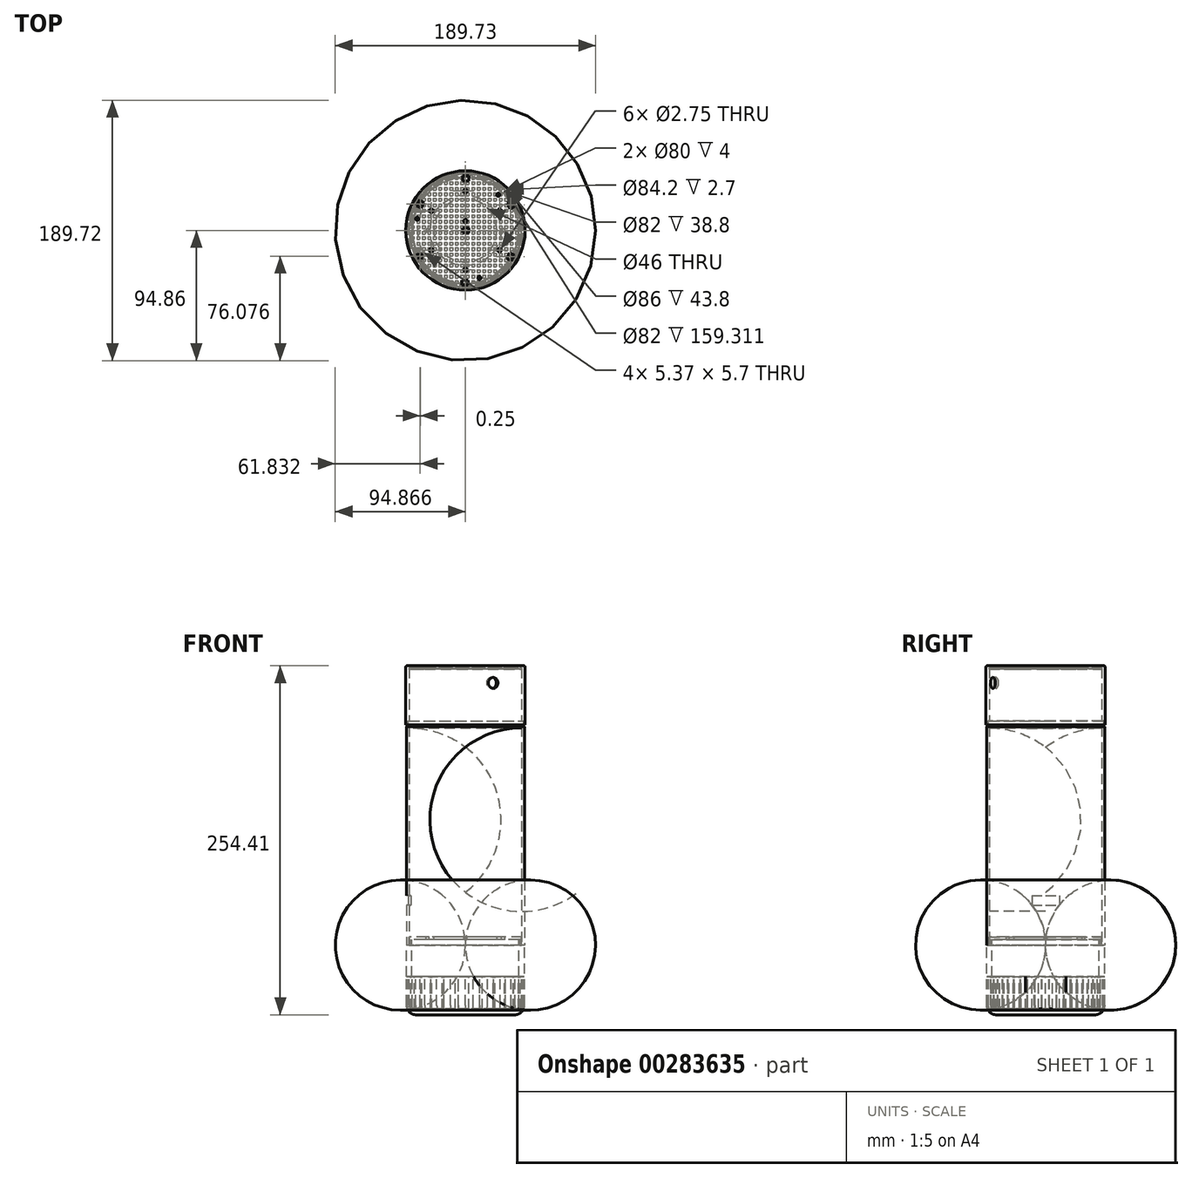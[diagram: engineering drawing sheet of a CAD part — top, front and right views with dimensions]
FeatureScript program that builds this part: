
annotation { "Feature Type Name" : "Feature", "Feature Type Description" : "" }
export const myFeature = defineFeature(function(context is Context, id is Id, definition is map)
    precondition{}
    {
        {
            var Q0;
            Q0=qCreatedBy(makeId("Front.planeOp"),FACE);
            var sketch = newSketch(context, id + "F0", { "sketchPlane" : qUnion([Q0])});
            skLineSegment(sketch, "E0", {"start": v(-50.53, -12.24) * mm, "end": v(-47.53, -12.24) * mm});
            skLineSegment(sketch, "E1", {"start": v(-7.53, -12.24) * mm, "end": v(-7.53, -63.04) * mm});
            skLineSegment(sketch, "E2", {"start": v(-50.53, -12.24) * mm, "end": v(-50.53, -56.04) * mm});
            skLineSegment(sketch, "E3", {"start": v(-7.53, -63.04) * mm, "end": v(-37.53, -63.04) * mm});
            skPoint(sketch, "E4.visualSharp", {"position": v(-50.53, -63.04) * mm});
            skArc(sketch, "E4.filletArc", {"start": v(-50.53, -56.04) * mm, "mid": v(-48.48, -61) * mm, "end": v(-43.53, -63.04) * mm});
            skLineSegment(sketch, "E5", {"start": v(-40.53, -63.04) * mm, "end": v(-37.53, -63.04) * mm});
            skLineSegment(sketch, "E6", {"start": v(-7.53, -63.04) * mm, "end": v(-7.53, -61.54) * mm});
            skLineSegment(sketch, "E7", {"start": v(-47.53, -12.24) * mm, "end": v(-47.53, -54.54) * mm});
            skLineSegment(sketch, "E8", {"start": v(-7.53, -61.54) * mm, "end": v(-40.53, -61.54) * mm});
            skPoint(sketch, "E9", {"position": v(-50.53, -34.14) * mm});
            skLineSegment(sketch, "E10", {"start": v(-50.53, -34.14) * mm, "end": v(-50.53, -47.14) * mm, "construction": true});
            skPoint(sketch, "E11", {"position": v(-50.53, -47.14) * mm});
            skLineSegment(sketch, "E12", {"start": v(-7.53, -63.04) * mm, "end": v(-7.53, 112.76) * mm, "construction": true});
            skLineSegment(sketch, "E13", {"start": v(-7.53, -8.24) * mm, "end": v(-7.53, -6.24) * mm});
            skLineSegment(sketch, "E14", {"start": v(-7.53, -59.5) * mm, "end": v(-7.53, -52.5) * mm});
            skLineSegment(sketch, "E15", {"start": v(-43.53, -63.04) * mm, "end": v(-40.53, -63.04) * mm});
            skLineSegment(sketch, "E16", {"start": v(-49.53, 148.07) * mm, "end": v(-48.53, 148.07) * mm});
            skLineSegment(sketch, "E17", {"start": v(-51.03, 191.37) * mm, "end": v(-7.53, 191.37) * mm});
            skLineSegment(sketch, "E18", {"start": v(-7.53, 191.37) * mm, "end": v(-7.53, 189.87) * mm});
            skPoint(sketch, "E19", {"position": v(-50.53, 181.87) * mm});
            skPoint(sketch, "E20", {"position": v(-47.73, 181.87) * mm});
            skLineSegment(sketch, "E21", {"start": v(-48.53, 151.07) * mm, "end": v(-48.53, 189.87) * mm});
            skLineSegment(sketch, "E22", {"start": v(-7.53, 191.37) * mm, "end": v(-7.53, 112.76) * mm, "construction": true});
            skPoint(sketch, "E23.end.orphan", {"position": v(-50.53, -2.93) * mm});
            skLineSegment(sketch, "E24", {"start": v(-50.53, -2.93) * mm, "end": v(-50.53, -12.24) * mm});
            skLineSegment(sketch, "E25", {"start": v(-48.53, -6.24) * mm, "end": v(-48.53, -12.24) * mm});
            skLineSegment(sketch, "E26", {"start": v(-47.53, -12.24) * mm, "end": v(-46.53, -12.24) * mm});
            skLineSegment(sketch, "E27", {"start": v(-48.53, -12.24) * mm, "end": v(-48.48, -12.24) * mm});
            skLineSegment(sketch, "E28", {"start": v(-48.48, -12.24) * mm, "end": v(-48.48, -6.24) * mm});
            skLineSegment(sketch, "E29", {"start": v(-48.48, -6.24) * mm, "end": v(-47.53, -6.24) * mm});
            skLineSegment(sketch, "E30", {"start": v(-47.53, -6.24) * mm, "end": v(-47.53, -12.24) * mm});
            skLineSegment(sketch, "E31", {"start": v(-7.53, -6.24) * mm, "end": v(-48.48, -6.24) * mm});
            skLineSegment(sketch, "E32", {"start": v(-7.53, -8.24) * mm, "end": v(-47.53, -8.24) * mm});
            skLineSegment(sketch, "E33", {"start": v(-47.53, -12.24) * mm, "end": v(-47.48, -12.24) * mm});
            skLineSegment(sketch, "E34", {"start": v(-47.48, -12.24) * mm, "end": v(-47.48, -8.24) * mm});
            skLineSegment(sketch, "E35", {"start": v(-47.48, -8.24) * mm, "end": v(-46.53, -8.24) * mm});
            skLineSegment(sketch, "E36", {"start": v(-46.53, -8.24) * mm, "end": v(-46.53, -12.24) * mm});
            skLineSegment(sketch, "E37", {"start": v(-46.53, -12.24) * mm, "end": v(-46.53, -58.92) * mm});
            skArc(sketch, "E38", {"start": v(-46.53, -58.92) * mm, "mid": v(-43.86, -60.98) * mm, "end": v(-40.53, -61.54) * mm});
            skArc(sketch, "E39", {"start": v(-46.53, -58.92) * mm, "mid": v(-18.57, -42.66) * mm, "end": v(-7.53, -12.24) * mm});
            skLineSegment(sketch, "E40", {"start": v(-49.58, 147.07) * mm, "end": v(-50.53, 147.07) * mm, "construction": true});
            skLineSegment(sketch, "E41", {"start": v(-49.53, 148.07) * mm, "end": v(-49.53, 147.07) * mm});
            skLineSegment(sketch, "E42", {"start": v(-49.53, 147.07) * mm, "end": v(-7.53, 147.07) * mm});
            skLineSegment(sketch, "E43", {"start": v(-48.53, 148.07) * mm, "end": v(-7.53, 148.07) * mm});
            skLineSegment(sketch, "E44", {"start": v(-7.53, 148.07) * mm, "end": v(-7.53, 147.07) * mm});
            skLineSegment(sketch, "E45", {"start": v(-49.58, 147.07) * mm, "end": v(-48.53, 147.07) * mm});
            skLineSegment(sketch, "E46", {"start": v(-48.53, 147.07) * mm, "end": v(-48.53, -6.24) * mm});
            skLineSegment(sketch, "E47", {"start": v(-48.53, -6.24) * mm, "end": v(-47.53, -6.24) * mm, "construction": true});
            skLineSegment(sketch, "E48", {"start": v(-48.53, 147.07) * mm, "end": v(-48.48, 147.07) * mm});
            skLineSegment(sketch, "E49", {"start": v(-48.48, 147.07) * mm, "end": v(-48.48, 146.07) * mm});
            skLineSegment(sketch, "E50", {"start": v(-7.53, 147.07) * mm, "end": v(-7.53, 132.07) * mm});
            skLineSegment(sketch, "E51", {"start": v(-48.48, 146.07) * mm, "end": v(-7.53, 146.07) * mm, "construction": true});
            skArc(sketch, "E52", {"start": v(-7.53, 132.07) * mm, "mid": v(-26.85, 142.47) * mm, "end": v(-48.48, 146.07) * mm});
            skLineSegment(sketch, "E53", {"start": v(-48.48, -6.24) * mm, "end": v(-48.53, 10.54) * mm, "construction": true});
            skLineSegment(sketch, "E54", {"start": v(-48.48, -6.24) * mm, "end": v(-48.53, 23.76) * mm, "construction": true});
            skPoint(sketch, "E55", {"position": v(-48.53, 23.76) * mm});
            skLineSegment(sketch, "E56", {"start": v(-51.03, 151.07) * mm, "end": v(-51.03, 191.37) * mm});
            skLineSegment(sketch, "E57", {"start": v(-48.53, 148.07) * mm, "end": v(-48.53, 147.07) * mm, "construction": true});
            skLineSegment(sketch, "E58", {"start": v(-48.53, 189.87) * mm, "end": v(-7.53, 189.87) * mm});
            skLineSegment(sketch, "E59", {"start": v(-50.53, -2.93) * mm, "end": v(-50.53, 147.07) * mm});
            skLineSegment(sketch, "E60", {"start": v(-50.53, 147.07) * mm, "end": v(-49.53, 147.07) * mm});
            skLineSegment(sketch, "E61", {"start": v(-51.03, 151.07) * mm, "end": v(-51.03, 148.37) * mm});
            skLineSegment(sketch, "E62", {"start": v(-51.03, 148.37) * mm, "end": v(-49.63, 148.37) * mm});
            skLineSegment(sketch, "E63", {"start": v(-49.63, 148.37) * mm, "end": v(-49.63, 151.07) * mm});
            skLineSegment(sketch, "E64", {"start": v(-49.63, 151.07) * mm, "end": v(-48.53, 151.07) * mm});
            skSolve(sketch);
        }
        {
            var Q0;
            {var subQ1=sQuery(id+"F0.wireOp",EDGE,"E0");Q0=makeQuery(id+"F0.imprint","IMPRINT",FACE,{"disambiguationData":[TD([[makeQuery(id+"F0.imprint","IMPRINT",EDGE,{"derivedFrom":subQ1}),-1.0]])]});}
            var Q1;
            Q1=makeQuery(id+"F0.imprint","IMPRINT",FACE,{"disambiguationData":[TD([[makeQuery(id+"F0.imprint","IMPRINT",EDGE,{"derivedFrom":sQuery(id+"F0.wireOp",EDGE,"E1")}),-1.0]])]});
            var Q2;
            Q2=makeQuery(id+"F0.imprint","IMPRINT",FACE,{"disambiguationData":[TD([[makeQuery(id+"F0.imprint","IMPRINT",EDGE,{"derivedFrom":sQuery(id+"F0.wireOp",EDGE,"E26")}),1.0]])]});
            var Q3;
            Q3=sQuery(id+"F0.wireOp",EDGE,"E1");
            revolve(context, id + "F1", {"entities" : qUnion([Q0, Q1, Q2]), "axis" : qUnion([Q3]), "revolveType" : RevolveType.FULL});
        }
        {
            var Q0;
            Q0=sQuery(id+"F0.wireOp",EDGE,"E2");
            var Q1;
            Q1=sQuery(id+"F0.wireOp",VERTEX,"E11");
            cPlane(context, id + "F2", {"entities" : qUnion([Q0, Q1]), "cplaneType" : CPlaneType.LINE_POINT, "offset" : 0 * mm, "width" : 150 * mm, "height" : 150 * mm});
        }
        {
            var Q0;
            Q0=qCreatedBy(id+"F2.planeOp",FACE);
            var sketch = newSketch(context, id + "F3", { "sketchPlane" : qUnion([Q0])});
            skLineSegment(sketch, "E65", {"start": v(-50.53, 0) * mm, "end": v(-46.03, 0) * mm, "construction": true});
            skLineSegment(sketch, "E66", {"start": v(-46.03, 0) * mm, "end": v(-46.03, 2.5) * mm, "construction": true});
            skLineSegment(sketch, "E67", {"start": v(-46.03, 2.5) * mm, "end": v(-50.53, 2.5) * mm});
            skLineSegment(sketch, "E68", {"start": v(-50.53, 2.5) * mm, "end": v(-50.53, -2.5) * mm});
            skLineSegment(sketch, "E69", {"start": v(-50.53, -2.5) * mm, "end": v(-46.03, -2.5) * mm});
            skLineSegment(sketch, "E70", {"start": v(-46.03, -2.5) * mm, "end": v(-46.03, 2.5) * mm});
            skLineSegment(sketch, "E71", {"start": v(-46.03, -6.5) * mm, "end": v(-46.03, -2.5) * mm});
            skLineSegment(sketch, "E72.MirrorCS", {"start": v(-46.03, 6.5) * mm, "end": v(-46.03, 2.5) * mm});
            skLineSegment(sketch, "E73", {"start": v(-46.03, -2.5) * mm, "end": v(-47.13, -2.5) * mm, "construction": true});
            skLineSegment(sketch, "E74", {"start": v(-47.13, -2.5) * mm, "end": v(-47.13, -5.3) * mm, "construction": true});
            skArc(sketch, "E75", {"start": v(-47.13, -5.3) * mm, "mid": v(-48.33, -3.3) * mm, "end": v(-50.53, -2.5) * mm});
            skArc(sketch, "E76", {"start": v(-47.13, -5.3) * mm, "mid": v(-46.82, -6.11) * mm, "end": v(-46.03, -6.5) * mm});
            skArc(sketch, "E77.MirrorCS", {"start": v(-47.13, 5.3) * mm, "mid": v(-48.33, 3.3) * mm, "end": v(-50.53, 2.5) * mm});
            skArc(sketch, "E78.MirrorCS", {"start": v(-47.13, 5.3) * mm, "mid": v(-46.82, 6.11) * mm, "end": v(-46.03, 6.5) * mm});
            skSolve(sketch);
        }
        {
            var Q0;
            Q0=qSketchRegion(id+"F3",true);
            extrude(context, id + "F4", {"entities" : qUnion([Q0]), "endBound" : BoundingType.SYMMETRIC, "depth" : 23.8 * mm});
        }
        {
            var Q0;
            Q0=makeQuery(id+"F4.opExtrude","SWEPT_BODY",BODY,{"disambiguationData":[OSD([sQuery(id+"F3.wireOp",EDGE,"E67"),sQuery(id+"F3.wireOp",EDGE,"E68"),sQuery(id+"F3.wireOp",EDGE,"E69"),sQuery(id+"F3.wireOp",EDGE,"E70")])]});
            var Q1;
            Q1=sQuery(id+"F0.wireOp",EDGE,"E1");
            circularPattern(context, id + "F5", {"operationType" : NewBodyOperationType.REMOVE, "entities" : qUnion([Q0]), "axis" : qUnion([Q1]), "angle" : 360 * degree, "instanceCount" : 25, "equalSpace" : true});
        }
        {
            var Q0;
            {var subQ4=sQuery(id+"F0.wireOp",EDGE,"E28");Q0=makeQuery(id+"F0.imprint","IMPRINT",FACE,{"disambiguationData":[TD([[makeQuery(id+"F0.imprint","IMPRINT",EDGE,{"derivedFrom":subQ4}),-1.0]])]});}
            var Q1;
            {var subQ1=sQuery(id+"F0.wireOp",EDGE,"E13");Q1=makeQuery(id+"F0.imprint","IMPRINT",FACE,{"disambiguationData":[TD([[makeQuery(id+"F0.imprint","IMPRINT",EDGE,{"derivedFrom":subQ1}),1.0]])]});}
            var Q2;
            Q2=sQuery(id+"F0.wireOp",EDGE,"E1");
            revolve(context, id + "F6", {"entities" : qUnion([Q0, Q1]), "axis" : qUnion([Q2]), "revolveType" : RevolveType.FULL});
        }
        {
            var Q0;
            {var subQ1=sQuery(id+"F0.wireOp",EDGE,"E24");Q0=makeQuery(id+"F0.imprint","IMPRINT",FACE,{"disambiguationData":[TD([[makeQuery(id+"F0.imprint","IMPRINT",EDGE,{"derivedFrom":subQ1}),1.0]])]});}
            var Q1;
            Q1=sQuery(id+"F0.wireOp",EDGE,"E12");
            revolve(context, id + "F7", {"entities" : qUnion([Q0]), "axis" : qUnion([Q1]), "revolveType" : RevolveType.FULL});
        }
        {
            var Q0;
            Q0=makeQuery(id+"F0.imprint","IMPRINT",FACE,{"disambiguationData":[TD([[makeQuery(id+"F0.imprint","IMPRINT",EDGE,{"derivedFrom":sQuery(id+"F0.wireOp",EDGE,"E16")}),-1.0]])]});
            var Q1;
            Q1=makeQuery(id+"F0.imprint","IMPRINT",FACE,{"disambiguationData":[TD([[makeQuery(id+"F0.imprint","IMPRINT",EDGE,{"derivedFrom":sQuery(id+"F0.wireOp",EDGE,"E42")}),-1.0]])]});
            var Q2;
            Q2=sQuery(id+"F0.wireOp",EDGE,"E50");
            revolve(context, id + "F8", {"entities" : qUnion([Q0, Q1]), "axis" : qUnion([Q2]), "revolveType" : RevolveType.FULL});
        }
        {
            var Q0;
            Q0=makeQuery(id+"F0.imprint","IMPRINT",FACE,{"disambiguationData":[TD([[makeQuery(id+"F0.imprint","IMPRINT",EDGE,{"derivedFrom":sQuery(id+"F0.wireOp",EDGE,"E17")}),-1.0]])]});
            var Q1;
            Q1=sQuery(id+"F0.wireOp",EDGE,"E12");
            revolve(context, id + "F9", {"entities" : qUnion([Q0]), "axis" : qUnion([Q1]), "revolveType" : RevolveType.FULL});
        }
        {
            var Q0;
            Q0=makeQuery(id+"F9.opRevolve","SWEPT_EDGE",EDGE,{"disambiguationData":[OSD([sQuery(id+"F0.wireOp",EDGE,"f6rtj6dZ-6JDe-umgd-hrW0-nHuk5Vi6zJmO"),sQuery(id+"F0.wireOp",EDGE,"E17")])]});
            fillet(context, id + "F10", {"entities" : qUnion([Q0]), "radius" : 1 * mm, "tangentPropagation" : true, "allowEdgeOverflow" : false});
        }
        {
            var Q0;
            Q0=makeQuery(id+"F9.opRevolve","SWEPT_FACE",FACE,{"disambiguationData":[OSD([sQuery(id+"F0.wireOp",EDGE,"E17")])]});
            var sketch = newSketch(context, id + "F11", { "sketchPlane" : qUnion([Q0])});
            skPoint(sketch, "E79", {"position": v(-7.53, 0) * mm});
            skCircle(sketch, "E80", {"center": v(-7.53, 0) * mm, "radius": 40 * mm, "construction": true});
            skLineSegment(sketch, "E81", {"start": v(-7.53, 0) * mm, "end": v(-7.53, -40) * mm, "construction": true});
            skLineSegment(sketch, "E82.1.0", {"start": v(-7.53, 0) * mm, "end": v(27.1, -20) * mm, "construction": true});
            skLineSegment(sketch, "E82.2.0", {"start": v(-7.53, 0) * mm, "end": v(27.1, 20) * mm, "construction": true});
            skLineSegment(sketch, "E82.3.0", {"start": v(-7.53, 0) * mm, "end": v(-7.53, 40) * mm, "construction": true});
            skLineSegment(sketch, "E82.4.0", {"start": v(-7.53, 0) * mm, "end": v(-42.18, 20) * mm, "construction": true});
            skLineSegment(sketch, "E82.5.0", {"start": v(-7.53, 0) * mm, "end": v(-42.18, -20) * mm, "construction": true});
            skLineSegment(sketch, "E83", {"start": v(-7.53, -40) * mm, "end": v(-7.53, -38) * mm, "construction": true});
            skPoint(sketch, "E84", {"position": v(-7.53, -38) * mm});
            skLineSegment(sketch, "E85", {"start": v(-7.53, -38) * mm, "end": v(-5.53, -38) * mm, "construction": true});
            skLineSegment(sketch, "E86", {"start": v(-7.53, -38) * mm, "end": v(-10.03, -38) * mm, "construction": true});
            skLineSegment(sketch, "E87", {"start": v(-7.53, -38) * mm, "end": v(-7.53, -39.8) * mm, "construction": true});
            skLineSegment(sketch, "E88", {"start": v(-7.53, -38) * mm, "end": v(-7.53, -36.2) * mm, "construction": true});
            skLineSegment(sketch, "E89", {"start": v(-7.53, -36.2) * mm, "end": v(-5.53, -36.2) * mm});
            skLineSegment(sketch, "E90", {"start": v(-5.53, -36.2) * mm, "end": v(-5.53, -39.8) * mm});
            skLineSegment(sketch, "E91", {"start": v(-5.53, -39.8) * mm, "end": v(-10.03, -39.8) * mm});
            skLineSegment(sketch, "E92", {"start": v(-10.03, -39.8) * mm, "end": v(-10.03, -36.2) * mm});
            skLineSegment(sketch, "E93", {"start": v(-10.03, -36.2) * mm, "end": v(-7.53, -36.2) * mm});
            skLineSegment(sketch, "E94", {"start": v(-7.53, -38) * mm, "end": v(-7.53, -28.7) * mm, "construction": true});
            skCircle(sketch, "E95", {"center": v(-7.53, -28.7) * mm, "radius": 1.37 * mm});
            skCircle(sketch, "E96.1.0", {"center": v(17.32, -14.35) * mm, "radius": 1.37 * mm});
            skLineSegment(sketch, "E96.1.1", {"start": v(23.82, -18.1) * mm, "end": v(24.82, -16.37) * mm});
            skLineSegment(sketch, "E96.1.2", {"start": v(22.57, -20.27) * mm, "end": v(23.82, -18.1) * mm});
            skLineSegment(sketch, "E96.1.3", {"start": v(25.68, -22.07) * mm, "end": v(22.57, -20.27) * mm});
            skLineSegment(sketch, "E96.1.4", {"start": v(24.82, -16.37) * mm, "end": v(27.93, -18.17) * mm});
            skLineSegment(sketch, "E96.1.5", {"start": v(27.93, -18.17) * mm, "end": v(25.68, -22.07) * mm});
            skCircle(sketch, "E96.2.0", {"center": v(17.32, 14.35) * mm, "radius": 1.37 * mm});
            skLineSegment(sketch, "E96.2.1", {"start": v(23.82, 18.1) * mm, "end": v(22.82, 19.83) * mm});
            skLineSegment(sketch, "E96.2.2", {"start": v(25.07, 15.93) * mm, "end": v(23.82, 18.1) * mm});
            skLineSegment(sketch, "E96.2.3", {"start": v(28.18, 17.73) * mm, "end": v(25.07, 15.93) * mm});
            skLineSegment(sketch, "E96.2.4", {"start": v(22.82, 19.83) * mm, "end": v(25.93, 21.63) * mm});
            skLineSegment(sketch, "E96.2.5", {"start": v(25.93, 21.63) * mm, "end": v(28.18, 17.73) * mm});
            skCircle(sketch, "E96.3.0", {"center": v(-7.53, 28.7) * mm, "radius": 1.37 * mm});
            skLineSegment(sketch, "E96.3.1", {"start": v(-7.53, 36.2) * mm, "end": v(-9.53, 36.2) * mm});
            skLineSegment(sketch, "E96.3.2", {"start": v(-5.03, 36.2) * mm, "end": v(-7.53, 36.2) * mm});
            skLineSegment(sketch, "E96.3.3", {"start": v(-5.03, 39.8) * mm, "end": v(-5.03, 36.2) * mm});
            skLineSegment(sketch, "E96.3.4", {"start": v(-9.53, 36.2) * mm, "end": v(-9.53, 39.8) * mm});
            skLineSegment(sketch, "E96.3.5", {"start": v(-9.53, 39.8) * mm, "end": v(-5.03, 39.8) * mm});
            skCircle(sketch, "E96.4.0", {"center": v(-32.39, 14.35) * mm, "radius": 1.37 * mm});
            skLineSegment(sketch, "E96.4.1", {"start": v(-38.88, 18.1) * mm, "end": v(-39.88, 16.37) * mm});
            skLineSegment(sketch, "E96.4.2", {"start": v(-37.63, 20.27) * mm, "end": v(-38.88, 18.1) * mm});
            skLineSegment(sketch, "E96.4.3", {"start": v(-40.75, 22.07) * mm, "end": v(-37.63, 20.27) * mm});
            skLineSegment(sketch, "E96.4.4", {"start": v(-39.88, 16.37) * mm, "end": v(-43, 18.17) * mm});
            skLineSegment(sketch, "E96.4.5", {"start": v(-43, 18.17) * mm, "end": v(-40.75, 22.07) * mm});
            skCircle(sketch, "E96.5.0", {"center": v(-32.39, -14.35) * mm, "radius": 1.37 * mm});
            skLineSegment(sketch, "E96.5.1", {"start": v(-38.88, -18.1) * mm, "end": v(-37.88, -19.83) * mm});
            skLineSegment(sketch, "E96.5.2", {"start": v(-40.13, -15.93) * mm, "end": v(-38.88, -18.1) * mm});
            skLineSegment(sketch, "E96.5.3", {"start": v(-43.25, -17.73) * mm, "end": v(-40.13, -15.93) * mm});
            skLineSegment(sketch, "E96.5.4", {"start": v(-37.88, -19.83) * mm, "end": v(-41, -21.63) * mm});
            skLineSegment(sketch, "E96.5.5", {"start": v(-41, -21.63) * mm, "end": v(-43.25, -17.73) * mm});
            skLineSegment(sketch, "E97", {"start": v(-7.53, 0) * mm, "end": v(-7.53, 1.8) * mm, "construction": true});
            skLineSegment(sketch, "E98", {"start": v(-7.53, 1.8) * mm, "end": v(-9.53, 1.8) * mm, "construction": true});
            skLineSegment(sketch, "E99.bottom", {"start": v(-9.53, 1.8) * mm, "end": v(-5.03, 1.8) * mm});
            skLineSegment(sketch, "E99.top", {"start": v(-9.53, -1.8) * mm, "end": v(-5.03, -1.8) * mm});
            skLineSegment(sketch, "E99.left", {"start": v(-9.53, 1.8) * mm, "end": v(-9.53, -1.8) * mm});
            skLineSegment(sketch, "E99.right", {"start": v(-5.03, 1.8) * mm, "end": v(-5.03, -1.8) * mm});
            skLineSegment(sketch, "E100", {"start": v(-7.53, 0) * mm, "end": v(-7.53, 6.8) * mm, "construction": true});
            skCircle(sketch, "E101", {"center": v(-7.53, 6.8) * mm, "radius": 1.25 * mm});
            skLineSegment(sketch, "E102", {"start": v(-7.53, -38) * mm, "end": v(2.64, -34.68) * mm, "construction": true});
            skLineSegment(sketch, "E103", {"start": v(2.64, -38.68) * mm, "end": v(2.64, -34.68) * mm, "construction": true});
            skCircle(sketch, "E104", {"center": v(2.64, -34.68) * mm, "radius": 1.15 * mm});
            skCircle(sketch, "E105.1.0", {"center": v(16.43, 25.99) * mm, "radius": 1.15 * mm});
            skCircle(sketch, "E105.2.0", {"center": v(-42.66, 8.53) * mm, "radius": 1.15 * mm});
            skLineSegment(sketch, "E106", {"start": v(2.64, -34.68) * mm, "end": v(25.68, -22.07) * mm, "construction": true});
            skLineSegment(sketch, "E107", {"start": v(2.64, -34.68) * mm, "end": v(9.66, -30.84) * mm, "construction": true});
            skLineSegment(sketch, "E108", {"start": v(9.66, -30.84) * mm, "end": v(13.35, -37.59) * mm, "construction": true});
            skPoint(sketch, "E109", {"position": v(13.35, -37.59) * mm});
            skCircle(sketch, "E110.0", {"center": v(-7.53, 0) * mm, "radius": 41 * mm, "construction": true});
            skSolve(sketch);
        }
        {
            var Q0;
            Q0=qSketchRegion(id+"F11",true);
            extrude(context, id + "F12", {"entities" : qUnion([Q0]), "operationType" : NewBodyOperationType.REMOVE, "endBound" : BoundingType.UP_TO_NEXT, "oppositeDirection" : true, "depth" : 25 * mm});
        }
        {
            var Q0;
            Q0=sQuery(id+"F11.wireOp",VERTEX,"E109");
            var Q1;
            Q1=sQuery(id+"F11.wireOp",EDGE,"E108");
            cPlane(context, id + "F13", {"entities" : qUnion([Q0, Q1]), "cplaneType" : CPlaneType.LINE_POINT, "offset" : 25 * mm, "width" : 150 * mm, "height" : 150 * mm});
        }
        {
            var Q0;
            Q0=qCreatedBy(id+"F13.planeOp",FACE);
            var sketch = newSketch(context, id + "F14", { "sketchPlane" : qUnion([Q0])});
            skLineSegment(sketch, "E111", {"start": v(-7.34, 191.37) * mm, "end": v(-7.34, 178.87) * mm, "construction": true});
            skCircle(sketch, "E112", {"center": v(-7.34, 178.87) * mm, "radius": 4 * mm});
            skLineSegment(sketch, "E113", {"start": v(-48.6, 191.37) * mm, "end": v(35.4, 191.37) * mm});
            skSolve(sketch);
        }
        {
            var Q0;
            Q0=qSketchRegion(id+"F14",true);
            extrude(context, id + "F15", {"entities" : qUnion([Q0]), "operationType" : NewBodyOperationType.REMOVE, "endBound" : BoundingType.SYMMETRIC, "oppositeDirection" : true, "depth" : 7 * mm});
        }
        {
            var Q0;
            Q0=makeQuery(id+"F8.opRevolve","SWEPT_FACE",FACE,{"disambiguationData":[OSD([sQuery(id+"F0.wireOp",EDGE,"E16"),sQuery(id+"F0.wireOp",EDGE,"E43")])]});
            var sketch = newSketch(context, id + "F16", { "sketchPlane" : qUnion([Q0])});
            skCircle(sketch, "E114.0", {"center": v(-7.53, 0) * mm, "radius": 42 * mm, "construction": true});
            skLineSegment(sketch, "E115", {"start": v(-49.53, 0) * mm, "end": v(-48.48, 0) * mm, "construction": true});
            skCircle(sketch, "E116.0", {"center": v(-7.53, 0) * mm, "radius": 40.95 * mm});
            skLineSegment(sketch, "E117", {"start": v(-48.48, 0) * mm, "end": v(-45.74, 14.75) * mm, "construction": true});
            skLineSegment(sketch, "E118.MirrorCS", {"start": v(-48.48, 0) * mm, "end": v(-45.74, -14.75) * mm, "construction": true});
            skCircle(sketch, "E119.0", {"center": v(-7.53, 0) * mm, "radius": 34.95 * mm});
            skLineSegment(sketch, "E120", {"start": v(-45.74, 14.75) * mm, "end": v(-39.72, 13.63) * mm});
            skLineSegment(sketch, "E121.MirrorCS", {"start": v(-45.74, -14.75) * mm, "end": v(-39.72, -13.63) * mm});
            skSolve(sketch);
        }
        {
            var Q0;
            {var subQ0=sQuery(id+"F16.wireOp",EDGE,"E120");Q0=makeQuery(id+"F16.imprint","IMPRINT",FACE,{"disambiguationData":[TD([[makeQuery(id+"F16.imprint","IMPRINT",EDGE,{"derivedFrom":subQ0}),-1.0]])]});}
            extrude(context, id + "F17", {"entities" : qUnion([Q0]), "operationType" : NewBodyOperationType.REMOVE, "endBound" : BoundingType.UP_TO_NEXT, "oppositeDirection" : true, "depth" : 25 * mm});
        }
        {
            var Q0;
            Q0=sQuery(id+"F0.wireOp",EDGE,"E46");
            cPlane(context, id + "F18", {"entities" : qUnion([Q0]), "cplaneType" : CPlaneType.LINE_ANGLE, "offset" : 25 * mm, "angle" : 0 * degree, "width" : 150 * mm, "height" : 150 * mm});
        }
        {
            var Q0;
            Q0=qCreatedBy(id+"F18.planeOp",FACE);
            var sketch = newSketch(context, id + "F19", { "sketchPlane" : qUnion([Q0])});
            skPoint(sketch, "E122.0", {"position": v(0, 23.76) * mm});
            skLineSegment(sketch, "E123", {"start": v(0, 23.76) * mm, "end": v(10, 23.76) * mm});
            skLineSegment(sketch, "E124", {"start": v(10, 23.76) * mm, "end": v(-10, 23.76) * mm});
            skPoint(sketch, "E124.endSnap0", {"position": v(5, 23.76) * mm});
            skLineSegment(sketch, "E125", {"start": v(-10, 23.76) * mm, "end": v(-10, 16.76) * mm});
            skLineSegment(sketch, "E126", {"start": v(-10, 16.76) * mm, "end": v(10, 16.76) * mm});
            skLineSegment(sketch, "E127", {"start": v(10, 16.76) * mm, "end": v(10, 23.76) * mm});
            skSolve(sketch);
        }
        {
            var Q0;
            Q0=qSketchRegion(id+"F19",true);
            extrude(context, id + "F20", {"entities" : qUnion([Q0]), "operationType" : NewBodyOperationType.REMOVE, "endBound" : BoundingType.SYMMETRIC, "oppositeDirection" : true, "depth" : 5 * mm});
        }
        {
            var Q0;
            Q0=makeQuery(id+"F9.opRevolve","SWEPT_FACE",FACE,{"disambiguationData":[OSD([sQuery(id+"F0.wireOp",EDGE,"E58")])]});
            var sketch = newSketch(context, id + "F21", { "sketchPlane" : qUnion([Q0])});
            skCircle(sketch, "E128.0", {"center": v(-7.53, 0) * mm, "radius": 41 * mm, "construction": true});
            skCircle(sketch, "E129.0", {"center": v(-7.53, 0) * mm, "radius": 40.98 * mm});
            skLineSegment(sketch, "E130.0", {"start": v(-5.53, 39.8) * mm, "end": v(-5.53, 36.2) * mm});
            skLineSegment(sketch, "E131.0", {"start": v(-10.03, 39.8) * mm, "end": v(-5.53, 39.8) * mm});
            skLineSegment(sketch, "E132.0", {"start": v(-10.03, 36.2) * mm, "end": v(-10.03, 39.8) * mm});
            skLineSegment(sketch, "E133.0", {"start": v(-5.53, 36.2) * mm, "end": v(-10.03, 36.2) * mm});
            skCircle(sketch, "E134.0", {"center": v(2.64, 34.68) * mm, "radius": 1.15 * mm});
            skCircle(sketch, "E135.0", {"center": v(17.32, 14.35) * mm, "radius": 1.37 * mm});
            skCircle(sketch, "E136.0", {"center": v(17.32, -14.35) * mm, "radius": 1.37 * mm});
            skCircle(sketch, "E137.0", {"center": v(-7.53, -28.7) * mm, "radius": 1.37 * mm});
            skCircle(sketch, "E138.0", {"center": v(-32.39, -14.35) * mm, "radius": 1.37 * mm});
            skCircle(sketch, "E139.0", {"center": v(-42.66, -8.53) * mm, "radius": 1.15 * mm});
            skCircle(sketch, "E140.0", {"center": v(-32.39, 14.35) * mm, "radius": 1.37 * mm});
            skCircle(sketch, "E141.0", {"center": v(-7.53, 28.7) * mm, "radius": 1.37 * mm});
            skCircle(sketch, "E142.0", {"center": v(-7.53, -6.8) * mm, "radius": 1.25 * mm});
            skCircle(sketch, "E143.0", {"center": v(16.43, -25.99) * mm, "radius": 1.15 * mm});
            skLineSegment(sketch, "E144.0", {"start": v(22.57, 20.27) * mm, "end": v(25.68, 22.07) * mm});
            skLineSegment(sketch, "E145.0", {"start": v(25.68, 22.07) * mm, "end": v(27.93, 18.17) * mm});
            skLineSegment(sketch, "E146.0", {"start": v(27.93, 18.17) * mm, "end": v(24.82, 16.37) * mm});
            skLineSegment(sketch, "E147.0", {"start": v(24.82, 16.37) * mm, "end": v(22.57, 20.27) * mm});
            skLineSegment(sketch, "E148.0", {"start": v(25.07, -15.93) * mm, "end": v(28.18, -17.73) * mm});
            skLineSegment(sketch, "E149.0", {"start": v(28.18, -17.73) * mm, "end": v(25.93, -21.63) * mm});
            skLineSegment(sketch, "E150.0", {"start": v(25.93, -21.63) * mm, "end": v(22.82, -19.83) * mm});
            skLineSegment(sketch, "E151.0", {"start": v(22.82, -19.83) * mm, "end": v(25.07, -15.93) * mm});
            skLineSegment(sketch, "E152.0", {"start": v(-5.03, -36.2) * mm, "end": v(-5.03, -39.8) * mm});
            skLineSegment(sketch, "E153.0", {"start": v(-9.53, -36.2) * mm, "end": v(-5.03, -36.2) * mm});
            skLineSegment(sketch, "E154.0", {"start": v(-9.53, -39.8) * mm, "end": v(-9.53, -36.2) * mm});
            skLineSegment(sketch, "E155.0", {"start": v(-5.03, -39.8) * mm, "end": v(-9.53, -39.8) * mm});
            skLineSegment(sketch, "E156.0", {"start": v(-39.88, -16.37) * mm, "end": v(-37.63, -20.27) * mm});
            skLineSegment(sketch, "E157.0", {"start": v(-37.63, -20.27) * mm, "end": v(-40.75, -22.07) * mm});
            skLineSegment(sketch, "E158.0", {"start": v(-40.75, -22.07) * mm, "end": v(-43, -18.17) * mm});
            skLineSegment(sketch, "E159.0", {"start": v(-43, -18.17) * mm, "end": v(-39.88, -16.37) * mm});
            skLineSegment(sketch, "E160.0", {"start": v(-41, 21.63) * mm, "end": v(-37.88, 19.83) * mm});
            skLineSegment(sketch, "E161.0", {"start": v(-37.88, 19.83) * mm, "end": v(-40.13, 15.93) * mm});
            skLineSegment(sketch, "E162.0", {"start": v(-40.13, 15.93) * mm, "end": v(-43.25, 17.73) * mm});
            skLineSegment(sketch, "E163.0", {"start": v(-43.25, 17.73) * mm, "end": v(-41, 21.63) * mm});
            skLineSegment(sketch, "E164.0", {"start": v(-5.03, 1.8) * mm, "end": v(-5.03, -1.8) * mm});
            skLineSegment(sketch, "E165.0", {"start": v(-5.03, -1.8) * mm, "end": v(-9.53, -1.8) * mm});
            skLineSegment(sketch, "E166.0", {"start": v(-5.03, 1.8) * mm, "end": v(-9.53, 1.8) * mm});
            skLineSegment(sketch, "E167.0", {"start": v(-9.53, 1.8) * mm, "end": v(-9.53, -1.8) * mm});
            skSolve(sketch);
        }
        {
            var Q0;
            Q0=qSketchRegion(id+"F21",true);
            var Q1;
            Q1=makeQuery(id+"F21.imprint","IMPRINT",FACE,{"disambiguationData":[TD([[makeQuery(id+"F21.imprint","IMPRINT",EDGE,{"derivedFrom":sQuery(id+"F21.wireOp",EDGE,"6cf842b4-8cee-4f3a-be1a-66a8b3b2ef9b.0")}),1.0]])]});
            extrude(context, id + "F22", {"entities" : qUnion([Q0, Q1]), "depth" : 1 * mm});
        }
        {
            var Q0;
            Q0=makeQuery(id+"F22.opExtrude","CAP_FACE",FACE,{"disambiguationData":[OSD([sQuery(id+"F21.wireOp",EDGE,"E129.0"),sQuery(id+"F21.wireOp",EDGE,"E130.0"),sQuery(id+"F21.wireOp",EDGE,"E131.0"),sQuery(id+"F21.wireOp",EDGE,"E132.0"),sQuery(id+"F21.wireOp",EDGE,"E133.0"),sQuery(id+"F21.wireOp",EDGE,"E134.0"),sQuery(id+"F21.wireOp",EDGE,"E135.0"),sQuery(id+"F21.wireOp",EDGE,"E136.0"),sQuery(id+"F21.wireOp",EDGE,"E137.0"),sQuery(id+"F21.wireOp",EDGE,"E138.0"),sQuery(id+"F21.wireOp",EDGE,"E139.0"),sQuery(id+"F21.wireOp",EDGE,"E140.0"),sQuery(id+"F21.wireOp",EDGE,"E141.0"),sQuery(id+"F21.wireOp",EDGE,"E142.0"),sQuery(id+"F21.wireOp",EDGE,"E143.0"),sQuery(id+"F21.wireOp",EDGE,"E144.0"),sQuery(id+"F21.wireOp",EDGE,"E145.0"),sQuery(id+"F21.wireOp",EDGE,"E146.0"),sQuery(id+"F21.wireOp",EDGE,"E147.0"),sQuery(id+"F21.wireOp",EDGE,"E148.0"),sQuery(id+"F21.wireOp",EDGE,"E149.0"),sQuery(id+"F21.wireOp",EDGE,"E150.0"),sQuery(id+"F21.wireOp",EDGE,"E151.0"),sQuery(id+"F21.wireOp",EDGE,"E152.0"),sQuery(id+"F21.wireOp",EDGE,"E153.0"),sQuery(id+"F21.wireOp",EDGE,"E154.0"),sQuery(id+"F21.wireOp",EDGE,"E155.0"),sQuery(id+"F21.wireOp",EDGE,"E156.0"),sQuery(id+"F21.wireOp",EDGE,"E157.0"),sQuery(id+"F21.wireOp",EDGE,"E158.0"),sQuery(id+"F21.wireOp",EDGE,"E159.0"),sQuery(id+"F21.wireOp",EDGE,"E160.0"),sQuery(id+"F21.wireOp",EDGE,"E161.0"),sQuery(id+"F21.wireOp",EDGE,"E162.0"),sQuery(id+"F21.wireOp",EDGE,"E163.0"),sQuery(id+"F21.wireOp",EDGE,"E164.0"),sQuery(id+"F21.wireOp",EDGE,"E165.0"),sQuery(id+"F21.wireOp",EDGE,"E166.0"),sQuery(id+"F21.wireOp",EDGE,"E167.0")])],"isStart":true});
            var sketch = newSketch(context, id + "F23", { "sketchPlane" : qUnion([Q0])});
            skLineSegment(sketch, "E168.0", {"start": v(22.57, -20.27) * mm, "end": v(25.68, -22.07) * mm});
            skLineSegment(sketch, "E169.0", {"start": v(25.68, -22.07) * mm, "end": v(27.93, -18.17) * mm});
            skLineSegment(sketch, "E170.0", {"start": v(27.93, -18.17) * mm, "end": v(24.82, -16.37) * mm});
            skLineSegment(sketch, "E171.0", {"start": v(24.82, -16.37) * mm, "end": v(22.57, -20.27) * mm});
            skCircle(sketch, "E172.0", {"center": v(-7.53, -28.7) * mm, "radius": 1.37 * mm});
            skLineSegment(sketch, "E173.0", {"start": v(-5.53, -36.2) * mm, "end": v(-10.03, -36.2) * mm});
            skLineSegment(sketch, "E174.0", {"start": v(-5.53, -39.8) * mm, "end": v(-5.53, -36.2) * mm});
            skLineSegment(sketch, "E175.0", {"start": v(-10.03, -39.8) * mm, "end": v(-5.53, -39.8) * mm});
            skPoint(sketch, "E176.0", {"position": v(-10.03, -38) * mm});
            skLineSegment(sketch, "E177.0", {"start": v(-10.03, -36.2) * mm, "end": v(-10.03, -39.8) * mm});
            skLineSegment(sketch, "E178.0", {"start": v(-41, -21.63) * mm, "end": v(-37.88, -19.83) * mm});
            skLineSegment(sketch, "E179.0", {"start": v(-43.25, -17.73) * mm, "end": v(-41, -21.63) * mm});
            skLineSegment(sketch, "E180.0", {"start": v(-40.13, -15.93) * mm, "end": v(-43.25, -17.73) * mm});
            skLineSegment(sketch, "E181.0", {"start": v(-37.88, -19.83) * mm, "end": v(-40.13, -15.93) * mm});
            skLineSegment(sketch, "E182.0", {"start": v(-43, 18.17) * mm, "end": v(-39.88, 16.37) * mm});
            skLineSegment(sketch, "E183.0", {"start": v(-39.88, 16.37) * mm, "end": v(-37.63, 20.27) * mm});
            skLineSegment(sketch, "E184.0", {"start": v(-37.63, 20.27) * mm, "end": v(-40.75, 22.07) * mm});
            skLineSegment(sketch, "E185.0", {"start": v(-40.75, 22.07) * mm, "end": v(-43, 18.17) * mm});
            skLineSegment(sketch, "E186.0", {"start": v(-9.53, 36.2) * mm, "end": v(-5.03, 36.2) * mm});
            skLineSegment(sketch, "E187.0", {"start": v(-9.53, 39.8) * mm, "end": v(-9.53, 36.2) * mm});
            skLineSegment(sketch, "E188.0", {"start": v(-5.03, 39.8) * mm, "end": v(-9.53, 39.8) * mm});
            skLineSegment(sketch, "E189.0", {"start": v(-5.03, 36.2) * mm, "end": v(-5.03, 39.8) * mm});
            skLineSegment(sketch, "E190.0", {"start": v(25.07, 15.93) * mm, "end": v(28.18, 17.73) * mm});
            skLineSegment(sketch, "E191.0", {"start": v(22.82, 19.83) * mm, "end": v(25.07, 15.93) * mm});
            skLineSegment(sketch, "E192.0", {"start": v(25.93, 21.63) * mm, "end": v(22.82, 19.83) * mm});
            skLineSegment(sketch, "E193.0", {"start": v(28.18, 17.73) * mm, "end": v(25.93, 21.63) * mm});
            skLineSegment(sketch, "E194.0", {"start": v(-5.03, -1.8) * mm, "end": v(-9.53, -1.8) * mm});
            skLineSegment(sketch, "E195.0", {"start": v(-5.03, -1.8) * mm, "end": v(-5.03, 1.8) * mm});
            skLineSegment(sketch, "E196.0", {"start": v(-5.03, 1.8) * mm, "end": v(-9.53, 1.8) * mm});
            skLineSegment(sketch, "E197.0", {"start": v(-9.53, -1.8) * mm, "end": v(-9.53, 1.8) * mm});
            skCircle(sketch, "E198.0", {"center": v(2.64, -34.68) * mm, "radius": 1.15 * mm});
            skCircle(sketch, "E199.0", {"center": v(-32.39, -14.35) * mm, "radius": 1.37 * mm});
            skCircle(sketch, "E200.0", {"center": v(-42.66, 8.53) * mm, "radius": 1.15 * mm});
            skCircle(sketch, "E201.0", {"center": v(-7.53, 6.8) * mm, "radius": 1.25 * mm});
            skCircle(sketch, "E202.0", {"center": v(-32.39, 14.35) * mm, "radius": 1.37 * mm});
            skCircle(sketch, "E203.0", {"center": v(-7.53, 28.7) * mm, "radius": 1.37 * mm});
            skCircle(sketch, "E204.0", {"center": v(16.43, 25.99) * mm, "radius": 1.15 * mm});
            skCircle(sketch, "E205.0", {"center": v(17.32, 14.35) * mm, "radius": 1.37 * mm});
            skCircle(sketch, "E206.0", {"center": v(17.32, -14.35) * mm, "radius": 1.37 * mm});
            skLineSegment(sketch, "E207.bottom", {"start": v(-50.95, 43.44) * mm, "end": v(-48.95, 43.44) * mm});
            skLineSegment(sketch, "E207.top", {"start": v(-50.95, 41.44) * mm, "end": v(-48.95, 41.44) * mm});
            skLineSegment(sketch, "E207.left", {"start": v(-50.95, 43.44) * mm, "end": v(-50.95, 41.44) * mm});
            skLineSegment(sketch, "E207.right", {"start": v(-48.95, 43.44) * mm, "end": v(-48.95, 41.44) * mm});
            skLineSegment(sketch, "E208.0.1.0", {"start": v(-50.95, 39.44) * mm, "end": v(-48.95, 39.44) * mm});
            skLineSegment(sketch, "E208.0.1.1", {"start": v(-50.95, 39.44) * mm, "end": v(-50.95, 37.44) * mm});
            skLineSegment(sketch, "E208.0.1.2", {"start": v(-50.95, 37.44) * mm, "end": v(-48.95, 37.44) * mm});
            skLineSegment(sketch, "E208.0.1.3", {"start": v(-48.95, 39.44) * mm, "end": v(-48.95, 37.44) * mm});
            skLineSegment(sketch, "E208.0.2.0", {"start": v(-50.95, 35.44) * mm, "end": v(-48.95, 35.44) * mm});
            skLineSegment(sketch, "E208.0.2.1", {"start": v(-50.95, 35.44) * mm, "end": v(-50.95, 33.44) * mm});
            skLineSegment(sketch, "E208.0.2.2", {"start": v(-50.95, 33.44) * mm, "end": v(-48.95, 33.44) * mm});
            skLineSegment(sketch, "E208.0.2.3", {"start": v(-48.95, 35.44) * mm, "end": v(-48.95, 33.44) * mm});
            skLineSegment(sketch, "E208.0.3.0", {"start": v(-50.95, 31.44) * mm, "end": v(-48.95, 31.44) * mm});
            skLineSegment(sketch, "E208.0.3.1", {"start": v(-50.95, 31.44) * mm, "end": v(-50.95, 29.44) * mm});
            skLineSegment(sketch, "E208.0.3.2", {"start": v(-50.95, 29.44) * mm, "end": v(-48.95, 29.44) * mm});
            skLineSegment(sketch, "E208.0.3.3", {"start": v(-48.95, 31.44) * mm, "end": v(-48.95, 29.44) * mm});
            skLineSegment(sketch, "E208.0.4.0", {"start": v(-50.95, 27.44) * mm, "end": v(-48.95, 27.44) * mm});
            skLineSegment(sketch, "E208.0.4.1", {"start": v(-50.95, 27.44) * mm, "end": v(-50.95, 25.44) * mm});
            skLineSegment(sketch, "E208.0.4.2", {"start": v(-50.95, 25.44) * mm, "end": v(-48.95, 25.44) * mm});
            skLineSegment(sketch, "E208.0.4.3", {"start": v(-48.95, 27.44) * mm, "end": v(-48.95, 25.44) * mm});
            skLineSegment(sketch, "E208.0.5.0", {"start": v(-50.95, 23.44) * mm, "end": v(-48.95, 23.44) * mm});
            skLineSegment(sketch, "E208.0.5.1", {"start": v(-50.95, 23.44) * mm, "end": v(-50.95, 21.44) * mm});
            skLineSegment(sketch, "E208.0.5.2", {"start": v(-50.95, 21.44) * mm, "end": v(-48.95, 21.44) * mm});
            skLineSegment(sketch, "E208.0.5.3", {"start": v(-48.95, 23.44) * mm, "end": v(-48.95, 21.44) * mm});
            skLineSegment(sketch, "E208.0.6.0", {"start": v(-50.95, 19.44) * mm, "end": v(-48.95, 19.44) * mm});
            skLineSegment(sketch, "E208.0.6.1", {"start": v(-50.95, 19.44) * mm, "end": v(-50.95, 17.44) * mm});
            skLineSegment(sketch, "E208.0.6.2", {"start": v(-50.95, 17.44) * mm, "end": v(-48.95, 17.44) * mm});
            skLineSegment(sketch, "E208.0.6.3", {"start": v(-48.95, 19.44) * mm, "end": v(-48.95, 17.44) * mm});
            skLineSegment(sketch, "E208.0.7.0", {"start": v(-50.95, 15.44) * mm, "end": v(-48.95, 15.44) * mm});
            skLineSegment(sketch, "E208.0.7.1", {"start": v(-50.95, 15.44) * mm, "end": v(-50.95, 13.44) * mm});
            skLineSegment(sketch, "E208.0.7.2", {"start": v(-50.95, 13.44) * mm, "end": v(-48.95, 13.44) * mm});
            skLineSegment(sketch, "E208.0.7.3", {"start": v(-48.95, 15.44) * mm, "end": v(-48.95, 13.44) * mm});
            skLineSegment(sketch, "E208.0.8.0", {"start": v(-50.95, 11.44) * mm, "end": v(-48.95, 11.44) * mm});
            skLineSegment(sketch, "E208.0.8.1", {"start": v(-50.95, 11.44) * mm, "end": v(-50.95, 9.44) * mm});
            skLineSegment(sketch, "E208.0.8.2", {"start": v(-50.95, 9.44) * mm, "end": v(-48.95, 9.44) * mm});
            skLineSegment(sketch, "E208.0.8.3", {"start": v(-48.95, 11.44) * mm, "end": v(-48.95, 9.44) * mm});
            skLineSegment(sketch, "E208.0.9.0", {"start": v(-50.95, 7.44) * mm, "end": v(-48.95, 7.44) * mm});
            skLineSegment(sketch, "E208.0.9.1", {"start": v(-50.95, 7.44) * mm, "end": v(-50.95, 5.44) * mm});
            skLineSegment(sketch, "E208.0.9.2", {"start": v(-50.95, 5.44) * mm, "end": v(-48.95, 5.44) * mm});
            skLineSegment(sketch, "E208.0.9.3", {"start": v(-48.95, 7.44) * mm, "end": v(-48.95, 5.44) * mm});
            skLineSegment(sketch, "E208.0.10.0", {"start": v(-50.95, 3.44) * mm, "end": v(-48.95, 3.44) * mm});
            skLineSegment(sketch, "E208.0.10.1", {"start": v(-50.95, 3.44) * mm, "end": v(-50.95, 1.44) * mm});
            skLineSegment(sketch, "E208.0.10.2", {"start": v(-50.95, 1.44) * mm, "end": v(-48.95, 1.44) * mm});
            skLineSegment(sketch, "E208.0.10.3", {"start": v(-48.95, 3.44) * mm, "end": v(-48.95, 1.44) * mm});
            skLineSegment(sketch, "E208.0.11.0", {"start": v(-50.95, -0.56) * mm, "end": v(-48.95, -0.56) * mm});
            skLineSegment(sketch, "E208.0.11.1", {"start": v(-50.95, -0.56) * mm, "end": v(-50.95, -2.56) * mm});
            skLineSegment(sketch, "E208.0.11.2", {"start": v(-50.95, -2.56) * mm, "end": v(-48.95, -2.56) * mm});
            skLineSegment(sketch, "E208.0.11.3", {"start": v(-48.95, -0.56) * mm, "end": v(-48.95, -2.56) * mm});
            skLineSegment(sketch, "E208.0.12.0", {"start": v(-50.95, -4.56) * mm, "end": v(-48.95, -4.56) * mm});
            skLineSegment(sketch, "E208.0.12.1", {"start": v(-50.95, -4.56) * mm, "end": v(-50.95, -6.56) * mm});
            skLineSegment(sketch, "E208.0.12.2", {"start": v(-50.95, -6.56) * mm, "end": v(-48.95, -6.56) * mm});
            skLineSegment(sketch, "E208.0.12.3", {"start": v(-48.95, -4.56) * mm, "end": v(-48.95, -6.56) * mm});
            skLineSegment(sketch, "E208.0.13.0", {"start": v(-50.95, -8.56) * mm, "end": v(-48.95, -8.56) * mm});
            skLineSegment(sketch, "E208.0.13.1", {"start": v(-50.95, -8.56) * mm, "end": v(-50.95, -10.56) * mm});
            skLineSegment(sketch, "E208.0.13.2", {"start": v(-50.95, -10.56) * mm, "end": v(-48.95, -10.56) * mm});
            skLineSegment(sketch, "E208.0.13.3", {"start": v(-48.95, -8.56) * mm, "end": v(-48.95, -10.56) * mm});
            skLineSegment(sketch, "E208.0.14.0", {"start": v(-50.95, -12.56) * mm, "end": v(-48.95, -12.56) * mm});
            skLineSegment(sketch, "E208.0.14.1", {"start": v(-50.95, -12.56) * mm, "end": v(-50.95, -14.56) * mm});
            skLineSegment(sketch, "E208.0.14.2", {"start": v(-50.95, -14.56) * mm, "end": v(-48.95, -14.56) * mm});
            skLineSegment(sketch, "E208.0.14.3", {"start": v(-48.95, -12.56) * mm, "end": v(-48.95, -14.56) * mm});
            skLineSegment(sketch, "E208.0.15.0", {"start": v(-50.95, -16.56) * mm, "end": v(-48.95, -16.56) * mm});
            skLineSegment(sketch, "E208.0.15.1", {"start": v(-50.95, -16.56) * mm, "end": v(-50.95, -18.56) * mm});
            skLineSegment(sketch, "E208.0.15.2", {"start": v(-50.95, -18.56) * mm, "end": v(-48.95, -18.56) * mm});
            skLineSegment(sketch, "E208.0.15.3", {"start": v(-48.95, -16.56) * mm, "end": v(-48.95, -18.56) * mm});
            skLineSegment(sketch, "E208.0.16.0", {"start": v(-50.95, -20.56) * mm, "end": v(-48.95, -20.56) * mm});
            skLineSegment(sketch, "E208.0.16.1", {"start": v(-50.95, -20.56) * mm, "end": v(-50.95, -22.56) * mm});
            skLineSegment(sketch, "E208.0.16.2", {"start": v(-50.95, -22.56) * mm, "end": v(-48.95, -22.56) * mm});
            skLineSegment(sketch, "E208.0.16.3", {"start": v(-48.95, -20.56) * mm, "end": v(-48.95, -22.56) * mm});
            skLineSegment(sketch, "E208.0.17.0", {"start": v(-50.95, -24.56) * mm, "end": v(-48.95, -24.56) * mm});
            skLineSegment(sketch, "E208.0.17.1", {"start": v(-50.95, -24.56) * mm, "end": v(-50.95, -26.56) * mm});
            skLineSegment(sketch, "E208.0.17.2", {"start": v(-50.95, -26.56) * mm, "end": v(-48.95, -26.56) * mm});
            skLineSegment(sketch, "E208.0.17.3", {"start": v(-48.95, -24.56) * mm, "end": v(-48.95, -26.56) * mm});
            skLineSegment(sketch, "E208.0.18.0", {"start": v(-50.95, -28.56) * mm, "end": v(-48.95, -28.56) * mm});
            skLineSegment(sketch, "E208.0.18.1", {"start": v(-50.95, -28.56) * mm, "end": v(-50.95, -30.56) * mm});
            skLineSegment(sketch, "E208.0.18.2", {"start": v(-50.95, -30.56) * mm, "end": v(-48.95, -30.56) * mm});
            skLineSegment(sketch, "E208.0.18.3", {"start": v(-48.95, -28.56) * mm, "end": v(-48.95, -30.56) * mm});
            skLineSegment(sketch, "E208.0.19.0", {"start": v(-50.95, -32.56) * mm, "end": v(-48.95, -32.56) * mm});
            skLineSegment(sketch, "E208.0.19.1", {"start": v(-50.95, -32.56) * mm, "end": v(-50.95, -34.56) * mm});
            skLineSegment(sketch, "E208.0.19.2", {"start": v(-50.95, -34.56) * mm, "end": v(-48.95, -34.56) * mm});
            skLineSegment(sketch, "E208.0.19.3", {"start": v(-48.95, -32.56) * mm, "end": v(-48.95, -34.56) * mm});
            skLineSegment(sketch, "E208.0.20.0", {"start": v(-50.95, -36.56) * mm, "end": v(-48.95, -36.56) * mm});
            skLineSegment(sketch, "E208.0.20.1", {"start": v(-50.95, -36.56) * mm, "end": v(-50.95, -38.56) * mm});
            skLineSegment(sketch, "E208.0.20.2", {"start": v(-50.95, -38.56) * mm, "end": v(-48.95, -38.56) * mm});
            skLineSegment(sketch, "E208.0.20.3", {"start": v(-48.95, -36.56) * mm, "end": v(-48.95, -38.56) * mm});
            skLineSegment(sketch, "E208.0.21.0", {"start": v(-50.95, -40.56) * mm, "end": v(-48.95, -40.56) * mm});
            skLineSegment(sketch, "E208.0.21.1", {"start": v(-50.95, -40.56) * mm, "end": v(-50.95, -42.56) * mm});
            skLineSegment(sketch, "E208.0.21.2", {"start": v(-50.95, -42.56) * mm, "end": v(-48.95, -42.56) * mm});
            skLineSegment(sketch, "E208.0.21.3", {"start": v(-48.95, -40.56) * mm, "end": v(-48.95, -42.56) * mm});
            skLineSegment(sketch, "E208.1.0.0", {"start": v(-46.95, 43.44) * mm, "end": v(-44.95, 43.44) * mm});
            skLineSegment(sketch, "E208.1.0.1", {"start": v(-46.95, 43.44) * mm, "end": v(-46.95, 41.44) * mm});
            skLineSegment(sketch, "E208.1.0.2", {"start": v(-46.95, 41.44) * mm, "end": v(-44.95, 41.44) * mm});
            skLineSegment(sketch, "E208.1.0.3", {"start": v(-44.95, 43.44) * mm, "end": v(-44.95, 41.44) * mm});
            skLineSegment(sketch, "E208.1.1.0", {"start": v(-46.95, 39.44) * mm, "end": v(-44.95, 39.44) * mm});
            skLineSegment(sketch, "E208.1.1.1", {"start": v(-46.95, 39.44) * mm, "end": v(-46.95, 37.44) * mm});
            skLineSegment(sketch, "E208.1.1.2", {"start": v(-46.95, 37.44) * mm, "end": v(-44.95, 37.44) * mm});
            skLineSegment(sketch, "E208.1.1.3", {"start": v(-44.95, 39.44) * mm, "end": v(-44.95, 37.44) * mm});
            skLineSegment(sketch, "E208.1.2.0", {"start": v(-46.95, 35.44) * mm, "end": v(-44.95, 35.44) * mm});
            skLineSegment(sketch, "E208.1.2.1", {"start": v(-46.95, 35.44) * mm, "end": v(-46.95, 33.44) * mm});
            skLineSegment(sketch, "E208.1.2.2", {"start": v(-46.95, 33.44) * mm, "end": v(-44.95, 33.44) * mm});
            skLineSegment(sketch, "E208.1.2.3", {"start": v(-44.95, 35.44) * mm, "end": v(-44.95, 33.44) * mm});
            skLineSegment(sketch, "E208.1.3.0", {"start": v(-46.95, 31.44) * mm, "end": v(-44.95, 31.44) * mm});
            skLineSegment(sketch, "E208.1.3.1", {"start": v(-46.95, 31.44) * mm, "end": v(-46.95, 29.44) * mm});
            skLineSegment(sketch, "E208.1.3.2", {"start": v(-46.95, 29.44) * mm, "end": v(-44.95, 29.44) * mm});
            skLineSegment(sketch, "E208.1.3.3", {"start": v(-44.95, 31.44) * mm, "end": v(-44.95, 29.44) * mm});
            skLineSegment(sketch, "E208.1.4.0", {"start": v(-46.95, 27.44) * mm, "end": v(-44.95, 27.44) * mm});
            skLineSegment(sketch, "E208.1.4.1", {"start": v(-46.95, 27.44) * mm, "end": v(-46.95, 25.44) * mm});
            skLineSegment(sketch, "E208.1.4.2", {"start": v(-46.95, 25.44) * mm, "end": v(-44.95, 25.44) * mm});
            skLineSegment(sketch, "E208.1.4.3", {"start": v(-44.95, 27.44) * mm, "end": v(-44.95, 25.44) * mm});
            skLineSegment(sketch, "E208.1.5.0", {"start": v(-46.95, 23.44) * mm, "end": v(-44.95, 23.44) * mm});
            skLineSegment(sketch, "E208.1.5.1", {"start": v(-46.95, 23.44) * mm, "end": v(-46.95, 21.44) * mm});
            skLineSegment(sketch, "E208.1.5.2", {"start": v(-46.95, 21.44) * mm, "end": v(-44.95, 21.44) * mm});
            skLineSegment(sketch, "E208.1.5.3", {"start": v(-44.95, 23.44) * mm, "end": v(-44.95, 21.44) * mm});
            skLineSegment(sketch, "E208.1.6.0", {"start": v(-46.95, 19.44) * mm, "end": v(-44.95, 19.44) * mm});
            skLineSegment(sketch, "E208.1.6.1", {"start": v(-46.95, 19.44) * mm, "end": v(-46.95, 17.44) * mm});
            skLineSegment(sketch, "E208.1.6.2", {"start": v(-46.95, 17.44) * mm, "end": v(-44.95, 17.44) * mm});
            skLineSegment(sketch, "E208.1.6.3", {"start": v(-44.95, 19.44) * mm, "end": v(-44.95, 17.44) * mm});
            skLineSegment(sketch, "E208.1.7.0", {"start": v(-46.95, 15.44) * mm, "end": v(-44.95, 15.44) * mm});
            skLineSegment(sketch, "E208.1.7.1", {"start": v(-46.95, 15.44) * mm, "end": v(-46.95, 13.44) * mm});
            skLineSegment(sketch, "E208.1.7.2", {"start": v(-46.95, 13.44) * mm, "end": v(-44.95, 13.44) * mm});
            skLineSegment(sketch, "E208.1.7.3", {"start": v(-44.95, 15.44) * mm, "end": v(-44.95, 13.44) * mm});
            skLineSegment(sketch, "E208.1.8.0", {"start": v(-46.95, 11.44) * mm, "end": v(-44.95, 11.44) * mm});
            skLineSegment(sketch, "E208.1.8.1", {"start": v(-46.95, 11.44) * mm, "end": v(-46.95, 9.44) * mm});
            skLineSegment(sketch, "E208.1.8.2", {"start": v(-46.95, 9.44) * mm, "end": v(-44.95, 9.44) * mm});
            skLineSegment(sketch, "E208.1.8.3", {"start": v(-44.95, 11.44) * mm, "end": v(-44.95, 9.44) * mm});
            skLineSegment(sketch, "E208.1.9.0", {"start": v(-46.95, 7.44) * mm, "end": v(-44.95, 7.44) * mm});
            skLineSegment(sketch, "E208.1.9.1", {"start": v(-46.95, 7.44) * mm, "end": v(-46.95, 5.44) * mm});
            skLineSegment(sketch, "E208.1.9.2", {"start": v(-46.95, 5.44) * mm, "end": v(-44.95, 5.44) * mm});
            skLineSegment(sketch, "E208.1.9.3", {"start": v(-44.95, 7.44) * mm, "end": v(-44.95, 5.44) * mm});
            skLineSegment(sketch, "E208.1.10.0", {"start": v(-46.95, 3.44) * mm, "end": v(-44.95, 3.44) * mm});
            skLineSegment(sketch, "E208.1.10.1", {"start": v(-46.95, 3.44) * mm, "end": v(-46.95, 1.44) * mm});
            skLineSegment(sketch, "E208.1.10.2", {"start": v(-46.95, 1.44) * mm, "end": v(-44.95, 1.44) * mm});
            skLineSegment(sketch, "E208.1.10.3", {"start": v(-44.95, 3.44) * mm, "end": v(-44.95, 1.44) * mm});
            skLineSegment(sketch, "E208.1.11.0", {"start": v(-46.95, -0.56) * mm, "end": v(-44.95, -0.56) * mm});
            skLineSegment(sketch, "E208.1.11.1", {"start": v(-46.95, -0.56) * mm, "end": v(-46.95, -2.56) * mm});
            skLineSegment(sketch, "E208.1.11.2", {"start": v(-46.95, -2.56) * mm, "end": v(-44.95, -2.56) * mm});
            skLineSegment(sketch, "E208.1.11.3", {"start": v(-44.95, -0.56) * mm, "end": v(-44.95, -2.56) * mm});
            skLineSegment(sketch, "E208.1.12.0", {"start": v(-46.95, -4.56) * mm, "end": v(-44.95, -4.56) * mm});
            skLineSegment(sketch, "E208.1.12.1", {"start": v(-46.95, -4.56) * mm, "end": v(-46.95, -6.56) * mm});
            skLineSegment(sketch, "E208.1.12.2", {"start": v(-46.95, -6.56) * mm, "end": v(-44.95, -6.56) * mm});
            skLineSegment(sketch, "E208.1.12.3", {"start": v(-44.95, -4.56) * mm, "end": v(-44.95, -6.56) * mm});
            skLineSegment(sketch, "E208.1.13.0", {"start": v(-46.95, -8.56) * mm, "end": v(-44.95, -8.56) * mm});
            skLineSegment(sketch, "E208.1.13.1", {"start": v(-46.95, -8.56) * mm, "end": v(-46.95, -10.56) * mm});
            skLineSegment(sketch, "E208.1.13.2", {"start": v(-46.95, -10.56) * mm, "end": v(-44.95, -10.56) * mm});
            skLineSegment(sketch, "E208.1.13.3", {"start": v(-44.95, -8.56) * mm, "end": v(-44.95, -10.56) * mm});
            skLineSegment(sketch, "E208.1.14.0", {"start": v(-46.95, -12.56) * mm, "end": v(-44.95, -12.56) * mm});
            skLineSegment(sketch, "E208.1.14.1", {"start": v(-46.95, -12.56) * mm, "end": v(-46.95, -14.56) * mm});
            skLineSegment(sketch, "E208.1.14.2", {"start": v(-46.95, -14.56) * mm, "end": v(-44.95, -14.56) * mm});
            skLineSegment(sketch, "E208.1.14.3", {"start": v(-44.95, -12.56) * mm, "end": v(-44.95, -14.56) * mm});
            skLineSegment(sketch, "E208.1.15.0", {"start": v(-46.95, -16.56) * mm, "end": v(-44.95, -16.56) * mm});
            skLineSegment(sketch, "E208.1.15.1", {"start": v(-46.95, -16.56) * mm, "end": v(-46.95, -18.56) * mm});
            skLineSegment(sketch, "E208.1.15.2", {"start": v(-46.95, -18.56) * mm, "end": v(-44.95, -18.56) * mm});
            skLineSegment(sketch, "E208.1.15.3", {"start": v(-44.95, -16.56) * mm, "end": v(-44.95, -18.56) * mm});
            skLineSegment(sketch, "E208.1.16.0", {"start": v(-46.95, -20.56) * mm, "end": v(-44.95, -20.56) * mm});
            skLineSegment(sketch, "E208.1.16.1", {"start": v(-46.95, -20.56) * mm, "end": v(-46.95, -22.56) * mm});
            skLineSegment(sketch, "E208.1.16.2", {"start": v(-46.95, -22.56) * mm, "end": v(-44.95, -22.56) * mm});
            skLineSegment(sketch, "E208.1.16.3", {"start": v(-44.95, -20.56) * mm, "end": v(-44.95, -22.56) * mm});
            skLineSegment(sketch, "E208.1.17.0", {"start": v(-46.95, -24.56) * mm, "end": v(-44.95, -24.56) * mm});
            skLineSegment(sketch, "E208.1.17.1", {"start": v(-46.95, -24.56) * mm, "end": v(-46.95, -26.56) * mm});
            skLineSegment(sketch, "E208.1.17.2", {"start": v(-46.95, -26.56) * mm, "end": v(-44.95, -26.56) * mm});
            skLineSegment(sketch, "E208.1.17.3", {"start": v(-44.95, -24.56) * mm, "end": v(-44.95, -26.56) * mm});
            skLineSegment(sketch, "E208.1.18.0", {"start": v(-46.95, -28.56) * mm, "end": v(-44.95, -28.56) * mm});
            skLineSegment(sketch, "E208.1.18.1", {"start": v(-46.95, -28.56) * mm, "end": v(-46.95, -30.56) * mm});
            skLineSegment(sketch, "E208.1.18.2", {"start": v(-46.95, -30.56) * mm, "end": v(-44.95, -30.56) * mm});
            skLineSegment(sketch, "E208.1.18.3", {"start": v(-44.95, -28.56) * mm, "end": v(-44.95, -30.56) * mm});
            skLineSegment(sketch, "E208.1.19.0", {"start": v(-46.95, -32.56) * mm, "end": v(-44.95, -32.56) * mm});
            skLineSegment(sketch, "E208.1.19.1", {"start": v(-46.95, -32.56) * mm, "end": v(-46.95, -34.56) * mm});
            skLineSegment(sketch, "E208.1.19.2", {"start": v(-46.95, -34.56) * mm, "end": v(-44.95, -34.56) * mm});
            skLineSegment(sketch, "E208.1.19.3", {"start": v(-44.95, -32.56) * mm, "end": v(-44.95, -34.56) * mm});
            skLineSegment(sketch, "E208.1.20.0", {"start": v(-46.95, -36.56) * mm, "end": v(-44.95, -36.56) * mm});
            skLineSegment(sketch, "E208.1.20.1", {"start": v(-46.95, -36.56) * mm, "end": v(-46.95, -38.56) * mm});
            skLineSegment(sketch, "E208.1.20.2", {"start": v(-46.95, -38.56) * mm, "end": v(-44.95, -38.56) * mm});
            skLineSegment(sketch, "E208.1.20.3", {"start": v(-44.95, -36.56) * mm, "end": v(-44.95, -38.56) * mm});
            skLineSegment(sketch, "E208.1.21.0", {"start": v(-46.95, -40.56) * mm, "end": v(-44.95, -40.56) * mm});
            skLineSegment(sketch, "E208.1.21.1", {"start": v(-46.95, -40.56) * mm, "end": v(-46.95, -42.56) * mm});
            skLineSegment(sketch, "E208.1.21.2", {"start": v(-46.95, -42.56) * mm, "end": v(-44.95, -42.56) * mm});
            skLineSegment(sketch, "E208.1.21.3", {"start": v(-44.95, -40.56) * mm, "end": v(-44.95, -42.56) * mm});
            skLineSegment(sketch, "E208.2.0.0", {"start": v(-42.95, 43.44) * mm, "end": v(-40.95, 43.44) * mm});
            skLineSegment(sketch, "E208.2.0.1", {"start": v(-42.95, 43.44) * mm, "end": v(-42.95, 41.44) * mm});
            skLineSegment(sketch, "E208.2.0.2", {"start": v(-42.95, 41.44) * mm, "end": v(-40.95, 41.44) * mm});
            skLineSegment(sketch, "E208.2.0.3", {"start": v(-40.95, 43.44) * mm, "end": v(-40.95, 41.44) * mm});
            skLineSegment(sketch, "E208.2.1.0", {"start": v(-42.95, 39.44) * mm, "end": v(-40.95, 39.44) * mm});
            skLineSegment(sketch, "E208.2.1.1", {"start": v(-42.95, 39.44) * mm, "end": v(-42.95, 37.44) * mm});
            skLineSegment(sketch, "E208.2.1.2", {"start": v(-42.95, 37.44) * mm, "end": v(-40.95, 37.44) * mm});
            skLineSegment(sketch, "E208.2.1.3", {"start": v(-40.95, 39.44) * mm, "end": v(-40.95, 37.44) * mm});
            skLineSegment(sketch, "E208.2.2.0", {"start": v(-42.95, 35.44) * mm, "end": v(-40.95, 35.44) * mm});
            skLineSegment(sketch, "E208.2.2.1", {"start": v(-42.95, 35.44) * mm, "end": v(-42.95, 33.44) * mm});
            skLineSegment(sketch, "E208.2.2.2", {"start": v(-42.95, 33.44) * mm, "end": v(-40.95, 33.44) * mm});
            skLineSegment(sketch, "E208.2.2.3", {"start": v(-40.95, 35.44) * mm, "end": v(-40.95, 33.44) * mm});
            skLineSegment(sketch, "E208.2.3.0", {"start": v(-42.95, 31.44) * mm, "end": v(-40.95, 31.44) * mm});
            skLineSegment(sketch, "E208.2.3.1", {"start": v(-42.95, 31.44) * mm, "end": v(-42.95, 29.44) * mm});
            skLineSegment(sketch, "E208.2.3.2", {"start": v(-42.95, 29.44) * mm, "end": v(-40.95, 29.44) * mm});
            skLineSegment(sketch, "E208.2.3.3", {"start": v(-40.95, 31.44) * mm, "end": v(-40.95, 29.44) * mm});
            skLineSegment(sketch, "E208.2.4.0", {"start": v(-42.95, 27.44) * mm, "end": v(-40.95, 27.44) * mm});
            skLineSegment(sketch, "E208.2.4.1", {"start": v(-42.95, 27.44) * mm, "end": v(-42.95, 25.44) * mm});
            skLineSegment(sketch, "E208.2.4.2", {"start": v(-42.95, 25.44) * mm, "end": v(-40.95, 25.44) * mm});
            skLineSegment(sketch, "E208.2.4.3", {"start": v(-40.95, 27.44) * mm, "end": v(-40.95, 25.44) * mm});
            skLineSegment(sketch, "E208.2.5.0", {"start": v(-42.95, 23.44) * mm, "end": v(-40.95, 23.44) * mm});
            skLineSegment(sketch, "E208.2.5.1", {"start": v(-42.95, 23.44) * mm, "end": v(-42.95, 21.44) * mm});
            skLineSegment(sketch, "E208.2.5.2", {"start": v(-42.95, 21.44) * mm, "end": v(-40.95, 21.44) * mm});
            skLineSegment(sketch, "E208.2.5.3", {"start": v(-40.95, 23.44) * mm, "end": v(-40.95, 21.44) * mm});
            skLineSegment(sketch, "E208.2.6.0", {"start": v(-42.95, 19.44) * mm, "end": v(-40.95, 19.44) * mm});
            skLineSegment(sketch, "E208.2.6.1", {"start": v(-42.95, 19.44) * mm, "end": v(-42.95, 17.44) * mm});
            skLineSegment(sketch, "E208.2.6.2", {"start": v(-42.95, 17.44) * mm, "end": v(-40.95, 17.44) * mm});
            skLineSegment(sketch, "E208.2.6.3", {"start": v(-40.95, 19.44) * mm, "end": v(-40.95, 17.44) * mm});
            skLineSegment(sketch, "E208.2.7.0", {"start": v(-42.95, 15.44) * mm, "end": v(-40.95, 15.44) * mm});
            skLineSegment(sketch, "E208.2.7.1", {"start": v(-42.95, 15.44) * mm, "end": v(-42.95, 13.44) * mm});
            skLineSegment(sketch, "E208.2.7.2", {"start": v(-42.95, 13.44) * mm, "end": v(-40.95, 13.44) * mm});
            skLineSegment(sketch, "E208.2.7.3", {"start": v(-40.95, 15.44) * mm, "end": v(-40.95, 13.44) * mm});
            skLineSegment(sketch, "E208.2.8.0", {"start": v(-42.95, 11.44) * mm, "end": v(-40.95, 11.44) * mm});
            skLineSegment(sketch, "E208.2.8.1", {"start": v(-42.95, 11.44) * mm, "end": v(-42.95, 9.44) * mm});
            skLineSegment(sketch, "E208.2.8.2", {"start": v(-42.95, 9.44) * mm, "end": v(-40.95, 9.44) * mm});
            skLineSegment(sketch, "E208.2.8.3", {"start": v(-40.95, 11.44) * mm, "end": v(-40.95, 9.44) * mm});
            skLineSegment(sketch, "E208.2.9.0", {"start": v(-42.95, 7.44) * mm, "end": v(-40.95, 7.44) * mm});
            skLineSegment(sketch, "E208.2.9.1", {"start": v(-42.95, 7.44) * mm, "end": v(-42.95, 5.44) * mm});
            skLineSegment(sketch, "E208.2.9.2", {"start": v(-42.95, 5.44) * mm, "end": v(-40.95, 5.44) * mm});
            skLineSegment(sketch, "E208.2.9.3", {"start": v(-40.95, 7.44) * mm, "end": v(-40.95, 5.44) * mm});
            skLineSegment(sketch, "E208.2.10.0", {"start": v(-42.95, 3.44) * mm, "end": v(-40.95, 3.44) * mm});
            skLineSegment(sketch, "E208.2.10.1", {"start": v(-42.95, 3.44) * mm, "end": v(-42.95, 1.44) * mm});
            skLineSegment(sketch, "E208.2.10.2", {"start": v(-42.95, 1.44) * mm, "end": v(-40.95, 1.44) * mm});
            skLineSegment(sketch, "E208.2.10.3", {"start": v(-40.95, 3.44) * mm, "end": v(-40.95, 1.44) * mm});
            skLineSegment(sketch, "E208.2.11.0", {"start": v(-42.95, -0.56) * mm, "end": v(-40.95, -0.56) * mm});
            skLineSegment(sketch, "E208.2.11.1", {"start": v(-42.95, -0.56) * mm, "end": v(-42.95, -2.56) * mm});
            skLineSegment(sketch, "E208.2.11.2", {"start": v(-42.95, -2.56) * mm, "end": v(-40.95, -2.56) * mm});
            skLineSegment(sketch, "E208.2.11.3", {"start": v(-40.95, -0.56) * mm, "end": v(-40.95, -2.56) * mm});
            skLineSegment(sketch, "E208.2.12.0", {"start": v(-42.95, -4.56) * mm, "end": v(-40.95, -4.56) * mm});
            skLineSegment(sketch, "E208.2.12.1", {"start": v(-42.95, -4.56) * mm, "end": v(-42.95, -6.56) * mm});
            skLineSegment(sketch, "E208.2.12.2", {"start": v(-42.95, -6.56) * mm, "end": v(-40.95, -6.56) * mm});
            skLineSegment(sketch, "E208.2.12.3", {"start": v(-40.95, -4.56) * mm, "end": v(-40.95, -6.56) * mm});
            skLineSegment(sketch, "E208.2.13.0", {"start": v(-42.95, -8.56) * mm, "end": v(-40.95, -8.56) * mm});
            skLineSegment(sketch, "E208.2.13.1", {"start": v(-42.95, -8.56) * mm, "end": v(-42.95, -10.56) * mm});
            skLineSegment(sketch, "E208.2.13.2", {"start": v(-42.95, -10.56) * mm, "end": v(-40.95, -10.56) * mm});
            skLineSegment(sketch, "E208.2.13.3", {"start": v(-40.95, -8.56) * mm, "end": v(-40.95, -10.56) * mm});
            skLineSegment(sketch, "E208.2.14.0", {"start": v(-42.95, -12.56) * mm, "end": v(-40.95, -12.56) * mm});
            skLineSegment(sketch, "E208.2.14.1", {"start": v(-42.95, -12.56) * mm, "end": v(-42.95, -14.56) * mm});
            skLineSegment(sketch, "E208.2.14.2", {"start": v(-42.95, -14.56) * mm, "end": v(-40.95, -14.56) * mm});
            skLineSegment(sketch, "E208.2.14.3", {"start": v(-40.95, -12.56) * mm, "end": v(-40.95, -14.56) * mm});
            skLineSegment(sketch, "E208.2.15.0", {"start": v(-42.95, -16.56) * mm, "end": v(-40.95, -16.56) * mm});
            skLineSegment(sketch, "E208.2.15.1", {"start": v(-42.95, -16.56) * mm, "end": v(-42.95, -18.56) * mm});
            skLineSegment(sketch, "E208.2.15.2", {"start": v(-42.95, -18.56) * mm, "end": v(-40.95, -18.56) * mm});
            skLineSegment(sketch, "E208.2.15.3", {"start": v(-40.95, -16.56) * mm, "end": v(-40.95, -18.56) * mm});
            skLineSegment(sketch, "E208.2.16.0", {"start": v(-42.95, -20.56) * mm, "end": v(-40.95, -20.56) * mm});
            skLineSegment(sketch, "E208.2.16.1", {"start": v(-42.95, -20.56) * mm, "end": v(-42.95, -22.56) * mm});
            skLineSegment(sketch, "E208.2.16.2", {"start": v(-42.95, -22.56) * mm, "end": v(-40.95, -22.56) * mm});
            skLineSegment(sketch, "E208.2.16.3", {"start": v(-40.95, -20.56) * mm, "end": v(-40.95, -22.56) * mm});
            skLineSegment(sketch, "E208.2.17.0", {"start": v(-42.95, -24.56) * mm, "end": v(-40.95, -24.56) * mm});
            skLineSegment(sketch, "E208.2.17.1", {"start": v(-42.95, -24.56) * mm, "end": v(-42.95, -26.56) * mm});
            skLineSegment(sketch, "E208.2.17.2", {"start": v(-42.95, -26.56) * mm, "end": v(-40.95, -26.56) * mm});
            skLineSegment(sketch, "E208.2.17.3", {"start": v(-40.95, -24.56) * mm, "end": v(-40.95, -26.56) * mm});
            skLineSegment(sketch, "E208.2.18.0", {"start": v(-42.95, -28.56) * mm, "end": v(-40.95, -28.56) * mm});
            skLineSegment(sketch, "E208.2.18.1", {"start": v(-42.95, -28.56) * mm, "end": v(-42.95, -30.56) * mm});
            skLineSegment(sketch, "E208.2.18.2", {"start": v(-42.95, -30.56) * mm, "end": v(-40.95, -30.56) * mm});
            skLineSegment(sketch, "E208.2.18.3", {"start": v(-40.95, -28.56) * mm, "end": v(-40.95, -30.56) * mm});
            skLineSegment(sketch, "E208.2.19.0", {"start": v(-42.95, -32.56) * mm, "end": v(-40.95, -32.56) * mm});
            skLineSegment(sketch, "E208.2.19.1", {"start": v(-42.95, -32.56) * mm, "end": v(-42.95, -34.56) * mm});
            skLineSegment(sketch, "E208.2.19.2", {"start": v(-42.95, -34.56) * mm, "end": v(-40.95, -34.56) * mm});
            skLineSegment(sketch, "E208.2.19.3", {"start": v(-40.95, -32.56) * mm, "end": v(-40.95, -34.56) * mm});
            skLineSegment(sketch, "E208.2.20.0", {"start": v(-42.95, -36.56) * mm, "end": v(-40.95, -36.56) * mm});
            skLineSegment(sketch, "E208.2.20.1", {"start": v(-42.95, -36.56) * mm, "end": v(-42.95, -38.56) * mm});
            skLineSegment(sketch, "E208.2.20.2", {"start": v(-42.95, -38.56) * mm, "end": v(-40.95, -38.56) * mm});
            skLineSegment(sketch, "E208.2.20.3", {"start": v(-40.95, -36.56) * mm, "end": v(-40.95, -38.56) * mm});
            skLineSegment(sketch, "E208.2.21.0", {"start": v(-42.95, -40.56) * mm, "end": v(-40.95, -40.56) * mm});
            skLineSegment(sketch, "E208.2.21.1", {"start": v(-42.95, -40.56) * mm, "end": v(-42.95, -42.56) * mm});
            skLineSegment(sketch, "E208.2.21.2", {"start": v(-42.95, -42.56) * mm, "end": v(-40.95, -42.56) * mm});
            skLineSegment(sketch, "E208.2.21.3", {"start": v(-40.95, -40.56) * mm, "end": v(-40.95, -42.56) * mm});
            skLineSegment(sketch, "E208.3.0.0", {"start": v(-38.95, 43.44) * mm, "end": v(-36.95, 43.44) * mm});
            skLineSegment(sketch, "E208.3.0.1", {"start": v(-38.95, 43.44) * mm, "end": v(-38.95, 41.44) * mm});
            skLineSegment(sketch, "E208.3.0.2", {"start": v(-38.95, 41.44) * mm, "end": v(-36.95, 41.44) * mm});
            skLineSegment(sketch, "E208.3.0.3", {"start": v(-36.95, 43.44) * mm, "end": v(-36.95, 41.44) * mm});
            skLineSegment(sketch, "E208.3.1.0", {"start": v(-38.95, 39.44) * mm, "end": v(-36.95, 39.44) * mm});
            skLineSegment(sketch, "E208.3.1.1", {"start": v(-38.95, 39.44) * mm, "end": v(-38.95, 37.44) * mm});
            skLineSegment(sketch, "E208.3.1.2", {"start": v(-38.95, 37.44) * mm, "end": v(-36.95, 37.44) * mm});
            skLineSegment(sketch, "E208.3.1.3", {"start": v(-36.95, 39.44) * mm, "end": v(-36.95, 37.44) * mm});
            skLineSegment(sketch, "E208.3.2.0", {"start": v(-38.95, 35.44) * mm, "end": v(-36.95, 35.44) * mm});
            skLineSegment(sketch, "E208.3.2.1", {"start": v(-38.95, 35.44) * mm, "end": v(-38.95, 33.44) * mm});
            skLineSegment(sketch, "E208.3.2.2", {"start": v(-38.95, 33.44) * mm, "end": v(-36.95, 33.44) * mm});
            skLineSegment(sketch, "E208.3.2.3", {"start": v(-36.95, 35.44) * mm, "end": v(-36.95, 33.44) * mm});
            skLineSegment(sketch, "E208.3.3.0", {"start": v(-38.95, 31.44) * mm, "end": v(-36.95, 31.44) * mm});
            skLineSegment(sketch, "E208.3.3.1", {"start": v(-38.95, 31.44) * mm, "end": v(-38.95, 29.44) * mm});
            skLineSegment(sketch, "E208.3.3.2", {"start": v(-38.95, 29.44) * mm, "end": v(-36.95, 29.44) * mm});
            skLineSegment(sketch, "E208.3.3.3", {"start": v(-36.95, 31.44) * mm, "end": v(-36.95, 29.44) * mm});
            skLineSegment(sketch, "E208.3.4.0", {"start": v(-38.95, 27.44) * mm, "end": v(-36.95, 27.44) * mm});
            skLineSegment(sketch, "E208.3.4.1", {"start": v(-38.95, 27.44) * mm, "end": v(-38.95, 25.44) * mm});
            skLineSegment(sketch, "E208.3.4.2", {"start": v(-38.95, 25.44) * mm, "end": v(-36.95, 25.44) * mm});
            skLineSegment(sketch, "E208.3.4.3", {"start": v(-36.95, 27.44) * mm, "end": v(-36.95, 25.44) * mm});
            skLineSegment(sketch, "E208.3.5.0", {"start": v(-38.95, 23.44) * mm, "end": v(-36.95, 23.44) * mm});
            skLineSegment(sketch, "E208.3.5.1", {"start": v(-38.95, 23.44) * mm, "end": v(-38.95, 21.44) * mm});
            skLineSegment(sketch, "E208.3.5.2", {"start": v(-38.95, 21.44) * mm, "end": v(-36.95, 21.44) * mm});
            skLineSegment(sketch, "E208.3.5.3", {"start": v(-36.95, 23.44) * mm, "end": v(-36.95, 21.44) * mm});
            skLineSegment(sketch, "E208.3.6.0", {"start": v(-38.95, 19.44) * mm, "end": v(-36.95, 19.44) * mm});
            skLineSegment(sketch, "E208.3.6.1", {"start": v(-38.95, 19.44) * mm, "end": v(-38.95, 17.44) * mm});
            skLineSegment(sketch, "E208.3.6.2", {"start": v(-38.95, 17.44) * mm, "end": v(-36.95, 17.44) * mm});
            skLineSegment(sketch, "E208.3.6.3", {"start": v(-36.95, 19.44) * mm, "end": v(-36.95, 17.44) * mm});
            skLineSegment(sketch, "E208.3.7.0", {"start": v(-38.95, 15.44) * mm, "end": v(-36.95, 15.44) * mm});
            skLineSegment(sketch, "E208.3.7.1", {"start": v(-38.95, 15.44) * mm, "end": v(-38.95, 13.44) * mm});
            skLineSegment(sketch, "E208.3.7.2", {"start": v(-38.95, 13.44) * mm, "end": v(-36.95, 13.44) * mm});
            skLineSegment(sketch, "E208.3.7.3", {"start": v(-36.95, 15.44) * mm, "end": v(-36.95, 13.44) * mm});
            skLineSegment(sketch, "E208.3.8.0", {"start": v(-38.95, 11.44) * mm, "end": v(-36.95, 11.44) * mm});
            skLineSegment(sketch, "E208.3.8.1", {"start": v(-38.95, 11.44) * mm, "end": v(-38.95, 9.44) * mm});
            skLineSegment(sketch, "E208.3.8.2", {"start": v(-38.95, 9.44) * mm, "end": v(-36.95, 9.44) * mm});
            skLineSegment(sketch, "E208.3.8.3", {"start": v(-36.95, 11.44) * mm, "end": v(-36.95, 9.44) * mm});
            skLineSegment(sketch, "E208.3.9.0", {"start": v(-38.95, 7.44) * mm, "end": v(-36.95, 7.44) * mm});
            skLineSegment(sketch, "E208.3.9.1", {"start": v(-38.95, 7.44) * mm, "end": v(-38.95, 5.44) * mm});
            skLineSegment(sketch, "E208.3.9.2", {"start": v(-38.95, 5.44) * mm, "end": v(-36.95, 5.44) * mm});
            skLineSegment(sketch, "E208.3.9.3", {"start": v(-36.95, 7.44) * mm, "end": v(-36.95, 5.44) * mm});
            skLineSegment(sketch, "E208.3.10.0", {"start": v(-38.95, 3.44) * mm, "end": v(-36.95, 3.44) * mm});
            skLineSegment(sketch, "E208.3.10.1", {"start": v(-38.95, 3.44) * mm, "end": v(-38.95, 1.44) * mm});
            skLineSegment(sketch, "E208.3.10.2", {"start": v(-38.95, 1.44) * mm, "end": v(-36.95, 1.44) * mm});
            skLineSegment(sketch, "E208.3.10.3", {"start": v(-36.95, 3.44) * mm, "end": v(-36.95, 1.44) * mm});
            skLineSegment(sketch, "E208.3.11.0", {"start": v(-38.95, -0.56) * mm, "end": v(-36.95, -0.56) * mm});
            skLineSegment(sketch, "E208.3.11.1", {"start": v(-38.95, -0.56) * mm, "end": v(-38.95, -2.56) * mm});
            skLineSegment(sketch, "E208.3.11.2", {"start": v(-38.95, -2.56) * mm, "end": v(-36.95, -2.56) * mm});
            skLineSegment(sketch, "E208.3.11.3", {"start": v(-36.95, -0.56) * mm, "end": v(-36.95, -2.56) * mm});
            skLineSegment(sketch, "E208.3.12.0", {"start": v(-38.95, -4.56) * mm, "end": v(-36.95, -4.56) * mm});
            skLineSegment(sketch, "E208.3.12.1", {"start": v(-38.95, -4.56) * mm, "end": v(-38.95, -6.56) * mm});
            skLineSegment(sketch, "E208.3.12.2", {"start": v(-38.95, -6.56) * mm, "end": v(-36.95, -6.56) * mm});
            skLineSegment(sketch, "E208.3.12.3", {"start": v(-36.95, -4.56) * mm, "end": v(-36.95, -6.56) * mm});
            skLineSegment(sketch, "E208.3.13.0", {"start": v(-38.95, -8.56) * mm, "end": v(-36.95, -8.56) * mm});
            skLineSegment(sketch, "E208.3.13.1", {"start": v(-38.95, -8.56) * mm, "end": v(-38.95, -10.56) * mm});
            skLineSegment(sketch, "E208.3.13.2", {"start": v(-38.95, -10.56) * mm, "end": v(-36.95, -10.56) * mm});
            skLineSegment(sketch, "E208.3.13.3", {"start": v(-36.95, -8.56) * mm, "end": v(-36.95, -10.56) * mm});
            skLineSegment(sketch, "E208.3.14.0", {"start": v(-38.95, -12.56) * mm, "end": v(-36.95, -12.56) * mm});
            skLineSegment(sketch, "E208.3.14.1", {"start": v(-38.95, -12.56) * mm, "end": v(-38.95, -14.56) * mm});
            skLineSegment(sketch, "E208.3.14.2", {"start": v(-38.95, -14.56) * mm, "end": v(-36.95, -14.56) * mm});
            skLineSegment(sketch, "E208.3.14.3", {"start": v(-36.95, -12.56) * mm, "end": v(-36.95, -14.56) * mm});
            skLineSegment(sketch, "E208.3.15.0", {"start": v(-38.95, -16.56) * mm, "end": v(-36.95, -16.56) * mm});
            skLineSegment(sketch, "E208.3.15.1", {"start": v(-38.95, -16.56) * mm, "end": v(-38.95, -18.56) * mm});
            skLineSegment(sketch, "E208.3.15.2", {"start": v(-38.95, -18.56) * mm, "end": v(-36.95, -18.56) * mm});
            skLineSegment(sketch, "E208.3.15.3", {"start": v(-36.95, -16.56) * mm, "end": v(-36.95, -18.56) * mm});
            skLineSegment(sketch, "E208.3.16.0", {"start": v(-38.95, -20.56) * mm, "end": v(-36.95, -20.56) * mm});
            skLineSegment(sketch, "E208.3.16.1", {"start": v(-38.95, -20.56) * mm, "end": v(-38.95, -22.56) * mm});
            skLineSegment(sketch, "E208.3.16.2", {"start": v(-38.95, -22.56) * mm, "end": v(-36.95, -22.56) * mm});
            skLineSegment(sketch, "E208.3.16.3", {"start": v(-36.95, -20.56) * mm, "end": v(-36.95, -22.56) * mm});
            skLineSegment(sketch, "E208.3.17.0", {"start": v(-38.95, -24.56) * mm, "end": v(-36.95, -24.56) * mm});
            skLineSegment(sketch, "E208.3.17.1", {"start": v(-38.95, -24.56) * mm, "end": v(-38.95, -26.56) * mm});
            skLineSegment(sketch, "E208.3.17.2", {"start": v(-38.95, -26.56) * mm, "end": v(-36.95, -26.56) * mm});
            skLineSegment(sketch, "E208.3.17.3", {"start": v(-36.95, -24.56) * mm, "end": v(-36.95, -26.56) * mm});
            skLineSegment(sketch, "E208.3.18.0", {"start": v(-38.95, -28.56) * mm, "end": v(-36.95, -28.56) * mm});
            skLineSegment(sketch, "E208.3.18.1", {"start": v(-38.95, -28.56) * mm, "end": v(-38.95, -30.56) * mm});
            skLineSegment(sketch, "E208.3.18.2", {"start": v(-38.95, -30.56) * mm, "end": v(-36.95, -30.56) * mm});
            skLineSegment(sketch, "E208.3.18.3", {"start": v(-36.95, -28.56) * mm, "end": v(-36.95, -30.56) * mm});
            skLineSegment(sketch, "E208.3.19.0", {"start": v(-38.95, -32.56) * mm, "end": v(-36.95, -32.56) * mm});
            skLineSegment(sketch, "E208.3.19.1", {"start": v(-38.95, -32.56) * mm, "end": v(-38.95, -34.56) * mm});
            skLineSegment(sketch, "E208.3.19.2", {"start": v(-38.95, -34.56) * mm, "end": v(-36.95, -34.56) * mm});
            skLineSegment(sketch, "E208.3.19.3", {"start": v(-36.95, -32.56) * mm, "end": v(-36.95, -34.56) * mm});
            skLineSegment(sketch, "E208.3.20.0", {"start": v(-38.95, -36.56) * mm, "end": v(-36.95, -36.56) * mm});
            skLineSegment(sketch, "E208.3.20.1", {"start": v(-38.95, -36.56) * mm, "end": v(-38.95, -38.56) * mm});
            skLineSegment(sketch, "E208.3.20.2", {"start": v(-38.95, -38.56) * mm, "end": v(-36.95, -38.56) * mm});
            skLineSegment(sketch, "E208.3.20.3", {"start": v(-36.95, -36.56) * mm, "end": v(-36.95, -38.56) * mm});
            skLineSegment(sketch, "E208.3.21.0", {"start": v(-38.95, -40.56) * mm, "end": v(-36.95, -40.56) * mm});
            skLineSegment(sketch, "E208.3.21.1", {"start": v(-38.95, -40.56) * mm, "end": v(-38.95, -42.56) * mm});
            skLineSegment(sketch, "E208.3.21.2", {"start": v(-38.95, -42.56) * mm, "end": v(-36.95, -42.56) * mm});
            skLineSegment(sketch, "E208.3.21.3", {"start": v(-36.95, -40.56) * mm, "end": v(-36.95, -42.56) * mm});
            skLineSegment(sketch, "E208.4.0.0", {"start": v(-34.95, 43.44) * mm, "end": v(-32.95, 43.44) * mm});
            skLineSegment(sketch, "E208.4.0.1", {"start": v(-34.95, 43.44) * mm, "end": v(-34.95, 41.44) * mm});
            skLineSegment(sketch, "E208.4.0.2", {"start": v(-34.95, 41.44) * mm, "end": v(-32.95, 41.44) * mm});
            skLineSegment(sketch, "E208.4.0.3", {"start": v(-32.95, 43.44) * mm, "end": v(-32.95, 41.44) * mm});
            skLineSegment(sketch, "E208.4.1.0", {"start": v(-34.95, 39.44) * mm, "end": v(-32.95, 39.44) * mm});
            skLineSegment(sketch, "E208.4.1.1", {"start": v(-34.95, 39.44) * mm, "end": v(-34.95, 37.44) * mm});
            skLineSegment(sketch, "E208.4.1.2", {"start": v(-34.95, 37.44) * mm, "end": v(-32.95, 37.44) * mm});
            skLineSegment(sketch, "E208.4.1.3", {"start": v(-32.95, 39.44) * mm, "end": v(-32.95, 37.44) * mm});
            skLineSegment(sketch, "E208.4.2.0", {"start": v(-34.95, 35.44) * mm, "end": v(-32.95, 35.44) * mm});
            skLineSegment(sketch, "E208.4.2.1", {"start": v(-34.95, 35.44) * mm, "end": v(-34.95, 33.44) * mm});
            skLineSegment(sketch, "E208.4.2.2", {"start": v(-34.95, 33.44) * mm, "end": v(-32.95, 33.44) * mm});
            skLineSegment(sketch, "E208.4.2.3", {"start": v(-32.95, 35.44) * mm, "end": v(-32.95, 33.44) * mm});
            skLineSegment(sketch, "E208.4.3.0", {"start": v(-34.95, 31.44) * mm, "end": v(-32.95, 31.44) * mm});
            skLineSegment(sketch, "E208.4.3.1", {"start": v(-34.95, 31.44) * mm, "end": v(-34.95, 29.44) * mm});
            skLineSegment(sketch, "E208.4.3.2", {"start": v(-34.95, 29.44) * mm, "end": v(-32.95, 29.44) * mm});
            skLineSegment(sketch, "E208.4.3.3", {"start": v(-32.95, 31.44) * mm, "end": v(-32.95, 29.44) * mm});
            skLineSegment(sketch, "E208.4.4.0", {"start": v(-34.95, 27.44) * mm, "end": v(-32.95, 27.44) * mm});
            skLineSegment(sketch, "E208.4.4.1", {"start": v(-34.95, 27.44) * mm, "end": v(-34.95, 25.44) * mm});
            skLineSegment(sketch, "E208.4.4.2", {"start": v(-34.95, 25.44) * mm, "end": v(-32.95, 25.44) * mm});
            skLineSegment(sketch, "E208.4.4.3", {"start": v(-32.95, 27.44) * mm, "end": v(-32.95, 25.44) * mm});
            skLineSegment(sketch, "E208.4.5.0", {"start": v(-34.95, 23.44) * mm, "end": v(-32.95, 23.44) * mm});
            skLineSegment(sketch, "E208.4.5.1", {"start": v(-34.95, 23.44) * mm, "end": v(-34.95, 21.44) * mm});
            skLineSegment(sketch, "E208.4.5.2", {"start": v(-34.95, 21.44) * mm, "end": v(-32.95, 21.44) * mm});
            skLineSegment(sketch, "E208.4.5.3", {"start": v(-32.95, 23.44) * mm, "end": v(-32.95, 21.44) * mm});
            skLineSegment(sketch, "E208.4.6.0", {"start": v(-34.95, 19.44) * mm, "end": v(-32.95, 19.44) * mm});
            skLineSegment(sketch, "E208.4.6.1", {"start": v(-34.95, 19.44) * mm, "end": v(-34.95, 17.44) * mm});
            skLineSegment(sketch, "E208.4.6.2", {"start": v(-34.95, 17.44) * mm, "end": v(-32.95, 17.44) * mm});
            skLineSegment(sketch, "E208.4.6.3", {"start": v(-32.95, 19.44) * mm, "end": v(-32.95, 17.44) * mm});
            skLineSegment(sketch, "E208.4.7.0", {"start": v(-34.95, 15.44) * mm, "end": v(-32.95, 15.44) * mm});
            skLineSegment(sketch, "E208.4.7.1", {"start": v(-34.95, 15.44) * mm, "end": v(-34.95, 13.44) * mm});
            skLineSegment(sketch, "E208.4.7.2", {"start": v(-34.95, 13.44) * mm, "end": v(-32.95, 13.44) * mm});
            skLineSegment(sketch, "E208.4.7.3", {"start": v(-32.95, 15.44) * mm, "end": v(-32.95, 13.44) * mm});
            skLineSegment(sketch, "E208.4.8.0", {"start": v(-34.95, 11.44) * mm, "end": v(-32.95, 11.44) * mm});
            skLineSegment(sketch, "E208.4.8.1", {"start": v(-34.95, 11.44) * mm, "end": v(-34.95, 9.44) * mm});
            skLineSegment(sketch, "E208.4.8.2", {"start": v(-34.95, 9.44) * mm, "end": v(-32.95, 9.44) * mm});
            skLineSegment(sketch, "E208.4.8.3", {"start": v(-32.95, 11.44) * mm, "end": v(-32.95, 9.44) * mm});
            skLineSegment(sketch, "E208.4.9.0", {"start": v(-34.95, 7.44) * mm, "end": v(-32.95, 7.44) * mm});
            skLineSegment(sketch, "E208.4.9.1", {"start": v(-34.95, 7.44) * mm, "end": v(-34.95, 5.44) * mm});
            skLineSegment(sketch, "E208.4.9.2", {"start": v(-34.95, 5.44) * mm, "end": v(-32.95, 5.44) * mm});
            skLineSegment(sketch, "E208.4.9.3", {"start": v(-32.95, 7.44) * mm, "end": v(-32.95, 5.44) * mm});
            skLineSegment(sketch, "E208.4.10.0", {"start": v(-34.95, 3.44) * mm, "end": v(-32.95, 3.44) * mm});
            skLineSegment(sketch, "E208.4.10.1", {"start": v(-34.95, 3.44) * mm, "end": v(-34.95, 1.44) * mm});
            skLineSegment(sketch, "E208.4.10.2", {"start": v(-34.95, 1.44) * mm, "end": v(-32.95, 1.44) * mm});
            skLineSegment(sketch, "E208.4.10.3", {"start": v(-32.95, 3.44) * mm, "end": v(-32.95, 1.44) * mm});
            skLineSegment(sketch, "E208.4.11.0", {"start": v(-34.95, -0.56) * mm, "end": v(-32.95, -0.56) * mm});
            skLineSegment(sketch, "E208.4.11.1", {"start": v(-34.95, -0.56) * mm, "end": v(-34.95, -2.56) * mm});
            skLineSegment(sketch, "E208.4.11.2", {"start": v(-34.95, -2.56) * mm, "end": v(-32.95, -2.56) * mm});
            skLineSegment(sketch, "E208.4.11.3", {"start": v(-32.95, -0.56) * mm, "end": v(-32.95, -2.56) * mm});
            skLineSegment(sketch, "E208.4.12.0", {"start": v(-34.95, -4.56) * mm, "end": v(-32.95, -4.56) * mm});
            skLineSegment(sketch, "E208.4.12.1", {"start": v(-34.95, -4.56) * mm, "end": v(-34.95, -6.56) * mm});
            skLineSegment(sketch, "E208.4.12.2", {"start": v(-34.95, -6.56) * mm, "end": v(-32.95, -6.56) * mm});
            skLineSegment(sketch, "E208.4.12.3", {"start": v(-32.95, -4.56) * mm, "end": v(-32.95, -6.56) * mm});
            skLineSegment(sketch, "E208.4.13.0", {"start": v(-34.95, -8.56) * mm, "end": v(-32.95, -8.56) * mm});
            skLineSegment(sketch, "E208.4.13.1", {"start": v(-34.95, -8.56) * mm, "end": v(-34.95, -10.56) * mm});
            skLineSegment(sketch, "E208.4.13.2", {"start": v(-34.95, -10.56) * mm, "end": v(-32.95, -10.56) * mm});
            skLineSegment(sketch, "E208.4.13.3", {"start": v(-32.95, -8.56) * mm, "end": v(-32.95, -10.56) * mm});
            skLineSegment(sketch, "E208.4.14.0", {"start": v(-34.95, -12.56) * mm, "end": v(-32.95, -12.56) * mm});
            skLineSegment(sketch, "E208.4.14.1", {"start": v(-34.95, -12.56) * mm, "end": v(-34.95, -14.56) * mm});
            skLineSegment(sketch, "E208.4.14.2", {"start": v(-34.95, -14.56) * mm, "end": v(-32.95, -14.56) * mm});
            skLineSegment(sketch, "E208.4.14.3", {"start": v(-32.95, -12.56) * mm, "end": v(-32.95, -14.56) * mm});
            skLineSegment(sketch, "E208.4.15.0", {"start": v(-34.95, -16.56) * mm, "end": v(-32.95, -16.56) * mm});
            skLineSegment(sketch, "E208.4.15.1", {"start": v(-34.95, -16.56) * mm, "end": v(-34.95, -18.56) * mm});
            skLineSegment(sketch, "E208.4.15.2", {"start": v(-34.95, -18.56) * mm, "end": v(-32.95, -18.56) * mm});
            skLineSegment(sketch, "E208.4.15.3", {"start": v(-32.95, -16.56) * mm, "end": v(-32.95, -18.56) * mm});
            skLineSegment(sketch, "E208.4.16.0", {"start": v(-34.95, -20.56) * mm, "end": v(-32.95, -20.56) * mm});
            skLineSegment(sketch, "E208.4.16.1", {"start": v(-34.95, -20.56) * mm, "end": v(-34.95, -22.56) * mm});
            skLineSegment(sketch, "E208.4.16.2", {"start": v(-34.95, -22.56) * mm, "end": v(-32.95, -22.56) * mm});
            skLineSegment(sketch, "E208.4.16.3", {"start": v(-32.95, -20.56) * mm, "end": v(-32.95, -22.56) * mm});
            skLineSegment(sketch, "E208.4.17.0", {"start": v(-34.95, -24.56) * mm, "end": v(-32.95, -24.56) * mm});
            skLineSegment(sketch, "E208.4.17.1", {"start": v(-34.95, -24.56) * mm, "end": v(-34.95, -26.56) * mm});
            skLineSegment(sketch, "E208.4.17.2", {"start": v(-34.95, -26.56) * mm, "end": v(-32.95, -26.56) * mm});
            skLineSegment(sketch, "E208.4.17.3", {"start": v(-32.95, -24.56) * mm, "end": v(-32.95, -26.56) * mm});
            skLineSegment(sketch, "E208.4.18.0", {"start": v(-34.95, -28.56) * mm, "end": v(-32.95, -28.56) * mm});
            skLineSegment(sketch, "E208.4.18.1", {"start": v(-34.95, -28.56) * mm, "end": v(-34.95, -30.56) * mm});
            skLineSegment(sketch, "E208.4.18.2", {"start": v(-34.95, -30.56) * mm, "end": v(-32.95, -30.56) * mm});
            skLineSegment(sketch, "E208.4.18.3", {"start": v(-32.95, -28.56) * mm, "end": v(-32.95, -30.56) * mm});
            skLineSegment(sketch, "E208.4.19.0", {"start": v(-34.95, -32.56) * mm, "end": v(-32.95, -32.56) * mm});
            skLineSegment(sketch, "E208.4.19.1", {"start": v(-34.95, -32.56) * mm, "end": v(-34.95, -34.56) * mm});
            skLineSegment(sketch, "E208.4.19.2", {"start": v(-34.95, -34.56) * mm, "end": v(-32.95, -34.56) * mm});
            skLineSegment(sketch, "E208.4.19.3", {"start": v(-32.95, -32.56) * mm, "end": v(-32.95, -34.56) * mm});
            skLineSegment(sketch, "E208.4.20.0", {"start": v(-34.95, -36.56) * mm, "end": v(-32.95, -36.56) * mm});
            skLineSegment(sketch, "E208.4.20.1", {"start": v(-34.95, -36.56) * mm, "end": v(-34.95, -38.56) * mm});
            skLineSegment(sketch, "E208.4.20.2", {"start": v(-34.95, -38.56) * mm, "end": v(-32.95, -38.56) * mm});
            skLineSegment(sketch, "E208.4.20.3", {"start": v(-32.95, -36.56) * mm, "end": v(-32.95, -38.56) * mm});
            skLineSegment(sketch, "E208.4.21.0", {"start": v(-34.95, -40.56) * mm, "end": v(-32.95, -40.56) * mm});
            skLineSegment(sketch, "E208.4.21.1", {"start": v(-34.95, -40.56) * mm, "end": v(-34.95, -42.56) * mm});
            skLineSegment(sketch, "E208.4.21.2", {"start": v(-34.95, -42.56) * mm, "end": v(-32.95, -42.56) * mm});
            skLineSegment(sketch, "E208.4.21.3", {"start": v(-32.95, -40.56) * mm, "end": v(-32.95, -42.56) * mm});
            skLineSegment(sketch, "E208.5.0.0", {"start": v(-30.95, 43.44) * mm, "end": v(-28.95, 43.44) * mm});
            skLineSegment(sketch, "E208.5.0.1", {"start": v(-30.95, 43.44) * mm, "end": v(-30.95, 41.44) * mm});
            skLineSegment(sketch, "E208.5.0.2", {"start": v(-30.95, 41.44) * mm, "end": v(-28.95, 41.44) * mm});
            skLineSegment(sketch, "E208.5.0.3", {"start": v(-28.95, 43.44) * mm, "end": v(-28.95, 41.44) * mm});
            skLineSegment(sketch, "E208.5.1.0", {"start": v(-30.95, 39.44) * mm, "end": v(-28.95, 39.44) * mm});
            skLineSegment(sketch, "E208.5.1.1", {"start": v(-30.95, 39.44) * mm, "end": v(-30.95, 37.44) * mm});
            skLineSegment(sketch, "E208.5.1.2", {"start": v(-30.95, 37.44) * mm, "end": v(-28.95, 37.44) * mm});
            skLineSegment(sketch, "E208.5.1.3", {"start": v(-28.95, 39.44) * mm, "end": v(-28.95, 37.44) * mm});
            skLineSegment(sketch, "E208.5.2.0", {"start": v(-30.95, 35.44) * mm, "end": v(-28.95, 35.44) * mm});
            skLineSegment(sketch, "E208.5.2.1", {"start": v(-30.95, 35.44) * mm, "end": v(-30.95, 33.44) * mm});
            skLineSegment(sketch, "E208.5.2.2", {"start": v(-30.95, 33.44) * mm, "end": v(-28.95, 33.44) * mm});
            skLineSegment(sketch, "E208.5.2.3", {"start": v(-28.95, 35.44) * mm, "end": v(-28.95, 33.44) * mm});
            skLineSegment(sketch, "E208.5.3.0", {"start": v(-30.95, 31.44) * mm, "end": v(-28.95, 31.44) * mm});
            skLineSegment(sketch, "E208.5.3.1", {"start": v(-30.95, 31.44) * mm, "end": v(-30.95, 29.44) * mm});
            skLineSegment(sketch, "E208.5.3.2", {"start": v(-30.95, 29.44) * mm, "end": v(-28.95, 29.44) * mm});
            skLineSegment(sketch, "E208.5.3.3", {"start": v(-28.95, 31.44) * mm, "end": v(-28.95, 29.44) * mm});
            skLineSegment(sketch, "E208.5.4.0", {"start": v(-30.95, 27.44) * mm, "end": v(-28.95, 27.44) * mm});
            skLineSegment(sketch, "E208.5.4.1", {"start": v(-30.95, 27.44) * mm, "end": v(-30.95, 25.44) * mm});
            skLineSegment(sketch, "E208.5.4.2", {"start": v(-30.95, 25.44) * mm, "end": v(-28.95, 25.44) * mm});
            skLineSegment(sketch, "E208.5.4.3", {"start": v(-28.95, 27.44) * mm, "end": v(-28.95, 25.44) * mm});
            skLineSegment(sketch, "E208.5.5.0", {"start": v(-30.95, 23.44) * mm, "end": v(-28.95, 23.44) * mm});
            skLineSegment(sketch, "E208.5.5.1", {"start": v(-30.95, 23.44) * mm, "end": v(-30.95, 21.44) * mm});
            skLineSegment(sketch, "E208.5.5.2", {"start": v(-30.95, 21.44) * mm, "end": v(-28.95, 21.44) * mm});
            skLineSegment(sketch, "E208.5.5.3", {"start": v(-28.95, 23.44) * mm, "end": v(-28.95, 21.44) * mm});
            skLineSegment(sketch, "E208.5.6.0", {"start": v(-30.95, 19.44) * mm, "end": v(-28.95, 19.44) * mm});
            skLineSegment(sketch, "E208.5.6.1", {"start": v(-30.95, 19.44) * mm, "end": v(-30.95, 17.44) * mm});
            skLineSegment(sketch, "E208.5.6.2", {"start": v(-30.95, 17.44) * mm, "end": v(-28.95, 17.44) * mm});
            skLineSegment(sketch, "E208.5.6.3", {"start": v(-28.95, 19.44) * mm, "end": v(-28.95, 17.44) * mm});
            skLineSegment(sketch, "E208.5.7.0", {"start": v(-30.95, 15.44) * mm, "end": v(-28.95, 15.44) * mm});
            skLineSegment(sketch, "E208.5.7.1", {"start": v(-30.95, 15.44) * mm, "end": v(-30.95, 13.44) * mm});
            skLineSegment(sketch, "E208.5.7.2", {"start": v(-30.95, 13.44) * mm, "end": v(-28.95, 13.44) * mm});
            skLineSegment(sketch, "E208.5.7.3", {"start": v(-28.95, 15.44) * mm, "end": v(-28.95, 13.44) * mm});
            skLineSegment(sketch, "E208.5.8.0", {"start": v(-30.95, 11.44) * mm, "end": v(-28.95, 11.44) * mm});
            skLineSegment(sketch, "E208.5.8.1", {"start": v(-30.95, 11.44) * mm, "end": v(-30.95, 9.44) * mm});
            skLineSegment(sketch, "E208.5.8.2", {"start": v(-30.95, 9.44) * mm, "end": v(-28.95, 9.44) * mm});
            skLineSegment(sketch, "E208.5.8.3", {"start": v(-28.95, 11.44) * mm, "end": v(-28.95, 9.44) * mm});
            skLineSegment(sketch, "E208.5.9.0", {"start": v(-30.95, 7.44) * mm, "end": v(-28.95, 7.44) * mm});
            skLineSegment(sketch, "E208.5.9.1", {"start": v(-30.95, 7.44) * mm, "end": v(-30.95, 5.44) * mm});
            skLineSegment(sketch, "E208.5.9.2", {"start": v(-30.95, 5.44) * mm, "end": v(-28.95, 5.44) * mm});
            skLineSegment(sketch, "E208.5.9.3", {"start": v(-28.95, 7.44) * mm, "end": v(-28.95, 5.44) * mm});
            skLineSegment(sketch, "E208.5.10.0", {"start": v(-30.95, 3.44) * mm, "end": v(-28.95, 3.44) * mm});
            skLineSegment(sketch, "E208.5.10.1", {"start": v(-30.95, 3.44) * mm, "end": v(-30.95, 1.44) * mm});
            skLineSegment(sketch, "E208.5.10.2", {"start": v(-30.95, 1.44) * mm, "end": v(-28.95, 1.44) * mm});
            skLineSegment(sketch, "E208.5.10.3", {"start": v(-28.95, 3.44) * mm, "end": v(-28.95, 1.44) * mm});
            skLineSegment(sketch, "E208.5.11.0", {"start": v(-30.95, -0.56) * mm, "end": v(-28.95, -0.56) * mm});
            skLineSegment(sketch, "E208.5.11.1", {"start": v(-30.95, -0.56) * mm, "end": v(-30.95, -2.56) * mm});
            skLineSegment(sketch, "E208.5.11.2", {"start": v(-30.95, -2.56) * mm, "end": v(-28.95, -2.56) * mm});
            skLineSegment(sketch, "E208.5.11.3", {"start": v(-28.95, -0.56) * mm, "end": v(-28.95, -2.56) * mm});
            skLineSegment(sketch, "E208.5.12.0", {"start": v(-30.95, -4.56) * mm, "end": v(-28.95, -4.56) * mm});
            skLineSegment(sketch, "E208.5.12.1", {"start": v(-30.95, -4.56) * mm, "end": v(-30.95, -6.56) * mm});
            skLineSegment(sketch, "E208.5.12.2", {"start": v(-30.95, -6.56) * mm, "end": v(-28.95, -6.56) * mm});
            skLineSegment(sketch, "E208.5.12.3", {"start": v(-28.95, -4.56) * mm, "end": v(-28.95, -6.56) * mm});
            skLineSegment(sketch, "E208.5.13.0", {"start": v(-30.95, -8.56) * mm, "end": v(-28.95, -8.56) * mm});
            skLineSegment(sketch, "E208.5.13.1", {"start": v(-30.95, -8.56) * mm, "end": v(-30.95, -10.56) * mm});
            skLineSegment(sketch, "E208.5.13.2", {"start": v(-30.95, -10.56) * mm, "end": v(-28.95, -10.56) * mm});
            skLineSegment(sketch, "E208.5.13.3", {"start": v(-28.95, -8.56) * mm, "end": v(-28.95, -10.56) * mm});
            skLineSegment(sketch, "E208.5.14.0", {"start": v(-30.95, -12.56) * mm, "end": v(-28.95, -12.56) * mm});
            skLineSegment(sketch, "E208.5.14.1", {"start": v(-30.95, -12.56) * mm, "end": v(-30.95, -14.56) * mm});
            skLineSegment(sketch, "E208.5.14.2", {"start": v(-30.95, -14.56) * mm, "end": v(-28.95, -14.56) * mm});
            skLineSegment(sketch, "E208.5.14.3", {"start": v(-28.95, -12.56) * mm, "end": v(-28.95, -14.56) * mm});
            skLineSegment(sketch, "E208.5.15.0", {"start": v(-30.95, -16.56) * mm, "end": v(-28.95, -16.56) * mm});
            skLineSegment(sketch, "E208.5.15.1", {"start": v(-30.95, -16.56) * mm, "end": v(-30.95, -18.56) * mm});
            skLineSegment(sketch, "E208.5.15.2", {"start": v(-30.95, -18.56) * mm, "end": v(-28.95, -18.56) * mm});
            skLineSegment(sketch, "E208.5.15.3", {"start": v(-28.95, -16.56) * mm, "end": v(-28.95, -18.56) * mm});
            skLineSegment(sketch, "E208.5.16.0", {"start": v(-30.95, -20.56) * mm, "end": v(-28.95, -20.56) * mm});
            skLineSegment(sketch, "E208.5.16.1", {"start": v(-30.95, -20.56) * mm, "end": v(-30.95, -22.56) * mm});
            skLineSegment(sketch, "E208.5.16.2", {"start": v(-30.95, -22.56) * mm, "end": v(-28.95, -22.56) * mm});
            skLineSegment(sketch, "E208.5.16.3", {"start": v(-28.95, -20.56) * mm, "end": v(-28.95, -22.56) * mm});
            skLineSegment(sketch, "E208.5.17.0", {"start": v(-30.95, -24.56) * mm, "end": v(-28.95, -24.56) * mm});
            skLineSegment(sketch, "E208.5.17.1", {"start": v(-30.95, -24.56) * mm, "end": v(-30.95, -26.56) * mm});
            skLineSegment(sketch, "E208.5.17.2", {"start": v(-30.95, -26.56) * mm, "end": v(-28.95, -26.56) * mm});
            skLineSegment(sketch, "E208.5.17.3", {"start": v(-28.95, -24.56) * mm, "end": v(-28.95, -26.56) * mm});
            skLineSegment(sketch, "E208.5.18.0", {"start": v(-30.95, -28.56) * mm, "end": v(-28.95, -28.56) * mm});
            skLineSegment(sketch, "E208.5.18.1", {"start": v(-30.95, -28.56) * mm, "end": v(-30.95, -30.56) * mm});
            skLineSegment(sketch, "E208.5.18.2", {"start": v(-30.95, -30.56) * mm, "end": v(-28.95, -30.56) * mm});
            skLineSegment(sketch, "E208.5.18.3", {"start": v(-28.95, -28.56) * mm, "end": v(-28.95, -30.56) * mm});
            skLineSegment(sketch, "E208.5.19.0", {"start": v(-30.95, -32.56) * mm, "end": v(-28.95, -32.56) * mm});
            skLineSegment(sketch, "E208.5.19.1", {"start": v(-30.95, -32.56) * mm, "end": v(-30.95, -34.56) * mm});
            skLineSegment(sketch, "E208.5.19.2", {"start": v(-30.95, -34.56) * mm, "end": v(-28.95, -34.56) * mm});
            skLineSegment(sketch, "E208.5.19.3", {"start": v(-28.95, -32.56) * mm, "end": v(-28.95, -34.56) * mm});
            skLineSegment(sketch, "E208.5.20.0", {"start": v(-30.95, -36.56) * mm, "end": v(-28.95, -36.56) * mm});
            skLineSegment(sketch, "E208.5.20.1", {"start": v(-30.95, -36.56) * mm, "end": v(-30.95, -38.56) * mm});
            skLineSegment(sketch, "E208.5.20.2", {"start": v(-30.95, -38.56) * mm, "end": v(-28.95, -38.56) * mm});
            skLineSegment(sketch, "E208.5.20.3", {"start": v(-28.95, -36.56) * mm, "end": v(-28.95, -38.56) * mm});
            skLineSegment(sketch, "E208.5.21.0", {"start": v(-30.95, -40.56) * mm, "end": v(-28.95, -40.56) * mm});
            skLineSegment(sketch, "E208.5.21.1", {"start": v(-30.95, -40.56) * mm, "end": v(-30.95, -42.56) * mm});
            skLineSegment(sketch, "E208.5.21.2", {"start": v(-30.95, -42.56) * mm, "end": v(-28.95, -42.56) * mm});
            skLineSegment(sketch, "E208.5.21.3", {"start": v(-28.95, -40.56) * mm, "end": v(-28.95, -42.56) * mm});
            skLineSegment(sketch, "E208.6.0.0", {"start": v(-26.95, 43.44) * mm, "end": v(-24.95, 43.44) * mm});
            skLineSegment(sketch, "E208.6.0.1", {"start": v(-26.95, 43.44) * mm, "end": v(-26.95, 41.44) * mm});
            skLineSegment(sketch, "E208.6.0.2", {"start": v(-26.95, 41.44) * mm, "end": v(-24.95, 41.44) * mm});
            skLineSegment(sketch, "E208.6.0.3", {"start": v(-24.95, 43.44) * mm, "end": v(-24.95, 41.44) * mm});
            skLineSegment(sketch, "E208.6.1.0", {"start": v(-26.95, 39.44) * mm, "end": v(-24.95, 39.44) * mm});
            skLineSegment(sketch, "E208.6.1.1", {"start": v(-26.95, 39.44) * mm, "end": v(-26.95, 37.44) * mm});
            skLineSegment(sketch, "E208.6.1.2", {"start": v(-26.95, 37.44) * mm, "end": v(-24.95, 37.44) * mm});
            skLineSegment(sketch, "E208.6.1.3", {"start": v(-24.95, 39.44) * mm, "end": v(-24.95, 37.44) * mm});
            skLineSegment(sketch, "E208.6.2.0", {"start": v(-26.95, 35.44) * mm, "end": v(-24.95, 35.44) * mm});
            skLineSegment(sketch, "E208.6.2.1", {"start": v(-26.95, 35.44) * mm, "end": v(-26.95, 33.44) * mm});
            skLineSegment(sketch, "E208.6.2.2", {"start": v(-26.95, 33.44) * mm, "end": v(-24.95, 33.44) * mm});
            skLineSegment(sketch, "E208.6.2.3", {"start": v(-24.95, 35.44) * mm, "end": v(-24.95, 33.44) * mm});
            skLineSegment(sketch, "E208.6.3.0", {"start": v(-26.95, 31.44) * mm, "end": v(-24.95, 31.44) * mm});
            skLineSegment(sketch, "E208.6.3.1", {"start": v(-26.95, 31.44) * mm, "end": v(-26.95, 29.44) * mm});
            skLineSegment(sketch, "E208.6.3.2", {"start": v(-26.95, 29.44) * mm, "end": v(-24.95, 29.44) * mm});
            skLineSegment(sketch, "E208.6.3.3", {"start": v(-24.95, 31.44) * mm, "end": v(-24.95, 29.44) * mm});
            skLineSegment(sketch, "E208.6.4.0", {"start": v(-26.95, 27.44) * mm, "end": v(-24.95, 27.44) * mm});
            skLineSegment(sketch, "E208.6.4.1", {"start": v(-26.95, 27.44) * mm, "end": v(-26.95, 25.44) * mm});
            skLineSegment(sketch, "E208.6.4.2", {"start": v(-26.95, 25.44) * mm, "end": v(-24.95, 25.44) * mm});
            skLineSegment(sketch, "E208.6.4.3", {"start": v(-24.95, 27.44) * mm, "end": v(-24.95, 25.44) * mm});
            skLineSegment(sketch, "E208.6.5.0", {"start": v(-26.95, 23.44) * mm, "end": v(-24.95, 23.44) * mm});
            skLineSegment(sketch, "E208.6.5.1", {"start": v(-26.95, 23.44) * mm, "end": v(-26.95, 21.44) * mm});
            skLineSegment(sketch, "E208.6.5.2", {"start": v(-26.95, 21.44) * mm, "end": v(-24.95, 21.44) * mm});
            skLineSegment(sketch, "E208.6.5.3", {"start": v(-24.95, 23.44) * mm, "end": v(-24.95, 21.44) * mm});
            skLineSegment(sketch, "E208.6.6.0", {"start": v(-26.95, 19.44) * mm, "end": v(-24.95, 19.44) * mm});
            skLineSegment(sketch, "E208.6.6.1", {"start": v(-26.95, 19.44) * mm, "end": v(-26.95, 17.44) * mm});
            skLineSegment(sketch, "E208.6.6.2", {"start": v(-26.95, 17.44) * mm, "end": v(-24.95, 17.44) * mm});
            skLineSegment(sketch, "E208.6.6.3", {"start": v(-24.95, 19.44) * mm, "end": v(-24.95, 17.44) * mm});
            skLineSegment(sketch, "E208.6.7.0", {"start": v(-26.95, 15.44) * mm, "end": v(-24.95, 15.44) * mm});
            skLineSegment(sketch, "E208.6.7.1", {"start": v(-26.95, 15.44) * mm, "end": v(-26.95, 13.44) * mm});
            skLineSegment(sketch, "E208.6.7.2", {"start": v(-26.95, 13.44) * mm, "end": v(-24.95, 13.44) * mm});
            skLineSegment(sketch, "E208.6.7.3", {"start": v(-24.95, 15.44) * mm, "end": v(-24.95, 13.44) * mm});
            skLineSegment(sketch, "E208.6.8.0", {"start": v(-26.95, 11.44) * mm, "end": v(-24.95, 11.44) * mm});
            skLineSegment(sketch, "E208.6.8.1", {"start": v(-26.95, 11.44) * mm, "end": v(-26.95, 9.44) * mm});
            skLineSegment(sketch, "E208.6.8.2", {"start": v(-26.95, 9.44) * mm, "end": v(-24.95, 9.44) * mm});
            skLineSegment(sketch, "E208.6.8.3", {"start": v(-24.95, 11.44) * mm, "end": v(-24.95, 9.44) * mm});
            skLineSegment(sketch, "E208.6.9.0", {"start": v(-26.95, 7.44) * mm, "end": v(-24.95, 7.44) * mm});
            skLineSegment(sketch, "E208.6.9.1", {"start": v(-26.95, 7.44) * mm, "end": v(-26.95, 5.44) * mm});
            skLineSegment(sketch, "E208.6.9.2", {"start": v(-26.95, 5.44) * mm, "end": v(-24.95, 5.44) * mm});
            skLineSegment(sketch, "E208.6.9.3", {"start": v(-24.95, 7.44) * mm, "end": v(-24.95, 5.44) * mm});
            skLineSegment(sketch, "E208.6.10.0", {"start": v(-26.95, 3.44) * mm, "end": v(-24.95, 3.44) * mm});
            skLineSegment(sketch, "E208.6.10.1", {"start": v(-26.95, 3.44) * mm, "end": v(-26.95, 1.44) * mm});
            skLineSegment(sketch, "E208.6.10.2", {"start": v(-26.95, 1.44) * mm, "end": v(-24.95, 1.44) * mm});
            skLineSegment(sketch, "E208.6.10.3", {"start": v(-24.95, 3.44) * mm, "end": v(-24.95, 1.44) * mm});
            skLineSegment(sketch, "E208.6.11.0", {"start": v(-26.95, -0.56) * mm, "end": v(-24.95, -0.56) * mm});
            skLineSegment(sketch, "E208.6.11.1", {"start": v(-26.95, -0.56) * mm, "end": v(-26.95, -2.56) * mm});
            skLineSegment(sketch, "E208.6.11.2", {"start": v(-26.95, -2.56) * mm, "end": v(-24.95, -2.56) * mm});
            skLineSegment(sketch, "E208.6.11.3", {"start": v(-24.95, -0.56) * mm, "end": v(-24.95, -2.56) * mm});
            skLineSegment(sketch, "E208.6.12.0", {"start": v(-26.95, -4.56) * mm, "end": v(-24.95, -4.56) * mm});
            skLineSegment(sketch, "E208.6.12.1", {"start": v(-26.95, -4.56) * mm, "end": v(-26.95, -6.56) * mm});
            skLineSegment(sketch, "E208.6.12.2", {"start": v(-26.95, -6.56) * mm, "end": v(-24.95, -6.56) * mm});
            skLineSegment(sketch, "E208.6.12.3", {"start": v(-24.95, -4.56) * mm, "end": v(-24.95, -6.56) * mm});
            skLineSegment(sketch, "E208.6.13.0", {"start": v(-26.95, -8.56) * mm, "end": v(-24.95, -8.56) * mm});
            skLineSegment(sketch, "E208.6.13.1", {"start": v(-26.95, -8.56) * mm, "end": v(-26.95, -10.56) * mm});
            skLineSegment(sketch, "E208.6.13.2", {"start": v(-26.95, -10.56) * mm, "end": v(-24.95, -10.56) * mm});
            skLineSegment(sketch, "E208.6.13.3", {"start": v(-24.95, -8.56) * mm, "end": v(-24.95, -10.56) * mm});
            skLineSegment(sketch, "E208.6.14.0", {"start": v(-26.95, -12.56) * mm, "end": v(-24.95, -12.56) * mm});
            skLineSegment(sketch, "E208.6.14.1", {"start": v(-26.95, -12.56) * mm, "end": v(-26.95, -14.56) * mm});
            skLineSegment(sketch, "E208.6.14.2", {"start": v(-26.95, -14.56) * mm, "end": v(-24.95, -14.56) * mm});
            skLineSegment(sketch, "E208.6.14.3", {"start": v(-24.95, -12.56) * mm, "end": v(-24.95, -14.56) * mm});
            skLineSegment(sketch, "E208.6.15.0", {"start": v(-26.95, -16.56) * mm, "end": v(-24.95, -16.56) * mm});
            skLineSegment(sketch, "E208.6.15.1", {"start": v(-26.95, -16.56) * mm, "end": v(-26.95, -18.56) * mm});
            skLineSegment(sketch, "E208.6.15.2", {"start": v(-26.95, -18.56) * mm, "end": v(-24.95, -18.56) * mm});
            skLineSegment(sketch, "E208.6.15.3", {"start": v(-24.95, -16.56) * mm, "end": v(-24.95, -18.56) * mm});
            skLineSegment(sketch, "E208.6.16.0", {"start": v(-26.95, -20.56) * mm, "end": v(-24.95, -20.56) * mm});
            skLineSegment(sketch, "E208.6.16.1", {"start": v(-26.95, -20.56) * mm, "end": v(-26.95, -22.56) * mm});
            skLineSegment(sketch, "E208.6.16.2", {"start": v(-26.95, -22.56) * mm, "end": v(-24.95, -22.56) * mm});
            skLineSegment(sketch, "E208.6.16.3", {"start": v(-24.95, -20.56) * mm, "end": v(-24.95, -22.56) * mm});
            skLineSegment(sketch, "E208.6.17.0", {"start": v(-26.95, -24.56) * mm, "end": v(-24.95, -24.56) * mm});
            skLineSegment(sketch, "E208.6.17.1", {"start": v(-26.95, -24.56) * mm, "end": v(-26.95, -26.56) * mm});
            skLineSegment(sketch, "E208.6.17.2", {"start": v(-26.95, -26.56) * mm, "end": v(-24.95, -26.56) * mm});
            skLineSegment(sketch, "E208.6.17.3", {"start": v(-24.95, -24.56) * mm, "end": v(-24.95, -26.56) * mm});
            skLineSegment(sketch, "E208.6.18.0", {"start": v(-26.95, -28.56) * mm, "end": v(-24.95, -28.56) * mm});
            skLineSegment(sketch, "E208.6.18.1", {"start": v(-26.95, -28.56) * mm, "end": v(-26.95, -30.56) * mm});
            skLineSegment(sketch, "E208.6.18.2", {"start": v(-26.95, -30.56) * mm, "end": v(-24.95, -30.56) * mm});
            skLineSegment(sketch, "E208.6.18.3", {"start": v(-24.95, -28.56) * mm, "end": v(-24.95, -30.56) * mm});
            skLineSegment(sketch, "E208.6.19.0", {"start": v(-26.95, -32.56) * mm, "end": v(-24.95, -32.56) * mm});
            skLineSegment(sketch, "E208.6.19.1", {"start": v(-26.95, -32.56) * mm, "end": v(-26.95, -34.56) * mm});
            skLineSegment(sketch, "E208.6.19.2", {"start": v(-26.95, -34.56) * mm, "end": v(-24.95, -34.56) * mm});
            skLineSegment(sketch, "E208.6.19.3", {"start": v(-24.95, -32.56) * mm, "end": v(-24.95, -34.56) * mm});
            skLineSegment(sketch, "E208.6.20.0", {"start": v(-26.95, -36.56) * mm, "end": v(-24.95, -36.56) * mm});
            skLineSegment(sketch, "E208.6.20.1", {"start": v(-26.95, -36.56) * mm, "end": v(-26.95, -38.56) * mm});
            skLineSegment(sketch, "E208.6.20.2", {"start": v(-26.95, -38.56) * mm, "end": v(-24.95, -38.56) * mm});
            skLineSegment(sketch, "E208.6.20.3", {"start": v(-24.95, -36.56) * mm, "end": v(-24.95, -38.56) * mm});
            skLineSegment(sketch, "E208.6.21.0", {"start": v(-26.95, -40.56) * mm, "end": v(-24.95, -40.56) * mm});
            skLineSegment(sketch, "E208.6.21.1", {"start": v(-26.95, -40.56) * mm, "end": v(-26.95, -42.56) * mm});
            skLineSegment(sketch, "E208.6.21.2", {"start": v(-26.95, -42.56) * mm, "end": v(-24.95, -42.56) * mm});
            skLineSegment(sketch, "E208.6.21.3", {"start": v(-24.95, -40.56) * mm, "end": v(-24.95, -42.56) * mm});
            skLineSegment(sketch, "E208.7.0.0", {"start": v(-22.95, 43.44) * mm, "end": v(-20.95, 43.44) * mm});
            skLineSegment(sketch, "E208.7.0.1", {"start": v(-22.95, 43.44) * mm, "end": v(-22.95, 41.44) * mm});
            skLineSegment(sketch, "E208.7.0.2", {"start": v(-22.95, 41.44) * mm, "end": v(-20.95, 41.44) * mm});
            skLineSegment(sketch, "E208.7.0.3", {"start": v(-20.95, 43.44) * mm, "end": v(-20.95, 41.44) * mm});
            skLineSegment(sketch, "E208.7.1.0", {"start": v(-22.95, 39.44) * mm, "end": v(-20.95, 39.44) * mm});
            skLineSegment(sketch, "E208.7.1.1", {"start": v(-22.95, 39.44) * mm, "end": v(-22.95, 37.44) * mm});
            skLineSegment(sketch, "E208.7.1.2", {"start": v(-22.95, 37.44) * mm, "end": v(-20.95, 37.44) * mm});
            skLineSegment(sketch, "E208.7.1.3", {"start": v(-20.95, 39.44) * mm, "end": v(-20.95, 37.44) * mm});
            skLineSegment(sketch, "E208.7.2.0", {"start": v(-22.95, 35.44) * mm, "end": v(-20.95, 35.44) * mm});
            skLineSegment(sketch, "E208.7.2.1", {"start": v(-22.95, 35.44) * mm, "end": v(-22.95, 33.44) * mm});
            skLineSegment(sketch, "E208.7.2.2", {"start": v(-22.95, 33.44) * mm, "end": v(-20.95, 33.44) * mm});
            skLineSegment(sketch, "E208.7.2.3", {"start": v(-20.95, 35.44) * mm, "end": v(-20.95, 33.44) * mm});
            skLineSegment(sketch, "E208.7.3.0", {"start": v(-22.95, 31.44) * mm, "end": v(-20.95, 31.44) * mm});
            skLineSegment(sketch, "E208.7.3.1", {"start": v(-22.95, 31.44) * mm, "end": v(-22.95, 29.44) * mm});
            skLineSegment(sketch, "E208.7.3.2", {"start": v(-22.95, 29.44) * mm, "end": v(-20.95, 29.44) * mm});
            skLineSegment(sketch, "E208.7.3.3", {"start": v(-20.95, 31.44) * mm, "end": v(-20.95, 29.44) * mm});
            skLineSegment(sketch, "E208.7.4.0", {"start": v(-22.95, 27.44) * mm, "end": v(-20.95, 27.44) * mm});
            skLineSegment(sketch, "E208.7.4.1", {"start": v(-22.95, 27.44) * mm, "end": v(-22.95, 25.44) * mm});
            skLineSegment(sketch, "E208.7.4.2", {"start": v(-22.95, 25.44) * mm, "end": v(-20.95, 25.44) * mm});
            skLineSegment(sketch, "E208.7.4.3", {"start": v(-20.95, 27.44) * mm, "end": v(-20.95, 25.44) * mm});
            skLineSegment(sketch, "E208.7.5.0", {"start": v(-22.95, 23.44) * mm, "end": v(-20.95, 23.44) * mm});
            skLineSegment(sketch, "E208.7.5.1", {"start": v(-22.95, 23.44) * mm, "end": v(-22.95, 21.44) * mm});
            skLineSegment(sketch, "E208.7.5.2", {"start": v(-22.95, 21.44) * mm, "end": v(-20.95, 21.44) * mm});
            skLineSegment(sketch, "E208.7.5.3", {"start": v(-20.95, 23.44) * mm, "end": v(-20.95, 21.44) * mm});
            skLineSegment(sketch, "E208.7.6.0", {"start": v(-22.95, 19.44) * mm, "end": v(-20.95, 19.44) * mm});
            skLineSegment(sketch, "E208.7.6.1", {"start": v(-22.95, 19.44) * mm, "end": v(-22.95, 17.44) * mm});
            skLineSegment(sketch, "E208.7.6.2", {"start": v(-22.95, 17.44) * mm, "end": v(-20.95, 17.44) * mm});
            skLineSegment(sketch, "E208.7.6.3", {"start": v(-20.95, 19.44) * mm, "end": v(-20.95, 17.44) * mm});
            skLineSegment(sketch, "E208.7.7.0", {"start": v(-22.95, 15.44) * mm, "end": v(-20.95, 15.44) * mm});
            skLineSegment(sketch, "E208.7.7.1", {"start": v(-22.95, 15.44) * mm, "end": v(-22.95, 13.44) * mm});
            skLineSegment(sketch, "E208.7.7.2", {"start": v(-22.95, 13.44) * mm, "end": v(-20.95, 13.44) * mm});
            skLineSegment(sketch, "E208.7.7.3", {"start": v(-20.95, 15.44) * mm, "end": v(-20.95, 13.44) * mm});
            skLineSegment(sketch, "E208.7.8.0", {"start": v(-22.95, 11.44) * mm, "end": v(-20.95, 11.44) * mm});
            skLineSegment(sketch, "E208.7.8.1", {"start": v(-22.95, 11.44) * mm, "end": v(-22.95, 9.44) * mm});
            skLineSegment(sketch, "E208.7.8.2", {"start": v(-22.95, 9.44) * mm, "end": v(-20.95, 9.44) * mm});
            skLineSegment(sketch, "E208.7.8.3", {"start": v(-20.95, 11.44) * mm, "end": v(-20.95, 9.44) * mm});
            skLineSegment(sketch, "E208.7.9.0", {"start": v(-22.95, 7.44) * mm, "end": v(-20.95, 7.44) * mm});
            skLineSegment(sketch, "E208.7.9.1", {"start": v(-22.95, 7.44) * mm, "end": v(-22.95, 5.44) * mm});
            skLineSegment(sketch, "E208.7.9.2", {"start": v(-22.95, 5.44) * mm, "end": v(-20.95, 5.44) * mm});
            skLineSegment(sketch, "E208.7.9.3", {"start": v(-20.95, 7.44) * mm, "end": v(-20.95, 5.44) * mm});
            skLineSegment(sketch, "E208.7.10.0", {"start": v(-22.95, 3.44) * mm, "end": v(-20.95, 3.44) * mm});
            skLineSegment(sketch, "E208.7.10.1", {"start": v(-22.95, 3.44) * mm, "end": v(-22.95, 1.44) * mm});
            skLineSegment(sketch, "E208.7.10.2", {"start": v(-22.95, 1.44) * mm, "end": v(-20.95, 1.44) * mm});
            skLineSegment(sketch, "E208.7.10.3", {"start": v(-20.95, 3.44) * mm, "end": v(-20.95, 1.44) * mm});
            skLineSegment(sketch, "E208.7.11.0", {"start": v(-22.95, -0.56) * mm, "end": v(-20.95, -0.56) * mm});
            skLineSegment(sketch, "E208.7.11.1", {"start": v(-22.95, -0.56) * mm, "end": v(-22.95, -2.56) * mm});
            skLineSegment(sketch, "E208.7.11.2", {"start": v(-22.95, -2.56) * mm, "end": v(-20.95, -2.56) * mm});
            skLineSegment(sketch, "E208.7.11.3", {"start": v(-20.95, -0.56) * mm, "end": v(-20.95, -2.56) * mm});
            skLineSegment(sketch, "E208.7.12.0", {"start": v(-22.95, -4.56) * mm, "end": v(-20.95, -4.56) * mm});
            skLineSegment(sketch, "E208.7.12.1", {"start": v(-22.95, -4.56) * mm, "end": v(-22.95, -6.56) * mm});
            skLineSegment(sketch, "E208.7.12.2", {"start": v(-22.95, -6.56) * mm, "end": v(-20.95, -6.56) * mm});
            skLineSegment(sketch, "E208.7.12.3", {"start": v(-20.95, -4.56) * mm, "end": v(-20.95, -6.56) * mm});
            skLineSegment(sketch, "E208.7.13.0", {"start": v(-22.95, -8.56) * mm, "end": v(-20.95, -8.56) * mm});
            skLineSegment(sketch, "E208.7.13.1", {"start": v(-22.95, -8.56) * mm, "end": v(-22.95, -10.56) * mm});
            skLineSegment(sketch, "E208.7.13.2", {"start": v(-22.95, -10.56) * mm, "end": v(-20.95, -10.56) * mm});
            skLineSegment(sketch, "E208.7.13.3", {"start": v(-20.95, -8.56) * mm, "end": v(-20.95, -10.56) * mm});
            skLineSegment(sketch, "E208.7.14.0", {"start": v(-22.95, -12.56) * mm, "end": v(-20.95, -12.56) * mm});
            skLineSegment(sketch, "E208.7.14.1", {"start": v(-22.95, -12.56) * mm, "end": v(-22.95, -14.56) * mm});
            skLineSegment(sketch, "E208.7.14.2", {"start": v(-22.95, -14.56) * mm, "end": v(-20.95, -14.56) * mm});
            skLineSegment(sketch, "E208.7.14.3", {"start": v(-20.95, -12.56) * mm, "end": v(-20.95, -14.56) * mm});
            skLineSegment(sketch, "E208.7.15.0", {"start": v(-22.95, -16.56) * mm, "end": v(-20.95, -16.56) * mm});
            skLineSegment(sketch, "E208.7.15.1", {"start": v(-22.95, -16.56) * mm, "end": v(-22.95, -18.56) * mm});
            skLineSegment(sketch, "E208.7.15.2", {"start": v(-22.95, -18.56) * mm, "end": v(-20.95, -18.56) * mm});
            skLineSegment(sketch, "E208.7.15.3", {"start": v(-20.95, -16.56) * mm, "end": v(-20.95, -18.56) * mm});
            skLineSegment(sketch, "E208.7.16.0", {"start": v(-22.95, -20.56) * mm, "end": v(-20.95, -20.56) * mm});
            skLineSegment(sketch, "E208.7.16.1", {"start": v(-22.95, -20.56) * mm, "end": v(-22.95, -22.56) * mm});
            skLineSegment(sketch, "E208.7.16.2", {"start": v(-22.95, -22.56) * mm, "end": v(-20.95, -22.56) * mm});
            skLineSegment(sketch, "E208.7.16.3", {"start": v(-20.95, -20.56) * mm, "end": v(-20.95, -22.56) * mm});
            skLineSegment(sketch, "E208.7.17.0", {"start": v(-22.95, -24.56) * mm, "end": v(-20.95, -24.56) * mm});
            skLineSegment(sketch, "E208.7.17.1", {"start": v(-22.95, -24.56) * mm, "end": v(-22.95, -26.56) * mm});
            skLineSegment(sketch, "E208.7.17.2", {"start": v(-22.95, -26.56) * mm, "end": v(-20.95, -26.56) * mm});
            skLineSegment(sketch, "E208.7.17.3", {"start": v(-20.95, -24.56) * mm, "end": v(-20.95, -26.56) * mm});
            skLineSegment(sketch, "E208.7.18.0", {"start": v(-22.95, -28.56) * mm, "end": v(-20.95, -28.56) * mm});
            skLineSegment(sketch, "E208.7.18.1", {"start": v(-22.95, -28.56) * mm, "end": v(-22.95, -30.56) * mm});
            skLineSegment(sketch, "E208.7.18.2", {"start": v(-22.95, -30.56) * mm, "end": v(-20.95, -30.56) * mm});
            skLineSegment(sketch, "E208.7.18.3", {"start": v(-20.95, -28.56) * mm, "end": v(-20.95, -30.56) * mm});
            skLineSegment(sketch, "E208.7.19.0", {"start": v(-22.95, -32.56) * mm, "end": v(-20.95, -32.56) * mm});
            skLineSegment(sketch, "E208.7.19.1", {"start": v(-22.95, -32.56) * mm, "end": v(-22.95, -34.56) * mm});
            skLineSegment(sketch, "E208.7.19.2", {"start": v(-22.95, -34.56) * mm, "end": v(-20.95, -34.56) * mm});
            skLineSegment(sketch, "E208.7.19.3", {"start": v(-20.95, -32.56) * mm, "end": v(-20.95, -34.56) * mm});
            skLineSegment(sketch, "E208.7.20.0", {"start": v(-22.95, -36.56) * mm, "end": v(-20.95, -36.56) * mm});
            skLineSegment(sketch, "E208.7.20.1", {"start": v(-22.95, -36.56) * mm, "end": v(-22.95, -38.56) * mm});
            skLineSegment(sketch, "E208.7.20.2", {"start": v(-22.95, -38.56) * mm, "end": v(-20.95, -38.56) * mm});
            skLineSegment(sketch, "E208.7.20.3", {"start": v(-20.95, -36.56) * mm, "end": v(-20.95, -38.56) * mm});
            skLineSegment(sketch, "E208.7.21.0", {"start": v(-22.95, -40.56) * mm, "end": v(-20.95, -40.56) * mm});
            skLineSegment(sketch, "E208.7.21.1", {"start": v(-22.95, -40.56) * mm, "end": v(-22.95, -42.56) * mm});
            skLineSegment(sketch, "E208.7.21.2", {"start": v(-22.95, -42.56) * mm, "end": v(-20.95, -42.56) * mm});
            skLineSegment(sketch, "E208.7.21.3", {"start": v(-20.95, -40.56) * mm, "end": v(-20.95, -42.56) * mm});
            skLineSegment(sketch, "E208.8.0.0", {"start": v(-18.95, 43.44) * mm, "end": v(-16.95, 43.44) * mm});
            skLineSegment(sketch, "E208.8.0.1", {"start": v(-18.95, 43.44) * mm, "end": v(-18.95, 41.44) * mm});
            skLineSegment(sketch, "E208.8.0.2", {"start": v(-18.95, 41.44) * mm, "end": v(-16.95, 41.44) * mm});
            skLineSegment(sketch, "E208.8.0.3", {"start": v(-16.95, 43.44) * mm, "end": v(-16.95, 41.44) * mm});
            skLineSegment(sketch, "E208.8.1.0", {"start": v(-18.95, 39.44) * mm, "end": v(-16.95, 39.44) * mm});
            skLineSegment(sketch, "E208.8.1.1", {"start": v(-18.95, 39.44) * mm, "end": v(-18.95, 37.44) * mm});
            skLineSegment(sketch, "E208.8.1.2", {"start": v(-18.95, 37.44) * mm, "end": v(-16.95, 37.44) * mm});
            skLineSegment(sketch, "E208.8.1.3", {"start": v(-16.95, 39.44) * mm, "end": v(-16.95, 37.44) * mm});
            skLineSegment(sketch, "E208.8.2.0", {"start": v(-18.95, 35.44) * mm, "end": v(-16.95, 35.44) * mm});
            skLineSegment(sketch, "E208.8.2.1", {"start": v(-18.95, 35.44) * mm, "end": v(-18.95, 33.44) * mm});
            skLineSegment(sketch, "E208.8.2.2", {"start": v(-18.95, 33.44) * mm, "end": v(-16.95, 33.44) * mm});
            skLineSegment(sketch, "E208.8.2.3", {"start": v(-16.95, 35.44) * mm, "end": v(-16.95, 33.44) * mm});
            skLineSegment(sketch, "E208.8.3.0", {"start": v(-18.95, 31.44) * mm, "end": v(-16.95, 31.44) * mm});
            skLineSegment(sketch, "E208.8.3.1", {"start": v(-18.95, 31.44) * mm, "end": v(-18.95, 29.44) * mm});
            skLineSegment(sketch, "E208.8.3.2", {"start": v(-18.95, 29.44) * mm, "end": v(-16.95, 29.44) * mm});
            skLineSegment(sketch, "E208.8.3.3", {"start": v(-16.95, 31.44) * mm, "end": v(-16.95, 29.44) * mm});
            skLineSegment(sketch, "E208.8.4.0", {"start": v(-18.95, 27.44) * mm, "end": v(-16.95, 27.44) * mm});
            skLineSegment(sketch, "E208.8.4.1", {"start": v(-18.95, 27.44) * mm, "end": v(-18.95, 25.44) * mm});
            skLineSegment(sketch, "E208.8.4.2", {"start": v(-18.95, 25.44) * mm, "end": v(-16.95, 25.44) * mm});
            skLineSegment(sketch, "E208.8.4.3", {"start": v(-16.95, 27.44) * mm, "end": v(-16.95, 25.44) * mm});
            skLineSegment(sketch, "E208.8.5.0", {"start": v(-18.95, 23.44) * mm, "end": v(-16.95, 23.44) * mm});
            skLineSegment(sketch, "E208.8.5.1", {"start": v(-18.95, 23.44) * mm, "end": v(-18.95, 21.44) * mm});
            skLineSegment(sketch, "E208.8.5.2", {"start": v(-18.95, 21.44) * mm, "end": v(-16.95, 21.44) * mm});
            skLineSegment(sketch, "E208.8.5.3", {"start": v(-16.95, 23.44) * mm, "end": v(-16.95, 21.44) * mm});
            skLineSegment(sketch, "E208.8.6.0", {"start": v(-18.95, 19.44) * mm, "end": v(-16.95, 19.44) * mm});
            skLineSegment(sketch, "E208.8.6.1", {"start": v(-18.95, 19.44) * mm, "end": v(-18.95, 17.44) * mm});
            skLineSegment(sketch, "E208.8.6.2", {"start": v(-18.95, 17.44) * mm, "end": v(-16.95, 17.44) * mm});
            skLineSegment(sketch, "E208.8.6.3", {"start": v(-16.95, 19.44) * mm, "end": v(-16.95, 17.44) * mm});
            skLineSegment(sketch, "E208.8.7.0", {"start": v(-18.95, 15.44) * mm, "end": v(-16.95, 15.44) * mm});
            skLineSegment(sketch, "E208.8.7.1", {"start": v(-18.95, 15.44) * mm, "end": v(-18.95, 13.44) * mm});
            skLineSegment(sketch, "E208.8.7.2", {"start": v(-18.95, 13.44) * mm, "end": v(-16.95, 13.44) * mm});
            skLineSegment(sketch, "E208.8.7.3", {"start": v(-16.95, 15.44) * mm, "end": v(-16.95, 13.44) * mm});
            skLineSegment(sketch, "E208.8.8.0", {"start": v(-18.95, 11.44) * mm, "end": v(-16.95, 11.44) * mm});
            skLineSegment(sketch, "E208.8.8.1", {"start": v(-18.95, 11.44) * mm, "end": v(-18.95, 9.44) * mm});
            skLineSegment(sketch, "E208.8.8.2", {"start": v(-18.95, 9.44) * mm, "end": v(-16.95, 9.44) * mm});
            skLineSegment(sketch, "E208.8.8.3", {"start": v(-16.95, 11.44) * mm, "end": v(-16.95, 9.44) * mm});
            skLineSegment(sketch, "E208.8.9.0", {"start": v(-18.95, 7.44) * mm, "end": v(-16.95, 7.44) * mm});
            skLineSegment(sketch, "E208.8.9.1", {"start": v(-18.95, 7.44) * mm, "end": v(-18.95, 5.44) * mm});
            skLineSegment(sketch, "E208.8.9.2", {"start": v(-18.95, 5.44) * mm, "end": v(-16.95, 5.44) * mm});
            skLineSegment(sketch, "E208.8.9.3", {"start": v(-16.95, 7.44) * mm, "end": v(-16.95, 5.44) * mm});
            skLineSegment(sketch, "E208.8.10.0", {"start": v(-18.95, 3.44) * mm, "end": v(-16.95, 3.44) * mm});
            skLineSegment(sketch, "E208.8.10.1", {"start": v(-18.95, 3.44) * mm, "end": v(-18.95, 1.44) * mm});
            skLineSegment(sketch, "E208.8.10.2", {"start": v(-18.95, 1.44) * mm, "end": v(-16.95, 1.44) * mm});
            skLineSegment(sketch, "E208.8.10.3", {"start": v(-16.95, 3.44) * mm, "end": v(-16.95, 1.44) * mm});
            skLineSegment(sketch, "E208.8.11.0", {"start": v(-18.95, -0.56) * mm, "end": v(-16.95, -0.56) * mm});
            skLineSegment(sketch, "E208.8.11.1", {"start": v(-18.95, -0.56) * mm, "end": v(-18.95, -2.56) * mm});
            skLineSegment(sketch, "E208.8.11.2", {"start": v(-18.95, -2.56) * mm, "end": v(-16.95, -2.56) * mm});
            skLineSegment(sketch, "E208.8.11.3", {"start": v(-16.95, -0.56) * mm, "end": v(-16.95, -2.56) * mm});
            skLineSegment(sketch, "E208.8.12.0", {"start": v(-18.95, -4.56) * mm, "end": v(-16.95, -4.56) * mm});
            skLineSegment(sketch, "E208.8.12.1", {"start": v(-18.95, -4.56) * mm, "end": v(-18.95, -6.56) * mm});
            skLineSegment(sketch, "E208.8.12.2", {"start": v(-18.95, -6.56) * mm, "end": v(-16.95, -6.56) * mm});
            skLineSegment(sketch, "E208.8.12.3", {"start": v(-16.95, -4.56) * mm, "end": v(-16.95, -6.56) * mm});
            skLineSegment(sketch, "E208.8.13.0", {"start": v(-18.95, -8.56) * mm, "end": v(-16.95, -8.56) * mm});
            skLineSegment(sketch, "E208.8.13.1", {"start": v(-18.95, -8.56) * mm, "end": v(-18.95, -10.56) * mm});
            skLineSegment(sketch, "E208.8.13.2", {"start": v(-18.95, -10.56) * mm, "end": v(-16.95, -10.56) * mm});
            skLineSegment(sketch, "E208.8.13.3", {"start": v(-16.95, -8.56) * mm, "end": v(-16.95, -10.56) * mm});
            skLineSegment(sketch, "E208.8.14.0", {"start": v(-18.95, -12.56) * mm, "end": v(-16.95, -12.56) * mm});
            skLineSegment(sketch, "E208.8.14.1", {"start": v(-18.95, -12.56) * mm, "end": v(-18.95, -14.56) * mm});
            skLineSegment(sketch, "E208.8.14.2", {"start": v(-18.95, -14.56) * mm, "end": v(-16.95, -14.56) * mm});
            skLineSegment(sketch, "E208.8.14.3", {"start": v(-16.95, -12.56) * mm, "end": v(-16.95, -14.56) * mm});
            skLineSegment(sketch, "E208.8.15.0", {"start": v(-18.95, -16.56) * mm, "end": v(-16.95, -16.56) * mm});
            skLineSegment(sketch, "E208.8.15.1", {"start": v(-18.95, -16.56) * mm, "end": v(-18.95, -18.56) * mm});
            skLineSegment(sketch, "E208.8.15.2", {"start": v(-18.95, -18.56) * mm, "end": v(-16.95, -18.56) * mm});
            skLineSegment(sketch, "E208.8.15.3", {"start": v(-16.95, -16.56) * mm, "end": v(-16.95, -18.56) * mm});
            skLineSegment(sketch, "E208.8.16.0", {"start": v(-18.95, -20.56) * mm, "end": v(-16.95, -20.56) * mm});
            skLineSegment(sketch, "E208.8.16.1", {"start": v(-18.95, -20.56) * mm, "end": v(-18.95, -22.56) * mm});
            skLineSegment(sketch, "E208.8.16.2", {"start": v(-18.95, -22.56) * mm, "end": v(-16.95, -22.56) * mm});
            skLineSegment(sketch, "E208.8.16.3", {"start": v(-16.95, -20.56) * mm, "end": v(-16.95, -22.56) * mm});
            skLineSegment(sketch, "E208.8.17.0", {"start": v(-18.95, -24.56) * mm, "end": v(-16.95, -24.56) * mm});
            skLineSegment(sketch, "E208.8.17.1", {"start": v(-18.95, -24.56) * mm, "end": v(-18.95, -26.56) * mm});
            skLineSegment(sketch, "E208.8.17.2", {"start": v(-18.95, -26.56) * mm, "end": v(-16.95, -26.56) * mm});
            skLineSegment(sketch, "E208.8.17.3", {"start": v(-16.95, -24.56) * mm, "end": v(-16.95, -26.56) * mm});
            skLineSegment(sketch, "E208.8.18.0", {"start": v(-18.95, -28.56) * mm, "end": v(-16.95, -28.56) * mm});
            skLineSegment(sketch, "E208.8.18.1", {"start": v(-18.95, -28.56) * mm, "end": v(-18.95, -30.56) * mm});
            skLineSegment(sketch, "E208.8.18.2", {"start": v(-18.95, -30.56) * mm, "end": v(-16.95, -30.56) * mm});
            skLineSegment(sketch, "E208.8.18.3", {"start": v(-16.95, -28.56) * mm, "end": v(-16.95, -30.56) * mm});
            skLineSegment(sketch, "E208.8.19.0", {"start": v(-18.95, -32.56) * mm, "end": v(-16.95, -32.56) * mm});
            skLineSegment(sketch, "E208.8.19.1", {"start": v(-18.95, -32.56) * mm, "end": v(-18.95, -34.56) * mm});
            skLineSegment(sketch, "E208.8.19.2", {"start": v(-18.95, -34.56) * mm, "end": v(-16.95, -34.56) * mm});
            skLineSegment(sketch, "E208.8.19.3", {"start": v(-16.95, -32.56) * mm, "end": v(-16.95, -34.56) * mm});
            skLineSegment(sketch, "E208.8.20.0", {"start": v(-18.95, -36.56) * mm, "end": v(-16.95, -36.56) * mm});
            skLineSegment(sketch, "E208.8.20.1", {"start": v(-18.95, -36.56) * mm, "end": v(-18.95, -38.56) * mm});
            skLineSegment(sketch, "E208.8.20.2", {"start": v(-18.95, -38.56) * mm, "end": v(-16.95, -38.56) * mm});
            skLineSegment(sketch, "E208.8.20.3", {"start": v(-16.95, -36.56) * mm, "end": v(-16.95, -38.56) * mm});
            skLineSegment(sketch, "E208.8.21.0", {"start": v(-18.95, -40.56) * mm, "end": v(-16.95, -40.56) * mm});
            skLineSegment(sketch, "E208.8.21.1", {"start": v(-18.95, -40.56) * mm, "end": v(-18.95, -42.56) * mm});
            skLineSegment(sketch, "E208.8.21.2", {"start": v(-18.95, -42.56) * mm, "end": v(-16.95, -42.56) * mm});
            skLineSegment(sketch, "E208.8.21.3", {"start": v(-16.95, -40.56) * mm, "end": v(-16.95, -42.56) * mm});
            skLineSegment(sketch, "E208.9.0.0", {"start": v(-14.95, 43.44) * mm, "end": v(-12.95, 43.44) * mm});
            skLineSegment(sketch, "E208.9.0.1", {"start": v(-14.95, 43.44) * mm, "end": v(-14.95, 41.44) * mm});
            skLineSegment(sketch, "E208.9.0.2", {"start": v(-14.95, 41.44) * mm, "end": v(-12.95, 41.44) * mm});
            skLineSegment(sketch, "E208.9.0.3", {"start": v(-12.95, 43.44) * mm, "end": v(-12.95, 41.44) * mm});
            skLineSegment(sketch, "E208.9.1.0", {"start": v(-14.95, 39.44) * mm, "end": v(-12.95, 39.44) * mm});
            skLineSegment(sketch, "E208.9.1.1", {"start": v(-14.95, 39.44) * mm, "end": v(-14.95, 37.44) * mm});
            skLineSegment(sketch, "E208.9.1.2", {"start": v(-14.95, 37.44) * mm, "end": v(-12.95, 37.44) * mm});
            skLineSegment(sketch, "E208.9.1.3", {"start": v(-12.95, 39.44) * mm, "end": v(-12.95, 37.44) * mm});
            skLineSegment(sketch, "E208.9.2.0", {"start": v(-14.95, 35.44) * mm, "end": v(-12.95, 35.44) * mm});
            skLineSegment(sketch, "E208.9.2.1", {"start": v(-14.95, 35.44) * mm, "end": v(-14.95, 33.44) * mm});
            skLineSegment(sketch, "E208.9.2.2", {"start": v(-14.95, 33.44) * mm, "end": v(-12.95, 33.44) * mm});
            skLineSegment(sketch, "E208.9.2.3", {"start": v(-12.95, 35.44) * mm, "end": v(-12.95, 33.44) * mm});
            skLineSegment(sketch, "E208.9.3.0", {"start": v(-14.95, 31.44) * mm, "end": v(-12.95, 31.44) * mm});
            skLineSegment(sketch, "E208.9.3.1", {"start": v(-14.95, 31.44) * mm, "end": v(-14.95, 29.44) * mm});
            skLineSegment(sketch, "E208.9.3.2", {"start": v(-14.95, 29.44) * mm, "end": v(-12.95, 29.44) * mm});
            skLineSegment(sketch, "E208.9.3.3", {"start": v(-12.95, 31.44) * mm, "end": v(-12.95, 29.44) * mm});
            skLineSegment(sketch, "E208.9.4.0", {"start": v(-14.95, 27.44) * mm, "end": v(-12.95, 27.44) * mm});
            skLineSegment(sketch, "E208.9.4.1", {"start": v(-14.95, 27.44) * mm, "end": v(-14.95, 25.44) * mm});
            skLineSegment(sketch, "E208.9.4.2", {"start": v(-14.95, 25.44) * mm, "end": v(-12.95, 25.44) * mm});
            skLineSegment(sketch, "E208.9.4.3", {"start": v(-12.95, 27.44) * mm, "end": v(-12.95, 25.44) * mm});
            skLineSegment(sketch, "E208.9.5.0", {"start": v(-14.95, 23.44) * mm, "end": v(-12.95, 23.44) * mm});
            skLineSegment(sketch, "E208.9.5.1", {"start": v(-14.95, 23.44) * mm, "end": v(-14.95, 21.44) * mm});
            skLineSegment(sketch, "E208.9.5.2", {"start": v(-14.95, 21.44) * mm, "end": v(-12.95, 21.44) * mm});
            skLineSegment(sketch, "E208.9.5.3", {"start": v(-12.95, 23.44) * mm, "end": v(-12.95, 21.44) * mm});
            skLineSegment(sketch, "E208.9.6.0", {"start": v(-14.95, 19.44) * mm, "end": v(-12.95, 19.44) * mm});
            skLineSegment(sketch, "E208.9.6.1", {"start": v(-14.95, 19.44) * mm, "end": v(-14.95, 17.44) * mm});
            skLineSegment(sketch, "E208.9.6.2", {"start": v(-14.95, 17.44) * mm, "end": v(-12.95, 17.44) * mm});
            skLineSegment(sketch, "E208.9.6.3", {"start": v(-12.95, 19.44) * mm, "end": v(-12.95, 17.44) * mm});
            skLineSegment(sketch, "E208.9.7.0", {"start": v(-14.95, 15.44) * mm, "end": v(-12.95, 15.44) * mm});
            skLineSegment(sketch, "E208.9.7.1", {"start": v(-14.95, 15.44) * mm, "end": v(-14.95, 13.44) * mm});
            skLineSegment(sketch, "E208.9.7.2", {"start": v(-14.95, 13.44) * mm, "end": v(-12.95, 13.44) * mm});
            skLineSegment(sketch, "E208.9.7.3", {"start": v(-12.95, 15.44) * mm, "end": v(-12.95, 13.44) * mm});
            skLineSegment(sketch, "E208.9.8.0", {"start": v(-14.95, 11.44) * mm, "end": v(-12.95, 11.44) * mm});
            skLineSegment(sketch, "E208.9.8.1", {"start": v(-14.95, 11.44) * mm, "end": v(-14.95, 9.44) * mm});
            skLineSegment(sketch, "E208.9.8.2", {"start": v(-14.95, 9.44) * mm, "end": v(-12.95, 9.44) * mm});
            skLineSegment(sketch, "E208.9.8.3", {"start": v(-12.95, 11.44) * mm, "end": v(-12.95, 9.44) * mm});
            skLineSegment(sketch, "E208.9.9.0", {"start": v(-14.95, 7.44) * mm, "end": v(-12.95, 7.44) * mm});
            skLineSegment(sketch, "E208.9.9.1", {"start": v(-14.95, 7.44) * mm, "end": v(-14.95, 5.44) * mm});
            skLineSegment(sketch, "E208.9.9.2", {"start": v(-14.95, 5.44) * mm, "end": v(-12.95, 5.44) * mm});
            skLineSegment(sketch, "E208.9.9.3", {"start": v(-12.95, 7.44) * mm, "end": v(-12.95, 5.44) * mm});
            skLineSegment(sketch, "E208.9.10.0", {"start": v(-14.95, 3.44) * mm, "end": v(-12.95, 3.44) * mm});
            skLineSegment(sketch, "E208.9.10.1", {"start": v(-14.95, 3.44) * mm, "end": v(-14.95, 1.44) * mm});
            skLineSegment(sketch, "E208.9.10.2", {"start": v(-14.95, 1.44) * mm, "end": v(-12.95, 1.44) * mm});
            skLineSegment(sketch, "E208.9.10.3", {"start": v(-12.95, 3.44) * mm, "end": v(-12.95, 1.44) * mm});
            skLineSegment(sketch, "E208.9.11.0", {"start": v(-14.95, -0.56) * mm, "end": v(-12.95, -0.56) * mm});
            skLineSegment(sketch, "E208.9.11.1", {"start": v(-14.95, -0.56) * mm, "end": v(-14.95, -2.56) * mm});
            skLineSegment(sketch, "E208.9.11.2", {"start": v(-14.95, -2.56) * mm, "end": v(-12.95, -2.56) * mm});
            skLineSegment(sketch, "E208.9.11.3", {"start": v(-12.95, -0.56) * mm, "end": v(-12.95, -2.56) * mm});
            skLineSegment(sketch, "E208.9.12.0", {"start": v(-14.95, -4.56) * mm, "end": v(-12.95, -4.56) * mm});
            skLineSegment(sketch, "E208.9.12.1", {"start": v(-14.95, -4.56) * mm, "end": v(-14.95, -6.56) * mm});
            skLineSegment(sketch, "E208.9.12.2", {"start": v(-14.95, -6.56) * mm, "end": v(-12.95, -6.56) * mm});
            skLineSegment(sketch, "E208.9.12.3", {"start": v(-12.95, -4.56) * mm, "end": v(-12.95, -6.56) * mm});
            skLineSegment(sketch, "E208.9.13.0", {"start": v(-14.95, -8.56) * mm, "end": v(-12.95, -8.56) * mm});
            skLineSegment(sketch, "E208.9.13.1", {"start": v(-14.95, -8.56) * mm, "end": v(-14.95, -10.56) * mm});
            skLineSegment(sketch, "E208.9.13.2", {"start": v(-14.95, -10.56) * mm, "end": v(-12.95, -10.56) * mm});
            skLineSegment(sketch, "E208.9.13.3", {"start": v(-12.95, -8.56) * mm, "end": v(-12.95, -10.56) * mm});
            skLineSegment(sketch, "E208.9.14.0", {"start": v(-14.95, -12.56) * mm, "end": v(-12.95, -12.56) * mm});
            skLineSegment(sketch, "E208.9.14.1", {"start": v(-14.95, -12.56) * mm, "end": v(-14.95, -14.56) * mm});
            skLineSegment(sketch, "E208.9.14.2", {"start": v(-14.95, -14.56) * mm, "end": v(-12.95, -14.56) * mm});
            skLineSegment(sketch, "E208.9.14.3", {"start": v(-12.95, -12.56) * mm, "end": v(-12.95, -14.56) * mm});
            skLineSegment(sketch, "E208.9.15.0", {"start": v(-14.95, -16.56) * mm, "end": v(-12.95, -16.56) * mm});
            skLineSegment(sketch, "E208.9.15.1", {"start": v(-14.95, -16.56) * mm, "end": v(-14.95, -18.56) * mm});
            skLineSegment(sketch, "E208.9.15.2", {"start": v(-14.95, -18.56) * mm, "end": v(-12.95, -18.56) * mm});
            skLineSegment(sketch, "E208.9.15.3", {"start": v(-12.95, -16.56) * mm, "end": v(-12.95, -18.56) * mm});
            skLineSegment(sketch, "E208.9.16.0", {"start": v(-14.95, -20.56) * mm, "end": v(-12.95, -20.56) * mm});
            skLineSegment(sketch, "E208.9.16.1", {"start": v(-14.95, -20.56) * mm, "end": v(-14.95, -22.56) * mm});
            skLineSegment(sketch, "E208.9.16.2", {"start": v(-14.95, -22.56) * mm, "end": v(-12.95, -22.56) * mm});
            skLineSegment(sketch, "E208.9.16.3", {"start": v(-12.95, -20.56) * mm, "end": v(-12.95, -22.56) * mm});
            skLineSegment(sketch, "E208.9.17.0", {"start": v(-14.95, -24.56) * mm, "end": v(-12.95, -24.56) * mm});
            skLineSegment(sketch, "E208.9.17.1", {"start": v(-14.95, -24.56) * mm, "end": v(-14.95, -26.56) * mm});
            skLineSegment(sketch, "E208.9.17.2", {"start": v(-14.95, -26.56) * mm, "end": v(-12.95, -26.56) * mm});
            skLineSegment(sketch, "E208.9.17.3", {"start": v(-12.95, -24.56) * mm, "end": v(-12.95, -26.56) * mm});
            skLineSegment(sketch, "E208.9.18.0", {"start": v(-14.95, -28.56) * mm, "end": v(-12.95, -28.56) * mm});
            skLineSegment(sketch, "E208.9.18.1", {"start": v(-14.95, -28.56) * mm, "end": v(-14.95, -30.56) * mm});
            skLineSegment(sketch, "E208.9.18.2", {"start": v(-14.95, -30.56) * mm, "end": v(-12.95, -30.56) * mm});
            skLineSegment(sketch, "E208.9.18.3", {"start": v(-12.95, -28.56) * mm, "end": v(-12.95, -30.56) * mm});
            skLineSegment(sketch, "E208.9.19.0", {"start": v(-14.95, -32.56) * mm, "end": v(-12.95, -32.56) * mm});
            skLineSegment(sketch, "E208.9.19.1", {"start": v(-14.95, -32.56) * mm, "end": v(-14.95, -34.56) * mm});
            skLineSegment(sketch, "E208.9.19.2", {"start": v(-14.95, -34.56) * mm, "end": v(-12.95, -34.56) * mm});
            skLineSegment(sketch, "E208.9.19.3", {"start": v(-12.95, -32.56) * mm, "end": v(-12.95, -34.56) * mm});
            skLineSegment(sketch, "E208.9.20.0", {"start": v(-14.95, -36.56) * mm, "end": v(-12.95, -36.56) * mm});
            skLineSegment(sketch, "E208.9.20.1", {"start": v(-14.95, -36.56) * mm, "end": v(-14.95, -38.56) * mm});
            skLineSegment(sketch, "E208.9.20.2", {"start": v(-14.95, -38.56) * mm, "end": v(-12.95, -38.56) * mm});
            skLineSegment(sketch, "E208.9.20.3", {"start": v(-12.95, -36.56) * mm, "end": v(-12.95, -38.56) * mm});
            skLineSegment(sketch, "E208.9.21.0", {"start": v(-14.95, -40.56) * mm, "end": v(-12.95, -40.56) * mm});
            skLineSegment(sketch, "E208.9.21.1", {"start": v(-14.95, -40.56) * mm, "end": v(-14.95, -42.56) * mm});
            skLineSegment(sketch, "E208.9.21.2", {"start": v(-14.95, -42.56) * mm, "end": v(-12.95, -42.56) * mm});
            skLineSegment(sketch, "E208.9.21.3", {"start": v(-12.95, -40.56) * mm, "end": v(-12.95, -42.56) * mm});
            skLineSegment(sketch, "E208.10.0.0", {"start": v(-10.95, 43.44) * mm, "end": v(-8.95, 43.44) * mm});
            skLineSegment(sketch, "E208.10.0.1", {"start": v(-10.95, 43.44) * mm, "end": v(-10.95, 41.44) * mm});
            skLineSegment(sketch, "E208.10.0.2", {"start": v(-10.95, 41.44) * mm, "end": v(-8.95, 41.44) * mm});
            skLineSegment(sketch, "E208.10.0.3", {"start": v(-8.95, 43.44) * mm, "end": v(-8.95, 41.44) * mm});
            skLineSegment(sketch, "E208.10.1.0", {"start": v(-10.95, 39.44) * mm, "end": v(-8.95, 39.44) * mm});
            skLineSegment(sketch, "E208.10.1.1", {"start": v(-10.95, 39.44) * mm, "end": v(-10.95, 37.44) * mm});
            skLineSegment(sketch, "E208.10.1.2", {"start": v(-10.95, 37.44) * mm, "end": v(-8.95, 37.44) * mm});
            skLineSegment(sketch, "E208.10.1.3", {"start": v(-8.95, 39.44) * mm, "end": v(-8.95, 37.44) * mm});
            skLineSegment(sketch, "E208.10.2.0", {"start": v(-10.95, 35.44) * mm, "end": v(-8.95, 35.44) * mm});
            skLineSegment(sketch, "E208.10.2.1", {"start": v(-10.95, 35.44) * mm, "end": v(-10.95, 33.44) * mm});
            skLineSegment(sketch, "E208.10.2.2", {"start": v(-10.95, 33.44) * mm, "end": v(-8.95, 33.44) * mm});
            skLineSegment(sketch, "E208.10.2.3", {"start": v(-8.95, 35.44) * mm, "end": v(-8.95, 33.44) * mm});
            skLineSegment(sketch, "E208.10.3.0", {"start": v(-10.95, 31.44) * mm, "end": v(-8.95, 31.44) * mm});
            skLineSegment(sketch, "E208.10.3.1", {"start": v(-10.95, 31.44) * mm, "end": v(-10.95, 29.44) * mm});
            skLineSegment(sketch, "E208.10.3.2", {"start": v(-10.95, 29.44) * mm, "end": v(-8.95, 29.44) * mm});
            skLineSegment(sketch, "E208.10.3.3", {"start": v(-8.95, 31.44) * mm, "end": v(-8.95, 29.44) * mm});
            skLineSegment(sketch, "E208.10.4.0", {"start": v(-10.95, 27.44) * mm, "end": v(-8.95, 27.44) * mm});
            skLineSegment(sketch, "E208.10.4.1", {"start": v(-10.95, 27.44) * mm, "end": v(-10.95, 25.44) * mm});
            skLineSegment(sketch, "E208.10.4.2", {"start": v(-10.95, 25.44) * mm, "end": v(-8.95, 25.44) * mm});
            skLineSegment(sketch, "E208.10.4.3", {"start": v(-8.95, 27.44) * mm, "end": v(-8.95, 25.44) * mm});
            skLineSegment(sketch, "E208.10.5.0", {"start": v(-10.95, 23.44) * mm, "end": v(-8.95, 23.44) * mm});
            skLineSegment(sketch, "E208.10.5.1", {"start": v(-10.95, 23.44) * mm, "end": v(-10.95, 21.44) * mm});
            skLineSegment(sketch, "E208.10.5.2", {"start": v(-10.95, 21.44) * mm, "end": v(-8.95, 21.44) * mm});
            skLineSegment(sketch, "E208.10.5.3", {"start": v(-8.95, 23.44) * mm, "end": v(-8.95, 21.44) * mm});
            skLineSegment(sketch, "E208.10.6.0", {"start": v(-10.95, 19.44) * mm, "end": v(-8.95, 19.44) * mm});
            skLineSegment(sketch, "E208.10.6.1", {"start": v(-10.95, 19.44) * mm, "end": v(-10.95, 17.44) * mm});
            skLineSegment(sketch, "E208.10.6.2", {"start": v(-10.95, 17.44) * mm, "end": v(-8.95, 17.44) * mm});
            skLineSegment(sketch, "E208.10.6.3", {"start": v(-8.95, 19.44) * mm, "end": v(-8.95, 17.44) * mm});
            skLineSegment(sketch, "E208.10.7.0", {"start": v(-10.95, 15.44) * mm, "end": v(-8.95, 15.44) * mm});
            skLineSegment(sketch, "E208.10.7.1", {"start": v(-10.95, 15.44) * mm, "end": v(-10.95, 13.44) * mm});
            skLineSegment(sketch, "E208.10.7.2", {"start": v(-10.95, 13.44) * mm, "end": v(-8.95, 13.44) * mm});
            skLineSegment(sketch, "E208.10.7.3", {"start": v(-8.95, 15.44) * mm, "end": v(-8.95, 13.44) * mm});
            skLineSegment(sketch, "E208.10.8.0", {"start": v(-10.95, 11.44) * mm, "end": v(-8.95, 11.44) * mm});
            skLineSegment(sketch, "E208.10.8.1", {"start": v(-10.95, 11.44) * mm, "end": v(-10.95, 9.44) * mm});
            skLineSegment(sketch, "E208.10.8.2", {"start": v(-10.95, 9.44) * mm, "end": v(-8.95, 9.44) * mm});
            skLineSegment(sketch, "E208.10.8.3", {"start": v(-8.95, 11.44) * mm, "end": v(-8.95, 9.44) * mm});
            skLineSegment(sketch, "E208.10.9.0", {"start": v(-10.95, 7.44) * mm, "end": v(-8.95, 7.44) * mm});
            skLineSegment(sketch, "E208.10.9.1", {"start": v(-10.95, 7.44) * mm, "end": v(-10.95, 5.44) * mm});
            skLineSegment(sketch, "E208.10.9.2", {"start": v(-10.95, 5.44) * mm, "end": v(-8.95, 5.44) * mm});
            skLineSegment(sketch, "E208.10.9.3", {"start": v(-8.95, 7.44) * mm, "end": v(-8.95, 5.44) * mm});
            skLineSegment(sketch, "E208.10.10.0", {"start": v(-10.95, 3.44) * mm, "end": v(-8.95, 3.44) * mm});
            skLineSegment(sketch, "E208.10.10.1", {"start": v(-10.95, 3.44) * mm, "end": v(-10.95, 1.44) * mm});
            skLineSegment(sketch, "E208.10.10.2", {"start": v(-10.95, 1.44) * mm, "end": v(-8.95, 1.44) * mm});
            skLineSegment(sketch, "E208.10.10.3", {"start": v(-8.95, 3.44) * mm, "end": v(-8.95, 1.44) * mm});
            skLineSegment(sketch, "E208.10.11.0", {"start": v(-10.95, -0.56) * mm, "end": v(-8.95, -0.56) * mm});
            skLineSegment(sketch, "E208.10.11.1", {"start": v(-10.95, -0.56) * mm, "end": v(-10.95, -2.56) * mm});
            skLineSegment(sketch, "E208.10.11.2", {"start": v(-10.95, -2.56) * mm, "end": v(-8.95, -2.56) * mm});
            skLineSegment(sketch, "E208.10.11.3", {"start": v(-8.95, -0.56) * mm, "end": v(-8.95, -2.56) * mm});
            skLineSegment(sketch, "E208.10.12.0", {"start": v(-10.95, -4.56) * mm, "end": v(-8.95, -4.56) * mm});
            skLineSegment(sketch, "E208.10.12.1", {"start": v(-10.95, -4.56) * mm, "end": v(-10.95, -6.56) * mm});
            skLineSegment(sketch, "E208.10.12.2", {"start": v(-10.95, -6.56) * mm, "end": v(-8.95, -6.56) * mm});
            skLineSegment(sketch, "E208.10.12.3", {"start": v(-8.95, -4.56) * mm, "end": v(-8.95, -6.56) * mm});
            skLineSegment(sketch, "E208.10.13.0", {"start": v(-10.95, -8.56) * mm, "end": v(-8.95, -8.56) * mm});
            skLineSegment(sketch, "E208.10.13.1", {"start": v(-10.95, -8.56) * mm, "end": v(-10.95, -10.56) * mm});
            skLineSegment(sketch, "E208.10.13.2", {"start": v(-10.95, -10.56) * mm, "end": v(-8.95, -10.56) * mm});
            skLineSegment(sketch, "E208.10.13.3", {"start": v(-8.95, -8.56) * mm, "end": v(-8.95, -10.56) * mm});
            skLineSegment(sketch, "E208.10.14.0", {"start": v(-10.95, -12.56) * mm, "end": v(-8.95, -12.56) * mm});
            skLineSegment(sketch, "E208.10.14.1", {"start": v(-10.95, -12.56) * mm, "end": v(-10.95, -14.56) * mm});
            skLineSegment(sketch, "E208.10.14.2", {"start": v(-10.95, -14.56) * mm, "end": v(-8.95, -14.56) * mm});
            skLineSegment(sketch, "E208.10.14.3", {"start": v(-8.95, -12.56) * mm, "end": v(-8.95, -14.56) * mm});
            skLineSegment(sketch, "E208.10.15.0", {"start": v(-10.95, -16.56) * mm, "end": v(-8.95, -16.56) * mm});
            skLineSegment(sketch, "E208.10.15.1", {"start": v(-10.95, -16.56) * mm, "end": v(-10.95, -18.56) * mm});
            skLineSegment(sketch, "E208.10.15.2", {"start": v(-10.95, -18.56) * mm, "end": v(-8.95, -18.56) * mm});
            skLineSegment(sketch, "E208.10.15.3", {"start": v(-8.95, -16.56) * mm, "end": v(-8.95, -18.56) * mm});
            skLineSegment(sketch, "E208.10.16.0", {"start": v(-10.95, -20.56) * mm, "end": v(-8.95, -20.56) * mm});
            skLineSegment(sketch, "E208.10.16.1", {"start": v(-10.95, -20.56) * mm, "end": v(-10.95, -22.56) * mm});
            skLineSegment(sketch, "E208.10.16.2", {"start": v(-10.95, -22.56) * mm, "end": v(-8.95, -22.56) * mm});
            skLineSegment(sketch, "E208.10.16.3", {"start": v(-8.95, -20.56) * mm, "end": v(-8.95, -22.56) * mm});
            skLineSegment(sketch, "E208.10.17.0", {"start": v(-10.95, -24.56) * mm, "end": v(-8.95, -24.56) * mm});
            skLineSegment(sketch, "E208.10.17.1", {"start": v(-10.95, -24.56) * mm, "end": v(-10.95, -26.56) * mm});
            skLineSegment(sketch, "E208.10.17.2", {"start": v(-10.95, -26.56) * mm, "end": v(-8.95, -26.56) * mm});
            skLineSegment(sketch, "E208.10.17.3", {"start": v(-8.95, -24.56) * mm, "end": v(-8.95, -26.56) * mm});
            skLineSegment(sketch, "E208.10.18.0", {"start": v(-10.95, -28.56) * mm, "end": v(-8.95, -28.56) * mm});
            skLineSegment(sketch, "E208.10.18.1", {"start": v(-10.95, -28.56) * mm, "end": v(-10.95, -30.56) * mm});
            skLineSegment(sketch, "E208.10.18.2", {"start": v(-10.95, -30.56) * mm, "end": v(-8.95, -30.56) * mm});
            skLineSegment(sketch, "E208.10.18.3", {"start": v(-8.95, -28.56) * mm, "end": v(-8.95, -30.56) * mm});
            skLineSegment(sketch, "E208.10.19.0", {"start": v(-10.95, -32.56) * mm, "end": v(-8.95, -32.56) * mm});
            skLineSegment(sketch, "E208.10.19.1", {"start": v(-10.95, -32.56) * mm, "end": v(-10.95, -34.56) * mm});
            skLineSegment(sketch, "E208.10.19.2", {"start": v(-10.95, -34.56) * mm, "end": v(-8.95, -34.56) * mm});
            skLineSegment(sketch, "E208.10.19.3", {"start": v(-8.95, -32.56) * mm, "end": v(-8.95, -34.56) * mm});
            skLineSegment(sketch, "E208.10.20.0", {"start": v(-10.95, -36.56) * mm, "end": v(-8.95, -36.56) * mm});
            skLineSegment(sketch, "E208.10.20.1", {"start": v(-10.95, -36.56) * mm, "end": v(-10.95, -38.56) * mm});
            skLineSegment(sketch, "E208.10.20.2", {"start": v(-10.95, -38.56) * mm, "end": v(-8.95, -38.56) * mm});
            skLineSegment(sketch, "E208.10.20.3", {"start": v(-8.95, -36.56) * mm, "end": v(-8.95, -38.56) * mm});
            skLineSegment(sketch, "E208.10.21.0", {"start": v(-10.95, -40.56) * mm, "end": v(-8.95, -40.56) * mm});
            skLineSegment(sketch, "E208.10.21.1", {"start": v(-10.95, -40.56) * mm, "end": v(-10.95, -42.56) * mm});
            skLineSegment(sketch, "E208.10.21.2", {"start": v(-10.95, -42.56) * mm, "end": v(-8.95, -42.56) * mm});
            skLineSegment(sketch, "E208.10.21.3", {"start": v(-8.95, -40.56) * mm, "end": v(-8.95, -42.56) * mm});
            skLineSegment(sketch, "E208.11.0.0", {"start": v(-6.95, 43.44) * mm, "end": v(-4.95, 43.44) * mm});
            skLineSegment(sketch, "E208.11.0.1", {"start": v(-6.95, 43.44) * mm, "end": v(-6.95, 41.44) * mm});
            skLineSegment(sketch, "E208.11.0.2", {"start": v(-6.95, 41.44) * mm, "end": v(-4.95, 41.44) * mm});
            skLineSegment(sketch, "E208.11.0.3", {"start": v(-4.95, 43.44) * mm, "end": v(-4.95, 41.44) * mm});
            skLineSegment(sketch, "E208.11.1.0", {"start": v(-6.95, 39.44) * mm, "end": v(-4.95, 39.44) * mm});
            skLineSegment(sketch, "E208.11.1.1", {"start": v(-6.95, 39.44) * mm, "end": v(-6.95, 37.44) * mm});
            skLineSegment(sketch, "E208.11.1.2", {"start": v(-6.95, 37.44) * mm, "end": v(-4.95, 37.44) * mm});
            skLineSegment(sketch, "E208.11.1.3", {"start": v(-4.95, 39.44) * mm, "end": v(-4.95, 37.44) * mm});
            skLineSegment(sketch, "E208.11.2.0", {"start": v(-6.95, 35.44) * mm, "end": v(-4.95, 35.44) * mm});
            skLineSegment(sketch, "E208.11.2.1", {"start": v(-6.95, 35.44) * mm, "end": v(-6.95, 33.44) * mm});
            skLineSegment(sketch, "E208.11.2.2", {"start": v(-6.95, 33.44) * mm, "end": v(-4.95, 33.44) * mm});
            skLineSegment(sketch, "E208.11.2.3", {"start": v(-4.95, 35.44) * mm, "end": v(-4.95, 33.44) * mm});
            skLineSegment(sketch, "E208.11.3.0", {"start": v(-6.95, 31.44) * mm, "end": v(-4.95, 31.44) * mm});
            skLineSegment(sketch, "E208.11.3.1", {"start": v(-6.95, 31.44) * mm, "end": v(-6.95, 29.44) * mm});
            skLineSegment(sketch, "E208.11.3.2", {"start": v(-6.95, 29.44) * mm, "end": v(-4.95, 29.44) * mm});
            skLineSegment(sketch, "E208.11.3.3", {"start": v(-4.95, 31.44) * mm, "end": v(-4.95, 29.44) * mm});
            skLineSegment(sketch, "E208.11.4.0", {"start": v(-6.95, 27.44) * mm, "end": v(-4.95, 27.44) * mm});
            skLineSegment(sketch, "E208.11.4.1", {"start": v(-6.95, 27.44) * mm, "end": v(-6.95, 25.44) * mm});
            skLineSegment(sketch, "E208.11.4.2", {"start": v(-6.95, 25.44) * mm, "end": v(-4.95, 25.44) * mm});
            skLineSegment(sketch, "E208.11.4.3", {"start": v(-4.95, 27.44) * mm, "end": v(-4.95, 25.44) * mm});
            skLineSegment(sketch, "E208.11.5.0", {"start": v(-6.95, 23.44) * mm, "end": v(-4.95, 23.44) * mm});
            skLineSegment(sketch, "E208.11.5.1", {"start": v(-6.95, 23.44) * mm, "end": v(-6.95, 21.44) * mm});
            skLineSegment(sketch, "E208.11.5.2", {"start": v(-6.95, 21.44) * mm, "end": v(-4.95, 21.44) * mm});
            skLineSegment(sketch, "E208.11.5.3", {"start": v(-4.95, 23.44) * mm, "end": v(-4.95, 21.44) * mm});
            skLineSegment(sketch, "E208.11.6.0", {"start": v(-6.95, 19.44) * mm, "end": v(-4.95, 19.44) * mm});
            skLineSegment(sketch, "E208.11.6.1", {"start": v(-6.95, 19.44) * mm, "end": v(-6.95, 17.44) * mm});
            skLineSegment(sketch, "E208.11.6.2", {"start": v(-6.95, 17.44) * mm, "end": v(-4.95, 17.44) * mm});
            skLineSegment(sketch, "E208.11.6.3", {"start": v(-4.95, 19.44) * mm, "end": v(-4.95, 17.44) * mm});
            skLineSegment(sketch, "E208.11.7.0", {"start": v(-6.95, 15.44) * mm, "end": v(-4.95, 15.44) * mm});
            skLineSegment(sketch, "E208.11.7.1", {"start": v(-6.95, 15.44) * mm, "end": v(-6.95, 13.44) * mm});
            skLineSegment(sketch, "E208.11.7.2", {"start": v(-6.95, 13.44) * mm, "end": v(-4.95, 13.44) * mm});
            skLineSegment(sketch, "E208.11.7.3", {"start": v(-4.95, 15.44) * mm, "end": v(-4.95, 13.44) * mm});
            skLineSegment(sketch, "E208.11.8.0", {"start": v(-6.95, 11.44) * mm, "end": v(-4.95, 11.44) * mm});
            skLineSegment(sketch, "E208.11.8.1", {"start": v(-6.95, 11.44) * mm, "end": v(-6.95, 9.44) * mm});
            skLineSegment(sketch, "E208.11.8.2", {"start": v(-6.95, 9.44) * mm, "end": v(-4.95, 9.44) * mm});
            skLineSegment(sketch, "E208.11.8.3", {"start": v(-4.95, 11.44) * mm, "end": v(-4.95, 9.44) * mm});
            skLineSegment(sketch, "E208.11.9.0", {"start": v(-6.95, 7.44) * mm, "end": v(-4.95, 7.44) * mm});
            skLineSegment(sketch, "E208.11.9.1", {"start": v(-6.95, 7.44) * mm, "end": v(-6.95, 5.44) * mm});
            skLineSegment(sketch, "E208.11.9.2", {"start": v(-6.95, 5.44) * mm, "end": v(-4.95, 5.44) * mm});
            skLineSegment(sketch, "E208.11.9.3", {"start": v(-4.95, 7.44) * mm, "end": v(-4.95, 5.44) * mm});
            skLineSegment(sketch, "E208.11.10.0", {"start": v(-6.95, 3.44) * mm, "end": v(-4.95, 3.44) * mm});
            skLineSegment(sketch, "E208.11.10.1", {"start": v(-6.95, 3.44) * mm, "end": v(-6.95, 1.44) * mm});
            skLineSegment(sketch, "E208.11.10.2", {"start": v(-6.95, 1.44) * mm, "end": v(-4.95, 1.44) * mm});
            skLineSegment(sketch, "E208.11.10.3", {"start": v(-4.95, 3.44) * mm, "end": v(-4.95, 1.44) * mm});
            skLineSegment(sketch, "E208.11.11.0", {"start": v(-6.95, -0.56) * mm, "end": v(-4.95, -0.56) * mm});
            skLineSegment(sketch, "E208.11.11.1", {"start": v(-6.95, -0.56) * mm, "end": v(-6.95, -2.56) * mm});
            skLineSegment(sketch, "E208.11.11.2", {"start": v(-6.95, -2.56) * mm, "end": v(-4.95, -2.56) * mm});
            skLineSegment(sketch, "E208.11.11.3", {"start": v(-4.95, -0.56) * mm, "end": v(-4.95, -2.56) * mm});
            skLineSegment(sketch, "E208.11.12.0", {"start": v(-6.95, -4.56) * mm, "end": v(-4.95, -4.56) * mm});
            skLineSegment(sketch, "E208.11.12.1", {"start": v(-6.95, -4.56) * mm, "end": v(-6.95, -6.56) * mm});
            skLineSegment(sketch, "E208.11.12.2", {"start": v(-6.95, -6.56) * mm, "end": v(-4.95, -6.56) * mm});
            skLineSegment(sketch, "E208.11.12.3", {"start": v(-4.95, -4.56) * mm, "end": v(-4.95, -6.56) * mm});
            skLineSegment(sketch, "E208.11.13.0", {"start": v(-6.95, -8.56) * mm, "end": v(-4.95, -8.56) * mm});
            skLineSegment(sketch, "E208.11.13.1", {"start": v(-6.95, -8.56) * mm, "end": v(-6.95, -10.56) * mm});
            skLineSegment(sketch, "E208.11.13.2", {"start": v(-6.95, -10.56) * mm, "end": v(-4.95, -10.56) * mm});
            skLineSegment(sketch, "E208.11.13.3", {"start": v(-4.95, -8.56) * mm, "end": v(-4.95, -10.56) * mm});
            skLineSegment(sketch, "E208.11.14.0", {"start": v(-6.95, -12.56) * mm, "end": v(-4.95, -12.56) * mm});
            skLineSegment(sketch, "E208.11.14.1", {"start": v(-6.95, -12.56) * mm, "end": v(-6.95, -14.56) * mm});
            skLineSegment(sketch, "E208.11.14.2", {"start": v(-6.95, -14.56) * mm, "end": v(-4.95, -14.56) * mm});
            skLineSegment(sketch, "E208.11.14.3", {"start": v(-4.95, -12.56) * mm, "end": v(-4.95, -14.56) * mm});
            skLineSegment(sketch, "E208.11.15.0", {"start": v(-6.95, -16.56) * mm, "end": v(-4.95, -16.56) * mm});
            skLineSegment(sketch, "E208.11.15.1", {"start": v(-6.95, -16.56) * mm, "end": v(-6.95, -18.56) * mm});
            skLineSegment(sketch, "E208.11.15.2", {"start": v(-6.95, -18.56) * mm, "end": v(-4.95, -18.56) * mm});
            skLineSegment(sketch, "E208.11.15.3", {"start": v(-4.95, -16.56) * mm, "end": v(-4.95, -18.56) * mm});
            skLineSegment(sketch, "E208.11.16.0", {"start": v(-6.95, -20.56) * mm, "end": v(-4.95, -20.56) * mm});
            skLineSegment(sketch, "E208.11.16.1", {"start": v(-6.95, -20.56) * mm, "end": v(-6.95, -22.56) * mm});
            skLineSegment(sketch, "E208.11.16.2", {"start": v(-6.95, -22.56) * mm, "end": v(-4.95, -22.56) * mm});
            skLineSegment(sketch, "E208.11.16.3", {"start": v(-4.95, -20.56) * mm, "end": v(-4.95, -22.56) * mm});
            skLineSegment(sketch, "E208.11.17.0", {"start": v(-6.95, -24.56) * mm, "end": v(-4.95, -24.56) * mm});
            skLineSegment(sketch, "E208.11.17.1", {"start": v(-6.95, -24.56) * mm, "end": v(-6.95, -26.56) * mm});
            skLineSegment(sketch, "E208.11.17.2", {"start": v(-6.95, -26.56) * mm, "end": v(-4.95, -26.56) * mm});
            skLineSegment(sketch, "E208.11.17.3", {"start": v(-4.95, -24.56) * mm, "end": v(-4.95, -26.56) * mm});
            skLineSegment(sketch, "E208.11.18.0", {"start": v(-6.95, -28.56) * mm, "end": v(-4.95, -28.56) * mm});
            skLineSegment(sketch, "E208.11.18.1", {"start": v(-6.95, -28.56) * mm, "end": v(-6.95, -30.56) * mm});
            skLineSegment(sketch, "E208.11.18.2", {"start": v(-6.95, -30.56) * mm, "end": v(-4.95, -30.56) * mm});
            skLineSegment(sketch, "E208.11.18.3", {"start": v(-4.95, -28.56) * mm, "end": v(-4.95, -30.56) * mm});
            skLineSegment(sketch, "E208.11.19.0", {"start": v(-6.95, -32.56) * mm, "end": v(-4.95, -32.56) * mm});
            skLineSegment(sketch, "E208.11.19.1", {"start": v(-6.95, -32.56) * mm, "end": v(-6.95, -34.56) * mm});
            skLineSegment(sketch, "E208.11.19.2", {"start": v(-6.95, -34.56) * mm, "end": v(-4.95, -34.56) * mm});
            skLineSegment(sketch, "E208.11.19.3", {"start": v(-4.95, -32.56) * mm, "end": v(-4.95, -34.56) * mm});
            skLineSegment(sketch, "E208.11.20.0", {"start": v(-6.95, -36.56) * mm, "end": v(-4.95, -36.56) * mm});
            skLineSegment(sketch, "E208.11.20.1", {"start": v(-6.95, -36.56) * mm, "end": v(-6.95, -38.56) * mm});
            skLineSegment(sketch, "E208.11.20.2", {"start": v(-6.95, -38.56) * mm, "end": v(-4.95, -38.56) * mm});
            skLineSegment(sketch, "E208.11.20.3", {"start": v(-4.95, -36.56) * mm, "end": v(-4.95, -38.56) * mm});
            skLineSegment(sketch, "E208.11.21.0", {"start": v(-6.95, -40.56) * mm, "end": v(-4.95, -40.56) * mm});
            skLineSegment(sketch, "E208.11.21.1", {"start": v(-6.95, -40.56) * mm, "end": v(-6.95, -42.56) * mm});
            skLineSegment(sketch, "E208.11.21.2", {"start": v(-6.95, -42.56) * mm, "end": v(-4.95, -42.56) * mm});
            skLineSegment(sketch, "E208.11.21.3", {"start": v(-4.95, -40.56) * mm, "end": v(-4.95, -42.56) * mm});
            skLineSegment(sketch, "E208.12.0.0", {"start": v(-2.95, 43.44) * mm, "end": v(-0.95, 43.44) * mm});
            skLineSegment(sketch, "E208.12.0.1", {"start": v(-2.95, 43.44) * mm, "end": v(-2.95, 41.44) * mm});
            skLineSegment(sketch, "E208.12.0.2", {"start": v(-2.95, 41.44) * mm, "end": v(-0.95, 41.44) * mm});
            skLineSegment(sketch, "E208.12.0.3", {"start": v(-0.95, 43.44) * mm, "end": v(-0.95, 41.44) * mm});
            skLineSegment(sketch, "E208.12.1.0", {"start": v(-2.95, 39.44) * mm, "end": v(-0.95, 39.44) * mm});
            skLineSegment(sketch, "E208.12.1.1", {"start": v(-2.95, 39.44) * mm, "end": v(-2.95, 37.44) * mm});
            skLineSegment(sketch, "E208.12.1.2", {"start": v(-2.95, 37.44) * mm, "end": v(-0.95, 37.44) * mm});
            skLineSegment(sketch, "E208.12.1.3", {"start": v(-0.95, 39.44) * mm, "end": v(-0.95, 37.44) * mm});
            skLineSegment(sketch, "E208.12.2.0", {"start": v(-2.95, 35.44) * mm, "end": v(-0.95, 35.44) * mm});
            skLineSegment(sketch, "E208.12.2.1", {"start": v(-2.95, 35.44) * mm, "end": v(-2.95, 33.44) * mm});
            skLineSegment(sketch, "E208.12.2.2", {"start": v(-2.95, 33.44) * mm, "end": v(-0.95, 33.44) * mm});
            skLineSegment(sketch, "E208.12.2.3", {"start": v(-0.95, 35.44) * mm, "end": v(-0.95, 33.44) * mm});
            skLineSegment(sketch, "E208.12.3.0", {"start": v(-2.95, 31.44) * mm, "end": v(-0.95, 31.44) * mm});
            skLineSegment(sketch, "E208.12.3.1", {"start": v(-2.95, 31.44) * mm, "end": v(-2.95, 29.44) * mm});
            skLineSegment(sketch, "E208.12.3.2", {"start": v(-2.95, 29.44) * mm, "end": v(-0.95, 29.44) * mm});
            skLineSegment(sketch, "E208.12.3.3", {"start": v(-0.95, 31.44) * mm, "end": v(-0.95, 29.44) * mm});
            skLineSegment(sketch, "E208.12.4.0", {"start": v(-2.95, 27.44) * mm, "end": v(-0.95, 27.44) * mm});
            skLineSegment(sketch, "E208.12.4.1", {"start": v(-2.95, 27.44) * mm, "end": v(-2.95, 25.44) * mm});
            skLineSegment(sketch, "E208.12.4.2", {"start": v(-2.95, 25.44) * mm, "end": v(-0.95, 25.44) * mm});
            skLineSegment(sketch, "E208.12.4.3", {"start": v(-0.95, 27.44) * mm, "end": v(-0.95, 25.44) * mm});
            skLineSegment(sketch, "E208.12.5.0", {"start": v(-2.95, 23.44) * mm, "end": v(-0.95, 23.44) * mm});
            skLineSegment(sketch, "E208.12.5.1", {"start": v(-2.95, 23.44) * mm, "end": v(-2.95, 21.44) * mm});
            skLineSegment(sketch, "E208.12.5.2", {"start": v(-2.95, 21.44) * mm, "end": v(-0.95, 21.44) * mm});
            skLineSegment(sketch, "E208.12.5.3", {"start": v(-0.95, 23.44) * mm, "end": v(-0.95, 21.44) * mm});
            skLineSegment(sketch, "E208.12.6.0", {"start": v(-2.95, 19.44) * mm, "end": v(-0.95, 19.44) * mm});
            skLineSegment(sketch, "E208.12.6.1", {"start": v(-2.95, 19.44) * mm, "end": v(-2.95, 17.44) * mm});
            skLineSegment(sketch, "E208.12.6.2", {"start": v(-2.95, 17.44) * mm, "end": v(-0.95, 17.44) * mm});
            skLineSegment(sketch, "E208.12.6.3", {"start": v(-0.95, 19.44) * mm, "end": v(-0.95, 17.44) * mm});
            skLineSegment(sketch, "E208.12.7.0", {"start": v(-2.95, 15.44) * mm, "end": v(-0.95, 15.44) * mm});
            skLineSegment(sketch, "E208.12.7.1", {"start": v(-2.95, 15.44) * mm, "end": v(-2.95, 13.44) * mm});
            skLineSegment(sketch, "E208.12.7.2", {"start": v(-2.95, 13.44) * mm, "end": v(-0.95, 13.44) * mm});
            skLineSegment(sketch, "E208.12.7.3", {"start": v(-0.95, 15.44) * mm, "end": v(-0.95, 13.44) * mm});
            skLineSegment(sketch, "E208.12.8.0", {"start": v(-2.95, 11.44) * mm, "end": v(-0.95, 11.44) * mm});
            skLineSegment(sketch, "E208.12.8.1", {"start": v(-2.95, 11.44) * mm, "end": v(-2.95, 9.44) * mm});
            skLineSegment(sketch, "E208.12.8.2", {"start": v(-2.95, 9.44) * mm, "end": v(-0.95, 9.44) * mm});
            skLineSegment(sketch, "E208.12.8.3", {"start": v(-0.95, 11.44) * mm, "end": v(-0.95, 9.44) * mm});
            skLineSegment(sketch, "E208.12.9.0", {"start": v(-2.95, 7.44) * mm, "end": v(-0.95, 7.44) * mm});
            skLineSegment(sketch, "E208.12.9.1", {"start": v(-2.95, 7.44) * mm, "end": v(-2.95, 5.44) * mm});
            skLineSegment(sketch, "E208.12.9.2", {"start": v(-2.95, 5.44) * mm, "end": v(-0.95, 5.44) * mm});
            skLineSegment(sketch, "E208.12.9.3", {"start": v(-0.95, 7.44) * mm, "end": v(-0.95, 5.44) * mm});
            skLineSegment(sketch, "E208.12.10.0", {"start": v(-2.95, 3.44) * mm, "end": v(-0.95, 3.44) * mm});
            skLineSegment(sketch, "E208.12.10.1", {"start": v(-2.95, 3.44) * mm, "end": v(-2.95, 1.44) * mm});
            skLineSegment(sketch, "E208.12.10.2", {"start": v(-2.95, 1.44) * mm, "end": v(-0.95, 1.44) * mm});
            skLineSegment(sketch, "E208.12.10.3", {"start": v(-0.95, 3.44) * mm, "end": v(-0.95, 1.44) * mm});
            skLineSegment(sketch, "E208.12.11.0", {"start": v(-2.95, -0.56) * mm, "end": v(-0.95, -0.56) * mm});
            skLineSegment(sketch, "E208.12.11.1", {"start": v(-2.95, -0.56) * mm, "end": v(-2.95, -2.56) * mm});
            skLineSegment(sketch, "E208.12.11.2", {"start": v(-2.95, -2.56) * mm, "end": v(-0.95, -2.56) * mm});
            skLineSegment(sketch, "E208.12.11.3", {"start": v(-0.95, -0.56) * mm, "end": v(-0.95, -2.56) * mm});
            skLineSegment(sketch, "E208.12.12.0", {"start": v(-2.95, -4.56) * mm, "end": v(-0.95, -4.56) * mm});
            skLineSegment(sketch, "E208.12.12.1", {"start": v(-2.95, -4.56) * mm, "end": v(-2.95, -6.56) * mm});
            skLineSegment(sketch, "E208.12.12.2", {"start": v(-2.95, -6.56) * mm, "end": v(-0.95, -6.56) * mm});
            skLineSegment(sketch, "E208.12.12.3", {"start": v(-0.95, -4.56) * mm, "end": v(-0.95, -6.56) * mm});
            skLineSegment(sketch, "E208.12.13.0", {"start": v(-2.95, -8.56) * mm, "end": v(-0.95, -8.56) * mm});
            skLineSegment(sketch, "E208.12.13.1", {"start": v(-2.95, -8.56) * mm, "end": v(-2.95, -10.56) * mm});
            skLineSegment(sketch, "E208.12.13.2", {"start": v(-2.95, -10.56) * mm, "end": v(-0.95, -10.56) * mm});
            skLineSegment(sketch, "E208.12.13.3", {"start": v(-0.95, -8.56) * mm, "end": v(-0.95, -10.56) * mm});
            skLineSegment(sketch, "E208.12.14.0", {"start": v(-2.95, -12.56) * mm, "end": v(-0.95, -12.56) * mm});
            skLineSegment(sketch, "E208.12.14.1", {"start": v(-2.95, -12.56) * mm, "end": v(-2.95, -14.56) * mm});
            skLineSegment(sketch, "E208.12.14.2", {"start": v(-2.95, -14.56) * mm, "end": v(-0.95, -14.56) * mm});
            skLineSegment(sketch, "E208.12.14.3", {"start": v(-0.95, -12.56) * mm, "end": v(-0.95, -14.56) * mm});
            skLineSegment(sketch, "E208.12.15.0", {"start": v(-2.95, -16.56) * mm, "end": v(-0.95, -16.56) * mm});
            skLineSegment(sketch, "E208.12.15.1", {"start": v(-2.95, -16.56) * mm, "end": v(-2.95, -18.56) * mm});
            skLineSegment(sketch, "E208.12.15.2", {"start": v(-2.95, -18.56) * mm, "end": v(-0.95, -18.56) * mm});
            skLineSegment(sketch, "E208.12.15.3", {"start": v(-0.95, -16.56) * mm, "end": v(-0.95, -18.56) * mm});
            skLineSegment(sketch, "E208.12.16.0", {"start": v(-2.95, -20.56) * mm, "end": v(-0.95, -20.56) * mm});
            skLineSegment(sketch, "E208.12.16.1", {"start": v(-2.95, -20.56) * mm, "end": v(-2.95, -22.56) * mm});
            skLineSegment(sketch, "E208.12.16.2", {"start": v(-2.95, -22.56) * mm, "end": v(-0.95, -22.56) * mm});
            skLineSegment(sketch, "E208.12.16.3", {"start": v(-0.95, -20.56) * mm, "end": v(-0.95, -22.56) * mm});
            skLineSegment(sketch, "E208.12.17.0", {"start": v(-2.95, -24.56) * mm, "end": v(-0.95, -24.56) * mm});
            skLineSegment(sketch, "E208.12.17.1", {"start": v(-2.95, -24.56) * mm, "end": v(-2.95, -26.56) * mm});
            skLineSegment(sketch, "E208.12.17.2", {"start": v(-2.95, -26.56) * mm, "end": v(-0.95, -26.56) * mm});
            skLineSegment(sketch, "E208.12.17.3", {"start": v(-0.95, -24.56) * mm, "end": v(-0.95, -26.56) * mm});
            skLineSegment(sketch, "E208.12.18.0", {"start": v(-2.95, -28.56) * mm, "end": v(-0.95, -28.56) * mm});
            skLineSegment(sketch, "E208.12.18.1", {"start": v(-2.95, -28.56) * mm, "end": v(-2.95, -30.56) * mm});
            skLineSegment(sketch, "E208.12.18.2", {"start": v(-2.95, -30.56) * mm, "end": v(-0.95, -30.56) * mm});
            skLineSegment(sketch, "E208.12.18.3", {"start": v(-0.95, -28.56) * mm, "end": v(-0.95, -30.56) * mm});
            skLineSegment(sketch, "E208.12.19.0", {"start": v(-2.95, -32.56) * mm, "end": v(-0.95, -32.56) * mm});
            skLineSegment(sketch, "E208.12.19.1", {"start": v(-2.95, -32.56) * mm, "end": v(-2.95, -34.56) * mm});
            skLineSegment(sketch, "E208.12.19.2", {"start": v(-2.95, -34.56) * mm, "end": v(-0.95, -34.56) * mm});
            skLineSegment(sketch, "E208.12.19.3", {"start": v(-0.95, -32.56) * mm, "end": v(-0.95, -34.56) * mm});
            skLineSegment(sketch, "E208.12.20.0", {"start": v(-2.95, -36.56) * mm, "end": v(-0.95, -36.56) * mm});
            skLineSegment(sketch, "E208.12.20.1", {"start": v(-2.95, -36.56) * mm, "end": v(-2.95, -38.56) * mm});
            skLineSegment(sketch, "E208.12.20.2", {"start": v(-2.95, -38.56) * mm, "end": v(-0.95, -38.56) * mm});
            skLineSegment(sketch, "E208.12.20.3", {"start": v(-0.95, -36.56) * mm, "end": v(-0.95, -38.56) * mm});
            skLineSegment(sketch, "E208.12.21.0", {"start": v(-2.95, -40.56) * mm, "end": v(-0.95, -40.56) * mm});
            skLineSegment(sketch, "E208.12.21.1", {"start": v(-2.95, -40.56) * mm, "end": v(-2.95, -42.56) * mm});
            skLineSegment(sketch, "E208.12.21.2", {"start": v(-2.95, -42.56) * mm, "end": v(-0.95, -42.56) * mm});
            skLineSegment(sketch, "E208.12.21.3", {"start": v(-0.95, -40.56) * mm, "end": v(-0.95, -42.56) * mm});
            skLineSegment(sketch, "E208.13.0.0", {"start": v(1.05, 43.44) * mm, "end": v(3.05, 43.44) * mm});
            skLineSegment(sketch, "E208.13.0.1", {"start": v(1.05, 43.44) * mm, "end": v(1.05, 41.44) * mm});
            skLineSegment(sketch, "E208.13.0.2", {"start": v(1.05, 41.44) * mm, "end": v(3.05, 41.44) * mm});
            skLineSegment(sketch, "E208.13.0.3", {"start": v(3.05, 43.44) * mm, "end": v(3.05, 41.44) * mm});
            skLineSegment(sketch, "E208.13.1.0", {"start": v(1.05, 39.44) * mm, "end": v(3.05, 39.44) * mm});
            skLineSegment(sketch, "E208.13.1.1", {"start": v(1.05, 39.44) * mm, "end": v(1.05, 37.44) * mm});
            skLineSegment(sketch, "E208.13.1.2", {"start": v(1.05, 37.44) * mm, "end": v(3.05, 37.44) * mm});
            skLineSegment(sketch, "E208.13.1.3", {"start": v(3.05, 39.44) * mm, "end": v(3.05, 37.44) * mm});
            skLineSegment(sketch, "E208.13.2.0", {"start": v(1.05, 35.44) * mm, "end": v(3.05, 35.44) * mm});
            skLineSegment(sketch, "E208.13.2.1", {"start": v(1.05, 35.44) * mm, "end": v(1.05, 33.44) * mm});
            skLineSegment(sketch, "E208.13.2.2", {"start": v(1.05, 33.44) * mm, "end": v(3.05, 33.44) * mm});
            skLineSegment(sketch, "E208.13.2.3", {"start": v(3.05, 35.44) * mm, "end": v(3.05, 33.44) * mm});
            skLineSegment(sketch, "E208.13.3.0", {"start": v(1.05, 31.44) * mm, "end": v(3.05, 31.44) * mm});
            skLineSegment(sketch, "E208.13.3.1", {"start": v(1.05, 31.44) * mm, "end": v(1.05, 29.44) * mm});
            skLineSegment(sketch, "E208.13.3.2", {"start": v(1.05, 29.44) * mm, "end": v(3.05, 29.44) * mm});
            skLineSegment(sketch, "E208.13.3.3", {"start": v(3.05, 31.44) * mm, "end": v(3.05, 29.44) * mm});
            skLineSegment(sketch, "E208.13.4.0", {"start": v(1.05, 27.44) * mm, "end": v(3.05, 27.44) * mm});
            skLineSegment(sketch, "E208.13.4.1", {"start": v(1.05, 27.44) * mm, "end": v(1.05, 25.44) * mm});
            skLineSegment(sketch, "E208.13.4.2", {"start": v(1.05, 25.44) * mm, "end": v(3.05, 25.44) * mm});
            skLineSegment(sketch, "E208.13.4.3", {"start": v(3.05, 27.44) * mm, "end": v(3.05, 25.44) * mm});
            skLineSegment(sketch, "E208.13.5.0", {"start": v(1.05, 23.44) * mm, "end": v(3.05, 23.44) * mm});
            skLineSegment(sketch, "E208.13.5.1", {"start": v(1.05, 23.44) * mm, "end": v(1.05, 21.44) * mm});
            skLineSegment(sketch, "E208.13.5.2", {"start": v(1.05, 21.44) * mm, "end": v(3.05, 21.44) * mm});
            skLineSegment(sketch, "E208.13.5.3", {"start": v(3.05, 23.44) * mm, "end": v(3.05, 21.44) * mm});
            skLineSegment(sketch, "E208.13.6.0", {"start": v(1.05, 19.44) * mm, "end": v(3.05, 19.44) * mm});
            skLineSegment(sketch, "E208.13.6.1", {"start": v(1.05, 19.44) * mm, "end": v(1.05, 17.44) * mm});
            skLineSegment(sketch, "E208.13.6.2", {"start": v(1.05, 17.44) * mm, "end": v(3.05, 17.44) * mm});
            skLineSegment(sketch, "E208.13.6.3", {"start": v(3.05, 19.44) * mm, "end": v(3.05, 17.44) * mm});
            skLineSegment(sketch, "E208.13.7.0", {"start": v(1.05, 15.44) * mm, "end": v(3.05, 15.44) * mm});
            skLineSegment(sketch, "E208.13.7.1", {"start": v(1.05, 15.44) * mm, "end": v(1.05, 13.44) * mm});
            skLineSegment(sketch, "E208.13.7.2", {"start": v(1.05, 13.44) * mm, "end": v(3.05, 13.44) * mm});
            skLineSegment(sketch, "E208.13.7.3", {"start": v(3.05, 15.44) * mm, "end": v(3.05, 13.44) * mm});
            skLineSegment(sketch, "E208.13.8.0", {"start": v(1.05, 11.44) * mm, "end": v(3.05, 11.44) * mm});
            skLineSegment(sketch, "E208.13.8.1", {"start": v(1.05, 11.44) * mm, "end": v(1.05, 9.44) * mm});
            skLineSegment(sketch, "E208.13.8.2", {"start": v(1.05, 9.44) * mm, "end": v(3.05, 9.44) * mm});
            skLineSegment(sketch, "E208.13.8.3", {"start": v(3.05, 11.44) * mm, "end": v(3.05, 9.44) * mm});
            skLineSegment(sketch, "E208.13.9.0", {"start": v(1.05, 7.44) * mm, "end": v(3.05, 7.44) * mm});
            skLineSegment(sketch, "E208.13.9.1", {"start": v(1.05, 7.44) * mm, "end": v(1.05, 5.44) * mm});
            skLineSegment(sketch, "E208.13.9.2", {"start": v(1.05, 5.44) * mm, "end": v(3.05, 5.44) * mm});
            skLineSegment(sketch, "E208.13.9.3", {"start": v(3.05, 7.44) * mm, "end": v(3.05, 5.44) * mm});
            skLineSegment(sketch, "E208.13.10.0", {"start": v(1.05, 3.44) * mm, "end": v(3.05, 3.44) * mm});
            skLineSegment(sketch, "E208.13.10.1", {"start": v(1.05, 3.44) * mm, "end": v(1.05, 1.44) * mm});
            skLineSegment(sketch, "E208.13.10.2", {"start": v(1.05, 1.44) * mm, "end": v(3.05, 1.44) * mm});
            skLineSegment(sketch, "E208.13.10.3", {"start": v(3.05, 3.44) * mm, "end": v(3.05, 1.44) * mm});
            skLineSegment(sketch, "E208.13.11.0", {"start": v(1.05, -0.56) * mm, "end": v(3.05, -0.56) * mm});
            skLineSegment(sketch, "E208.13.11.1", {"start": v(1.05, -0.56) * mm, "end": v(1.05, -2.56) * mm});
            skLineSegment(sketch, "E208.13.11.2", {"start": v(1.05, -2.56) * mm, "end": v(3.05, -2.56) * mm});
            skLineSegment(sketch, "E208.13.11.3", {"start": v(3.05, -0.56) * mm, "end": v(3.05, -2.56) * mm});
            skLineSegment(sketch, "E208.13.12.0", {"start": v(1.05, -4.56) * mm, "end": v(3.05, -4.56) * mm});
            skLineSegment(sketch, "E208.13.12.1", {"start": v(1.05, -4.56) * mm, "end": v(1.05, -6.56) * mm});
            skLineSegment(sketch, "E208.13.12.2", {"start": v(1.05, -6.56) * mm, "end": v(3.05, -6.56) * mm});
            skLineSegment(sketch, "E208.13.12.3", {"start": v(3.05, -4.56) * mm, "end": v(3.05, -6.56) * mm});
            skLineSegment(sketch, "E208.13.13.0", {"start": v(1.05, -8.56) * mm, "end": v(3.05, -8.56) * mm});
            skLineSegment(sketch, "E208.13.13.1", {"start": v(1.05, -8.56) * mm, "end": v(1.05, -10.56) * mm});
            skLineSegment(sketch, "E208.13.13.2", {"start": v(1.05, -10.56) * mm, "end": v(3.05, -10.56) * mm});
            skLineSegment(sketch, "E208.13.13.3", {"start": v(3.05, -8.56) * mm, "end": v(3.05, -10.56) * mm});
            skLineSegment(sketch, "E208.13.14.0", {"start": v(1.05, -12.56) * mm, "end": v(3.05, -12.56) * mm});
            skLineSegment(sketch, "E208.13.14.1", {"start": v(1.05, -12.56) * mm, "end": v(1.05, -14.56) * mm});
            skLineSegment(sketch, "E208.13.14.2", {"start": v(1.05, -14.56) * mm, "end": v(3.05, -14.56) * mm});
            skLineSegment(sketch, "E208.13.14.3", {"start": v(3.05, -12.56) * mm, "end": v(3.05, -14.56) * mm});
            skLineSegment(sketch, "E208.13.15.0", {"start": v(1.05, -16.56) * mm, "end": v(3.05, -16.56) * mm});
            skLineSegment(sketch, "E208.13.15.1", {"start": v(1.05, -16.56) * mm, "end": v(1.05, -18.56) * mm});
            skLineSegment(sketch, "E208.13.15.2", {"start": v(1.05, -18.56) * mm, "end": v(3.05, -18.56) * mm});
            skLineSegment(sketch, "E208.13.15.3", {"start": v(3.05, -16.56) * mm, "end": v(3.05, -18.56) * mm});
            skLineSegment(sketch, "E208.13.16.0", {"start": v(1.05, -20.56) * mm, "end": v(3.05, -20.56) * mm});
            skLineSegment(sketch, "E208.13.16.1", {"start": v(1.05, -20.56) * mm, "end": v(1.05, -22.56) * mm});
            skLineSegment(sketch, "E208.13.16.2", {"start": v(1.05, -22.56) * mm, "end": v(3.05, -22.56) * mm});
            skLineSegment(sketch, "E208.13.16.3", {"start": v(3.05, -20.56) * mm, "end": v(3.05, -22.56) * mm});
            skLineSegment(sketch, "E208.13.17.0", {"start": v(1.05, -24.56) * mm, "end": v(3.05, -24.56) * mm});
            skLineSegment(sketch, "E208.13.17.1", {"start": v(1.05, -24.56) * mm, "end": v(1.05, -26.56) * mm});
            skLineSegment(sketch, "E208.13.17.2", {"start": v(1.05, -26.56) * mm, "end": v(3.05, -26.56) * mm});
            skLineSegment(sketch, "E208.13.17.3", {"start": v(3.05, -24.56) * mm, "end": v(3.05, -26.56) * mm});
            skLineSegment(sketch, "E208.13.18.0", {"start": v(1.05, -28.56) * mm, "end": v(3.05, -28.56) * mm});
            skLineSegment(sketch, "E208.13.18.1", {"start": v(1.05, -28.56) * mm, "end": v(1.05, -30.56) * mm});
            skLineSegment(sketch, "E208.13.18.2", {"start": v(1.05, -30.56) * mm, "end": v(3.05, -30.56) * mm});
            skLineSegment(sketch, "E208.13.18.3", {"start": v(3.05, -28.56) * mm, "end": v(3.05, -30.56) * mm});
            skLineSegment(sketch, "E208.13.19.0", {"start": v(1.05, -32.56) * mm, "end": v(3.05, -32.56) * mm});
            skLineSegment(sketch, "E208.13.19.1", {"start": v(1.05, -32.56) * mm, "end": v(1.05, -34.56) * mm});
            skLineSegment(sketch, "E208.13.19.2", {"start": v(1.05, -34.56) * mm, "end": v(3.05, -34.56) * mm});
            skLineSegment(sketch, "E208.13.19.3", {"start": v(3.05, -32.56) * mm, "end": v(3.05, -34.56) * mm});
            skLineSegment(sketch, "E208.13.20.0", {"start": v(1.05, -36.56) * mm, "end": v(3.05, -36.56) * mm});
            skLineSegment(sketch, "E208.13.20.1", {"start": v(1.05, -36.56) * mm, "end": v(1.05, -38.56) * mm});
            skLineSegment(sketch, "E208.13.20.2", {"start": v(1.05, -38.56) * mm, "end": v(3.05, -38.56) * mm});
            skLineSegment(sketch, "E208.13.20.3", {"start": v(3.05, -36.56) * mm, "end": v(3.05, -38.56) * mm});
            skLineSegment(sketch, "E208.13.21.0", {"start": v(1.05, -40.56) * mm, "end": v(3.05, -40.56) * mm});
            skLineSegment(sketch, "E208.13.21.1", {"start": v(1.05, -40.56) * mm, "end": v(1.05, -42.56) * mm});
            skLineSegment(sketch, "E208.13.21.2", {"start": v(1.05, -42.56) * mm, "end": v(3.05, -42.56) * mm});
            skLineSegment(sketch, "E208.13.21.3", {"start": v(3.05, -40.56) * mm, "end": v(3.05, -42.56) * mm});
            skLineSegment(sketch, "E208.14.0.0", {"start": v(5.05, 43.44) * mm, "end": v(7.05, 43.44) * mm});
            skLineSegment(sketch, "E208.14.0.1", {"start": v(5.05, 43.44) * mm, "end": v(5.05, 41.44) * mm});
            skLineSegment(sketch, "E208.14.0.2", {"start": v(5.05, 41.44) * mm, "end": v(7.05, 41.44) * mm});
            skLineSegment(sketch, "E208.14.0.3", {"start": v(7.05, 43.44) * mm, "end": v(7.05, 41.44) * mm});
            skLineSegment(sketch, "E208.14.1.0", {"start": v(5.05, 39.44) * mm, "end": v(7.05, 39.44) * mm});
            skLineSegment(sketch, "E208.14.1.1", {"start": v(5.05, 39.44) * mm, "end": v(5.05, 37.44) * mm});
            skLineSegment(sketch, "E208.14.1.2", {"start": v(5.05, 37.44) * mm, "end": v(7.05, 37.44) * mm});
            skLineSegment(sketch, "E208.14.1.3", {"start": v(7.05, 39.44) * mm, "end": v(7.05, 37.44) * mm});
            skLineSegment(sketch, "E208.14.2.0", {"start": v(5.05, 35.44) * mm, "end": v(7.05, 35.44) * mm});
            skLineSegment(sketch, "E208.14.2.1", {"start": v(5.05, 35.44) * mm, "end": v(5.05, 33.44) * mm});
            skLineSegment(sketch, "E208.14.2.2", {"start": v(5.05, 33.44) * mm, "end": v(7.05, 33.44) * mm});
            skLineSegment(sketch, "E208.14.2.3", {"start": v(7.05, 35.44) * mm, "end": v(7.05, 33.44) * mm});
            skLineSegment(sketch, "E208.14.3.0", {"start": v(5.05, 31.44) * mm, "end": v(7.05, 31.44) * mm});
            skLineSegment(sketch, "E208.14.3.1", {"start": v(5.05, 31.44) * mm, "end": v(5.05, 29.44) * mm});
            skLineSegment(sketch, "E208.14.3.2", {"start": v(5.05, 29.44) * mm, "end": v(7.05, 29.44) * mm});
            skLineSegment(sketch, "E208.14.3.3", {"start": v(7.05, 31.44) * mm, "end": v(7.05, 29.44) * mm});
            skLineSegment(sketch, "E208.14.4.0", {"start": v(5.05, 27.44) * mm, "end": v(7.05, 27.44) * mm});
            skLineSegment(sketch, "E208.14.4.1", {"start": v(5.05, 27.44) * mm, "end": v(5.05, 25.44) * mm});
            skLineSegment(sketch, "E208.14.4.2", {"start": v(5.05, 25.44) * mm, "end": v(7.05, 25.44) * mm});
            skLineSegment(sketch, "E208.14.4.3", {"start": v(7.05, 27.44) * mm, "end": v(7.05, 25.44) * mm});
            skLineSegment(sketch, "E208.14.5.0", {"start": v(5.05, 23.44) * mm, "end": v(7.05, 23.44) * mm});
            skLineSegment(sketch, "E208.14.5.1", {"start": v(5.05, 23.44) * mm, "end": v(5.05, 21.44) * mm});
            skLineSegment(sketch, "E208.14.5.2", {"start": v(5.05, 21.44) * mm, "end": v(7.05, 21.44) * mm});
            skLineSegment(sketch, "E208.14.5.3", {"start": v(7.05, 23.44) * mm, "end": v(7.05, 21.44) * mm});
            skLineSegment(sketch, "E208.14.6.0", {"start": v(5.05, 19.44) * mm, "end": v(7.05, 19.44) * mm});
            skLineSegment(sketch, "E208.14.6.1", {"start": v(5.05, 19.44) * mm, "end": v(5.05, 17.44) * mm});
            skLineSegment(sketch, "E208.14.6.2", {"start": v(5.05, 17.44) * mm, "end": v(7.05, 17.44) * mm});
            skLineSegment(sketch, "E208.14.6.3", {"start": v(7.05, 19.44) * mm, "end": v(7.05, 17.44) * mm});
            skLineSegment(sketch, "E208.14.7.0", {"start": v(5.05, 15.44) * mm, "end": v(7.05, 15.44) * mm});
            skLineSegment(sketch, "E208.14.7.1", {"start": v(5.05, 15.44) * mm, "end": v(5.05, 13.44) * mm});
            skLineSegment(sketch, "E208.14.7.2", {"start": v(5.05, 13.44) * mm, "end": v(7.05, 13.44) * mm});
            skLineSegment(sketch, "E208.14.7.3", {"start": v(7.05, 15.44) * mm, "end": v(7.05, 13.44) * mm});
            skLineSegment(sketch, "E208.14.8.0", {"start": v(5.05, 11.44) * mm, "end": v(7.05, 11.44) * mm});
            skLineSegment(sketch, "E208.14.8.1", {"start": v(5.05, 11.44) * mm, "end": v(5.05, 9.44) * mm});
            skLineSegment(sketch, "E208.14.8.2", {"start": v(5.05, 9.44) * mm, "end": v(7.05, 9.44) * mm});
            skLineSegment(sketch, "E208.14.8.3", {"start": v(7.05, 11.44) * mm, "end": v(7.05, 9.44) * mm});
            skLineSegment(sketch, "E208.14.9.0", {"start": v(5.05, 7.44) * mm, "end": v(7.05, 7.44) * mm});
            skLineSegment(sketch, "E208.14.9.1", {"start": v(5.05, 7.44) * mm, "end": v(5.05, 5.44) * mm});
            skLineSegment(sketch, "E208.14.9.2", {"start": v(5.05, 5.44) * mm, "end": v(7.05, 5.44) * mm});
            skLineSegment(sketch, "E208.14.9.3", {"start": v(7.05, 7.44) * mm, "end": v(7.05, 5.44) * mm});
            skLineSegment(sketch, "E208.14.10.0", {"start": v(5.05, 3.44) * mm, "end": v(7.05, 3.44) * mm});
            skLineSegment(sketch, "E208.14.10.1", {"start": v(5.05, 3.44) * mm, "end": v(5.05, 1.44) * mm});
            skLineSegment(sketch, "E208.14.10.2", {"start": v(5.05, 1.44) * mm, "end": v(7.05, 1.44) * mm});
            skLineSegment(sketch, "E208.14.10.3", {"start": v(7.05, 3.44) * mm, "end": v(7.05, 1.44) * mm});
            skLineSegment(sketch, "E208.14.11.0", {"start": v(5.05, -0.56) * mm, "end": v(7.05, -0.56) * mm});
            skLineSegment(sketch, "E208.14.11.1", {"start": v(5.05, -0.56) * mm, "end": v(5.05, -2.56) * mm});
            skLineSegment(sketch, "E208.14.11.2", {"start": v(5.05, -2.56) * mm, "end": v(7.05, -2.56) * mm});
            skLineSegment(sketch, "E208.14.11.3", {"start": v(7.05, -0.56) * mm, "end": v(7.05, -2.56) * mm});
            skLineSegment(sketch, "E208.14.12.0", {"start": v(5.05, -4.56) * mm, "end": v(7.05, -4.56) * mm});
            skLineSegment(sketch, "E208.14.12.1", {"start": v(5.05, -4.56) * mm, "end": v(5.05, -6.56) * mm});
            skLineSegment(sketch, "E208.14.12.2", {"start": v(5.05, -6.56) * mm, "end": v(7.05, -6.56) * mm});
            skLineSegment(sketch, "E208.14.12.3", {"start": v(7.05, -4.56) * mm, "end": v(7.05, -6.56) * mm});
            skLineSegment(sketch, "E208.14.13.0", {"start": v(5.05, -8.56) * mm, "end": v(7.05, -8.56) * mm});
            skLineSegment(sketch, "E208.14.13.1", {"start": v(5.05, -8.56) * mm, "end": v(5.05, -10.56) * mm});
            skLineSegment(sketch, "E208.14.13.2", {"start": v(5.05, -10.56) * mm, "end": v(7.05, -10.56) * mm});
            skLineSegment(sketch, "E208.14.13.3", {"start": v(7.05, -8.56) * mm, "end": v(7.05, -10.56) * mm});
            skLineSegment(sketch, "E208.14.14.0", {"start": v(5.05, -12.56) * mm, "end": v(7.05, -12.56) * mm});
            skLineSegment(sketch, "E208.14.14.1", {"start": v(5.05, -12.56) * mm, "end": v(5.05, -14.56) * mm});
            skLineSegment(sketch, "E208.14.14.2", {"start": v(5.05, -14.56) * mm, "end": v(7.05, -14.56) * mm});
            skLineSegment(sketch, "E208.14.14.3", {"start": v(7.05, -12.56) * mm, "end": v(7.05, -14.56) * mm});
            skLineSegment(sketch, "E208.14.15.0", {"start": v(5.05, -16.56) * mm, "end": v(7.05, -16.56) * mm});
            skLineSegment(sketch, "E208.14.15.1", {"start": v(5.05, -16.56) * mm, "end": v(5.05, -18.56) * mm});
            skLineSegment(sketch, "E208.14.15.2", {"start": v(5.05, -18.56) * mm, "end": v(7.05, -18.56) * mm});
            skLineSegment(sketch, "E208.14.15.3", {"start": v(7.05, -16.56) * mm, "end": v(7.05, -18.56) * mm});
            skLineSegment(sketch, "E208.14.16.0", {"start": v(5.05, -20.56) * mm, "end": v(7.05, -20.56) * mm});
            skLineSegment(sketch, "E208.14.16.1", {"start": v(5.05, -20.56) * mm, "end": v(5.05, -22.56) * mm});
            skLineSegment(sketch, "E208.14.16.2", {"start": v(5.05, -22.56) * mm, "end": v(7.05, -22.56) * mm});
            skLineSegment(sketch, "E208.14.16.3", {"start": v(7.05, -20.56) * mm, "end": v(7.05, -22.56) * mm});
            skLineSegment(sketch, "E208.14.17.0", {"start": v(5.05, -24.56) * mm, "end": v(7.05, -24.56) * mm});
            skLineSegment(sketch, "E208.14.17.1", {"start": v(5.05, -24.56) * mm, "end": v(5.05, -26.56) * mm});
            skLineSegment(sketch, "E208.14.17.2", {"start": v(5.05, -26.56) * mm, "end": v(7.05, -26.56) * mm});
            skLineSegment(sketch, "E208.14.17.3", {"start": v(7.05, -24.56) * mm, "end": v(7.05, -26.56) * mm});
            skLineSegment(sketch, "E208.14.18.0", {"start": v(5.05, -28.56) * mm, "end": v(7.05, -28.56) * mm});
            skLineSegment(sketch, "E208.14.18.1", {"start": v(5.05, -28.56) * mm, "end": v(5.05, -30.56) * mm});
            skLineSegment(sketch, "E208.14.18.2", {"start": v(5.05, -30.56) * mm, "end": v(7.05, -30.56) * mm});
            skLineSegment(sketch, "E208.14.18.3", {"start": v(7.05, -28.56) * mm, "end": v(7.05, -30.56) * mm});
            skLineSegment(sketch, "E208.14.19.0", {"start": v(5.05, -32.56) * mm, "end": v(7.05, -32.56) * mm});
            skLineSegment(sketch, "E208.14.19.1", {"start": v(5.05, -32.56) * mm, "end": v(5.05, -34.56) * mm});
            skLineSegment(sketch, "E208.14.19.2", {"start": v(5.05, -34.56) * mm, "end": v(7.05, -34.56) * mm});
            skLineSegment(sketch, "E208.14.19.3", {"start": v(7.05, -32.56) * mm, "end": v(7.05, -34.56) * mm});
            skLineSegment(sketch, "E208.14.20.0", {"start": v(5.05, -36.56) * mm, "end": v(7.05, -36.56) * mm});
            skLineSegment(sketch, "E208.14.20.1", {"start": v(5.05, -36.56) * mm, "end": v(5.05, -38.56) * mm});
            skLineSegment(sketch, "E208.14.20.2", {"start": v(5.05, -38.56) * mm, "end": v(7.05, -38.56) * mm});
            skLineSegment(sketch, "E208.14.20.3", {"start": v(7.05, -36.56) * mm, "end": v(7.05, -38.56) * mm});
            skLineSegment(sketch, "E208.14.21.0", {"start": v(5.05, -40.56) * mm, "end": v(7.05, -40.56) * mm});
            skLineSegment(sketch, "E208.14.21.1", {"start": v(5.05, -40.56) * mm, "end": v(5.05, -42.56) * mm});
            skLineSegment(sketch, "E208.14.21.2", {"start": v(5.05, -42.56) * mm, "end": v(7.05, -42.56) * mm});
            skLineSegment(sketch, "E208.14.21.3", {"start": v(7.05, -40.56) * mm, "end": v(7.05, -42.56) * mm});
            skLineSegment(sketch, "E208.15.0.0", {"start": v(9.05, 43.44) * mm, "end": v(11.05, 43.44) * mm});
            skLineSegment(sketch, "E208.15.0.1", {"start": v(9.05, 43.44) * mm, "end": v(9.05, 41.44) * mm});
            skLineSegment(sketch, "E208.15.0.2", {"start": v(9.05, 41.44) * mm, "end": v(11.05, 41.44) * mm});
            skLineSegment(sketch, "E208.15.0.3", {"start": v(11.05, 43.44) * mm, "end": v(11.05, 41.44) * mm});
            skLineSegment(sketch, "E208.15.1.0", {"start": v(9.05, 39.44) * mm, "end": v(11.05, 39.44) * mm});
            skLineSegment(sketch, "E208.15.1.1", {"start": v(9.05, 39.44) * mm, "end": v(9.05, 37.44) * mm});
            skLineSegment(sketch, "E208.15.1.2", {"start": v(9.05, 37.44) * mm, "end": v(11.05, 37.44) * mm});
            skLineSegment(sketch, "E208.15.1.3", {"start": v(11.05, 39.44) * mm, "end": v(11.05, 37.44) * mm});
            skLineSegment(sketch, "E208.15.2.0", {"start": v(9.05, 35.44) * mm, "end": v(11.05, 35.44) * mm});
            skLineSegment(sketch, "E208.15.2.1", {"start": v(9.05, 35.44) * mm, "end": v(9.05, 33.44) * mm});
            skLineSegment(sketch, "E208.15.2.2", {"start": v(9.05, 33.44) * mm, "end": v(11.05, 33.44) * mm});
            skLineSegment(sketch, "E208.15.2.3", {"start": v(11.05, 35.44) * mm, "end": v(11.05, 33.44) * mm});
            skLineSegment(sketch, "E208.15.3.0", {"start": v(9.05, 31.44) * mm, "end": v(11.05, 31.44) * mm});
            skLineSegment(sketch, "E208.15.3.1", {"start": v(9.05, 31.44) * mm, "end": v(9.05, 29.44) * mm});
            skLineSegment(sketch, "E208.15.3.2", {"start": v(9.05, 29.44) * mm, "end": v(11.05, 29.44) * mm});
            skLineSegment(sketch, "E208.15.3.3", {"start": v(11.05, 31.44) * mm, "end": v(11.05, 29.44) * mm});
            skLineSegment(sketch, "E208.15.4.0", {"start": v(9.05, 27.44) * mm, "end": v(11.05, 27.44) * mm});
            skLineSegment(sketch, "E208.15.4.1", {"start": v(9.05, 27.44) * mm, "end": v(9.05, 25.44) * mm});
            skLineSegment(sketch, "E208.15.4.2", {"start": v(9.05, 25.44) * mm, "end": v(11.05, 25.44) * mm});
            skLineSegment(sketch, "E208.15.4.3", {"start": v(11.05, 27.44) * mm, "end": v(11.05, 25.44) * mm});
            skLineSegment(sketch, "E208.15.5.0", {"start": v(9.05, 23.44) * mm, "end": v(11.05, 23.44) * mm});
            skLineSegment(sketch, "E208.15.5.1", {"start": v(9.05, 23.44) * mm, "end": v(9.05, 21.44) * mm});
            skLineSegment(sketch, "E208.15.5.2", {"start": v(9.05, 21.44) * mm, "end": v(11.05, 21.44) * mm});
            skLineSegment(sketch, "E208.15.5.3", {"start": v(11.05, 23.44) * mm, "end": v(11.05, 21.44) * mm});
            skLineSegment(sketch, "E208.15.6.0", {"start": v(9.05, 19.44) * mm, "end": v(11.05, 19.44) * mm});
            skLineSegment(sketch, "E208.15.6.1", {"start": v(9.05, 19.44) * mm, "end": v(9.05, 17.44) * mm});
            skLineSegment(sketch, "E208.15.6.2", {"start": v(9.05, 17.44) * mm, "end": v(11.05, 17.44) * mm});
            skLineSegment(sketch, "E208.15.6.3", {"start": v(11.05, 19.44) * mm, "end": v(11.05, 17.44) * mm});
            skLineSegment(sketch, "E208.15.7.0", {"start": v(9.05, 15.44) * mm, "end": v(11.05, 15.44) * mm});
            skLineSegment(sketch, "E208.15.7.1", {"start": v(9.05, 15.44) * mm, "end": v(9.05, 13.44) * mm});
            skLineSegment(sketch, "E208.15.7.2", {"start": v(9.05, 13.44) * mm, "end": v(11.05, 13.44) * mm});
            skLineSegment(sketch, "E208.15.7.3", {"start": v(11.05, 15.44) * mm, "end": v(11.05, 13.44) * mm});
            skLineSegment(sketch, "E208.15.8.0", {"start": v(9.05, 11.44) * mm, "end": v(11.05, 11.44) * mm});
            skLineSegment(sketch, "E208.15.8.1", {"start": v(9.05, 11.44) * mm, "end": v(9.05, 9.44) * mm});
            skLineSegment(sketch, "E208.15.8.2", {"start": v(9.05, 9.44) * mm, "end": v(11.05, 9.44) * mm});
            skLineSegment(sketch, "E208.15.8.3", {"start": v(11.05, 11.44) * mm, "end": v(11.05, 9.44) * mm});
            skLineSegment(sketch, "E208.15.9.0", {"start": v(9.05, 7.44) * mm, "end": v(11.05, 7.44) * mm});
            skLineSegment(sketch, "E208.15.9.1", {"start": v(9.05, 7.44) * mm, "end": v(9.05, 5.44) * mm});
            skLineSegment(sketch, "E208.15.9.2", {"start": v(9.05, 5.44) * mm, "end": v(11.05, 5.44) * mm});
            skLineSegment(sketch, "E208.15.9.3", {"start": v(11.05, 7.44) * mm, "end": v(11.05, 5.44) * mm});
            skLineSegment(sketch, "E208.15.10.0", {"start": v(9.05, 3.44) * mm, "end": v(11.05, 3.44) * mm});
            skLineSegment(sketch, "E208.15.10.1", {"start": v(9.05, 3.44) * mm, "end": v(9.05, 1.44) * mm});
            skLineSegment(sketch, "E208.15.10.2", {"start": v(9.05, 1.44) * mm, "end": v(11.05, 1.44) * mm});
            skLineSegment(sketch, "E208.15.10.3", {"start": v(11.05, 3.44) * mm, "end": v(11.05, 1.44) * mm});
            skLineSegment(sketch, "E208.15.11.0", {"start": v(9.05, -0.56) * mm, "end": v(11.05, -0.56) * mm});
            skLineSegment(sketch, "E208.15.11.1", {"start": v(9.05, -0.56) * mm, "end": v(9.05, -2.56) * mm});
            skLineSegment(sketch, "E208.15.11.2", {"start": v(9.05, -2.56) * mm, "end": v(11.05, -2.56) * mm});
            skLineSegment(sketch, "E208.15.11.3", {"start": v(11.05, -0.56) * mm, "end": v(11.05, -2.56) * mm});
            skLineSegment(sketch, "E208.15.12.0", {"start": v(9.05, -4.56) * mm, "end": v(11.05, -4.56) * mm});
            skLineSegment(sketch, "E208.15.12.1", {"start": v(9.05, -4.56) * mm, "end": v(9.05, -6.56) * mm});
            skLineSegment(sketch, "E208.15.12.2", {"start": v(9.05, -6.56) * mm, "end": v(11.05, -6.56) * mm});
            skLineSegment(sketch, "E208.15.12.3", {"start": v(11.05, -4.56) * mm, "end": v(11.05, -6.56) * mm});
            skLineSegment(sketch, "E208.15.13.0", {"start": v(9.05, -8.56) * mm, "end": v(11.05, -8.56) * mm});
            skLineSegment(sketch, "E208.15.13.1", {"start": v(9.05, -8.56) * mm, "end": v(9.05, -10.56) * mm});
            skLineSegment(sketch, "E208.15.13.2", {"start": v(9.05, -10.56) * mm, "end": v(11.05, -10.56) * mm});
            skLineSegment(sketch, "E208.15.13.3", {"start": v(11.05, -8.56) * mm, "end": v(11.05, -10.56) * mm});
            skLineSegment(sketch, "E208.15.14.0", {"start": v(9.05, -12.56) * mm, "end": v(11.05, -12.56) * mm});
            skLineSegment(sketch, "E208.15.14.1", {"start": v(9.05, -12.56) * mm, "end": v(9.05, -14.56) * mm});
            skLineSegment(sketch, "E208.15.14.2", {"start": v(9.05, -14.56) * mm, "end": v(11.05, -14.56) * mm});
            skLineSegment(sketch, "E208.15.14.3", {"start": v(11.05, -12.56) * mm, "end": v(11.05, -14.56) * mm});
            skLineSegment(sketch, "E208.15.15.0", {"start": v(9.05, -16.56) * mm, "end": v(11.05, -16.56) * mm});
            skLineSegment(sketch, "E208.15.15.1", {"start": v(9.05, -16.56) * mm, "end": v(9.05, -18.56) * mm});
            skLineSegment(sketch, "E208.15.15.2", {"start": v(9.05, -18.56) * mm, "end": v(11.05, -18.56) * mm});
            skLineSegment(sketch, "E208.15.15.3", {"start": v(11.05, -16.56) * mm, "end": v(11.05, -18.56) * mm});
            skLineSegment(sketch, "E208.15.16.0", {"start": v(9.05, -20.56) * mm, "end": v(11.05, -20.56) * mm});
            skLineSegment(sketch, "E208.15.16.1", {"start": v(9.05, -20.56) * mm, "end": v(9.05, -22.56) * mm});
            skLineSegment(sketch, "E208.15.16.2", {"start": v(9.05, -22.56) * mm, "end": v(11.05, -22.56) * mm});
            skLineSegment(sketch, "E208.15.16.3", {"start": v(11.05, -20.56) * mm, "end": v(11.05, -22.56) * mm});
            skLineSegment(sketch, "E208.15.17.0", {"start": v(9.05, -24.56) * mm, "end": v(11.05, -24.56) * mm});
            skLineSegment(sketch, "E208.15.17.1", {"start": v(9.05, -24.56) * mm, "end": v(9.05, -26.56) * mm});
            skLineSegment(sketch, "E208.15.17.2", {"start": v(9.05, -26.56) * mm, "end": v(11.05, -26.56) * mm});
            skLineSegment(sketch, "E208.15.17.3", {"start": v(11.05, -24.56) * mm, "end": v(11.05, -26.56) * mm});
            skLineSegment(sketch, "E208.15.18.0", {"start": v(9.05, -28.56) * mm, "end": v(11.05, -28.56) * mm});
            skLineSegment(sketch, "E208.15.18.1", {"start": v(9.05, -28.56) * mm, "end": v(9.05, -30.56) * mm});
            skLineSegment(sketch, "E208.15.18.2", {"start": v(9.05, -30.56) * mm, "end": v(11.05, -30.56) * mm});
            skLineSegment(sketch, "E208.15.18.3", {"start": v(11.05, -28.56) * mm, "end": v(11.05, -30.56) * mm});
            skLineSegment(sketch, "E208.15.19.0", {"start": v(9.05, -32.56) * mm, "end": v(11.05, -32.56) * mm});
            skLineSegment(sketch, "E208.15.19.1", {"start": v(9.05, -32.56) * mm, "end": v(9.05, -34.56) * mm});
            skLineSegment(sketch, "E208.15.19.2", {"start": v(9.05, -34.56) * mm, "end": v(11.05, -34.56) * mm});
            skLineSegment(sketch, "E208.15.19.3", {"start": v(11.05, -32.56) * mm, "end": v(11.05, -34.56) * mm});
            skLineSegment(sketch, "E208.15.20.0", {"start": v(9.05, -36.56) * mm, "end": v(11.05, -36.56) * mm});
            skLineSegment(sketch, "E208.15.20.1", {"start": v(9.05, -36.56) * mm, "end": v(9.05, -38.56) * mm});
            skLineSegment(sketch, "E208.15.20.2", {"start": v(9.05, -38.56) * mm, "end": v(11.05, -38.56) * mm});
            skLineSegment(sketch, "E208.15.20.3", {"start": v(11.05, -36.56) * mm, "end": v(11.05, -38.56) * mm});
            skLineSegment(sketch, "E208.15.21.0", {"start": v(9.05, -40.56) * mm, "end": v(11.05, -40.56) * mm});
            skLineSegment(sketch, "E208.15.21.1", {"start": v(9.05, -40.56) * mm, "end": v(9.05, -42.56) * mm});
            skLineSegment(sketch, "E208.15.21.2", {"start": v(9.05, -42.56) * mm, "end": v(11.05, -42.56) * mm});
            skLineSegment(sketch, "E208.15.21.3", {"start": v(11.05, -40.56) * mm, "end": v(11.05, -42.56) * mm});
            skLineSegment(sketch, "E208.16.0.0", {"start": v(13.05, 43.44) * mm, "end": v(15.05, 43.44) * mm});
            skLineSegment(sketch, "E208.16.0.1", {"start": v(13.05, 43.44) * mm, "end": v(13.05, 41.44) * mm});
            skLineSegment(sketch, "E208.16.0.2", {"start": v(13.05, 41.44) * mm, "end": v(15.05, 41.44) * mm});
            skLineSegment(sketch, "E208.16.0.3", {"start": v(15.05, 43.44) * mm, "end": v(15.05, 41.44) * mm});
            skLineSegment(sketch, "E208.16.1.0", {"start": v(13.05, 39.44) * mm, "end": v(15.05, 39.44) * mm});
            skLineSegment(sketch, "E208.16.1.1", {"start": v(13.05, 39.44) * mm, "end": v(13.05, 37.44) * mm});
            skLineSegment(sketch, "E208.16.1.2", {"start": v(13.05, 37.44) * mm, "end": v(15.05, 37.44) * mm});
            skLineSegment(sketch, "E208.16.1.3", {"start": v(15.05, 39.44) * mm, "end": v(15.05, 37.44) * mm});
            skLineSegment(sketch, "E208.16.2.0", {"start": v(13.05, 35.44) * mm, "end": v(15.05, 35.44) * mm});
            skLineSegment(sketch, "E208.16.2.1", {"start": v(13.05, 35.44) * mm, "end": v(13.05, 33.44) * mm});
            skLineSegment(sketch, "E208.16.2.2", {"start": v(13.05, 33.44) * mm, "end": v(15.05, 33.44) * mm});
            skLineSegment(sketch, "E208.16.2.3", {"start": v(15.05, 35.44) * mm, "end": v(15.05, 33.44) * mm});
            skLineSegment(sketch, "E208.16.3.0", {"start": v(13.05, 31.44) * mm, "end": v(15.05, 31.44) * mm});
            skLineSegment(sketch, "E208.16.3.1", {"start": v(13.05, 31.44) * mm, "end": v(13.05, 29.44) * mm});
            skLineSegment(sketch, "E208.16.3.2", {"start": v(13.05, 29.44) * mm, "end": v(15.05, 29.44) * mm});
            skLineSegment(sketch, "E208.16.3.3", {"start": v(15.05, 31.44) * mm, "end": v(15.05, 29.44) * mm});
            skLineSegment(sketch, "E208.16.4.0", {"start": v(13.05, 27.44) * mm, "end": v(15.05, 27.44) * mm});
            skLineSegment(sketch, "E208.16.4.1", {"start": v(13.05, 27.44) * mm, "end": v(13.05, 25.44) * mm});
            skLineSegment(sketch, "E208.16.4.2", {"start": v(13.05, 25.44) * mm, "end": v(15.05, 25.44) * mm});
            skLineSegment(sketch, "E208.16.4.3", {"start": v(15.05, 27.44) * mm, "end": v(15.05, 25.44) * mm});
            skLineSegment(sketch, "E208.16.5.0", {"start": v(13.05, 23.44) * mm, "end": v(15.05, 23.44) * mm});
            skLineSegment(sketch, "E208.16.5.1", {"start": v(13.05, 23.44) * mm, "end": v(13.05, 21.44) * mm});
            skLineSegment(sketch, "E208.16.5.2", {"start": v(13.05, 21.44) * mm, "end": v(15.05, 21.44) * mm});
            skLineSegment(sketch, "E208.16.5.3", {"start": v(15.05, 23.44) * mm, "end": v(15.05, 21.44) * mm});
            skLineSegment(sketch, "E208.16.6.0", {"start": v(13.05, 19.44) * mm, "end": v(15.05, 19.44) * mm});
            skLineSegment(sketch, "E208.16.6.1", {"start": v(13.05, 19.44) * mm, "end": v(13.05, 17.44) * mm});
            skLineSegment(sketch, "E208.16.6.2", {"start": v(13.05, 17.44) * mm, "end": v(15.05, 17.44) * mm});
            skLineSegment(sketch, "E208.16.6.3", {"start": v(15.05, 19.44) * mm, "end": v(15.05, 17.44) * mm});
            skLineSegment(sketch, "E208.16.7.0", {"start": v(13.05, 15.44) * mm, "end": v(15.05, 15.44) * mm});
            skLineSegment(sketch, "E208.16.7.1", {"start": v(13.05, 15.44) * mm, "end": v(13.05, 13.44) * mm});
            skLineSegment(sketch, "E208.16.7.2", {"start": v(13.05, 13.44) * mm, "end": v(15.05, 13.44) * mm});
            skLineSegment(sketch, "E208.16.7.3", {"start": v(15.05, 15.44) * mm, "end": v(15.05, 13.44) * mm});
            skLineSegment(sketch, "E208.16.8.0", {"start": v(13.05, 11.44) * mm, "end": v(15.05, 11.44) * mm});
            skLineSegment(sketch, "E208.16.8.1", {"start": v(13.05, 11.44) * mm, "end": v(13.05, 9.44) * mm});
            skLineSegment(sketch, "E208.16.8.2", {"start": v(13.05, 9.44) * mm, "end": v(15.05, 9.44) * mm});
            skLineSegment(sketch, "E208.16.8.3", {"start": v(15.05, 11.44) * mm, "end": v(15.05, 9.44) * mm});
            skLineSegment(sketch, "E208.16.9.0", {"start": v(13.05, 7.44) * mm, "end": v(15.05, 7.44) * mm});
            skLineSegment(sketch, "E208.16.9.1", {"start": v(13.05, 7.44) * mm, "end": v(13.05, 5.44) * mm});
            skLineSegment(sketch, "E208.16.9.2", {"start": v(13.05, 5.44) * mm, "end": v(15.05, 5.44) * mm});
            skLineSegment(sketch, "E208.16.9.3", {"start": v(15.05, 7.44) * mm, "end": v(15.05, 5.44) * mm});
            skLineSegment(sketch, "E208.16.10.0", {"start": v(13.05, 3.44) * mm, "end": v(15.05, 3.44) * mm});
            skLineSegment(sketch, "E208.16.10.1", {"start": v(13.05, 3.44) * mm, "end": v(13.05, 1.44) * mm});
            skLineSegment(sketch, "E208.16.10.2", {"start": v(13.05, 1.44) * mm, "end": v(15.05, 1.44) * mm});
            skLineSegment(sketch, "E208.16.10.3", {"start": v(15.05, 3.44) * mm, "end": v(15.05, 1.44) * mm});
            skLineSegment(sketch, "E208.16.11.0", {"start": v(13.05, -0.56) * mm, "end": v(15.05, -0.56) * mm});
            skLineSegment(sketch, "E208.16.11.1", {"start": v(13.05, -0.56) * mm, "end": v(13.05, -2.56) * mm});
            skLineSegment(sketch, "E208.16.11.2", {"start": v(13.05, -2.56) * mm, "end": v(15.05, -2.56) * mm});
            skLineSegment(sketch, "E208.16.11.3", {"start": v(15.05, -0.56) * mm, "end": v(15.05, -2.56) * mm});
            skLineSegment(sketch, "E208.16.12.0", {"start": v(13.05, -4.56) * mm, "end": v(15.05, -4.56) * mm});
            skLineSegment(sketch, "E208.16.12.1", {"start": v(13.05, -4.56) * mm, "end": v(13.05, -6.56) * mm});
            skLineSegment(sketch, "E208.16.12.2", {"start": v(13.05, -6.56) * mm, "end": v(15.05, -6.56) * mm});
            skLineSegment(sketch, "E208.16.12.3", {"start": v(15.05, -4.56) * mm, "end": v(15.05, -6.56) * mm});
            skLineSegment(sketch, "E208.16.13.0", {"start": v(13.05, -8.56) * mm, "end": v(15.05, -8.56) * mm});
            skLineSegment(sketch, "E208.16.13.1", {"start": v(13.05, -8.56) * mm, "end": v(13.05, -10.56) * mm});
            skLineSegment(sketch, "E208.16.13.2", {"start": v(13.05, -10.56) * mm, "end": v(15.05, -10.56) * mm});
            skLineSegment(sketch, "E208.16.13.3", {"start": v(15.05, -8.56) * mm, "end": v(15.05, -10.56) * mm});
            skLineSegment(sketch, "E208.16.14.0", {"start": v(13.05, -12.56) * mm, "end": v(15.05, -12.56) * mm});
            skLineSegment(sketch, "E208.16.14.1", {"start": v(13.05, -12.56) * mm, "end": v(13.05, -14.56) * mm});
            skLineSegment(sketch, "E208.16.14.2", {"start": v(13.05, -14.56) * mm, "end": v(15.05, -14.56) * mm});
            skLineSegment(sketch, "E208.16.14.3", {"start": v(15.05, -12.56) * mm, "end": v(15.05, -14.56) * mm});
            skLineSegment(sketch, "E208.16.15.0", {"start": v(13.05, -16.56) * mm, "end": v(15.05, -16.56) * mm});
            skLineSegment(sketch, "E208.16.15.1", {"start": v(13.05, -16.56) * mm, "end": v(13.05, -18.56) * mm});
            skLineSegment(sketch, "E208.16.15.2", {"start": v(13.05, -18.56) * mm, "end": v(15.05, -18.56) * mm});
            skLineSegment(sketch, "E208.16.15.3", {"start": v(15.05, -16.56) * mm, "end": v(15.05, -18.56) * mm});
            skLineSegment(sketch, "E208.16.16.0", {"start": v(13.05, -20.56) * mm, "end": v(15.05, -20.56) * mm});
            skLineSegment(sketch, "E208.16.16.1", {"start": v(13.05, -20.56) * mm, "end": v(13.05, -22.56) * mm});
            skLineSegment(sketch, "E208.16.16.2", {"start": v(13.05, -22.56) * mm, "end": v(15.05, -22.56) * mm});
            skLineSegment(sketch, "E208.16.16.3", {"start": v(15.05, -20.56) * mm, "end": v(15.05, -22.56) * mm});
            skLineSegment(sketch, "E208.16.17.0", {"start": v(13.05, -24.56) * mm, "end": v(15.05, -24.56) * mm});
            skLineSegment(sketch, "E208.16.17.1", {"start": v(13.05, -24.56) * mm, "end": v(13.05, -26.56) * mm});
            skLineSegment(sketch, "E208.16.17.2", {"start": v(13.05, -26.56) * mm, "end": v(15.05, -26.56) * mm});
            skLineSegment(sketch, "E208.16.17.3", {"start": v(15.05, -24.56) * mm, "end": v(15.05, -26.56) * mm});
            skLineSegment(sketch, "E208.16.18.0", {"start": v(13.05, -28.56) * mm, "end": v(15.05, -28.56) * mm});
            skLineSegment(sketch, "E208.16.18.1", {"start": v(13.05, -28.56) * mm, "end": v(13.05, -30.56) * mm});
            skLineSegment(sketch, "E208.16.18.2", {"start": v(13.05, -30.56) * mm, "end": v(15.05, -30.56) * mm});
            skLineSegment(sketch, "E208.16.18.3", {"start": v(15.05, -28.56) * mm, "end": v(15.05, -30.56) * mm});
            skLineSegment(sketch, "E208.16.19.0", {"start": v(13.05, -32.56) * mm, "end": v(15.05, -32.56) * mm});
            skLineSegment(sketch, "E208.16.19.1", {"start": v(13.05, -32.56) * mm, "end": v(13.05, -34.56) * mm});
            skLineSegment(sketch, "E208.16.19.2", {"start": v(13.05, -34.56) * mm, "end": v(15.05, -34.56) * mm});
            skLineSegment(sketch, "E208.16.19.3", {"start": v(15.05, -32.56) * mm, "end": v(15.05, -34.56) * mm});
            skLineSegment(sketch, "E208.16.20.0", {"start": v(13.05, -36.56) * mm, "end": v(15.05, -36.56) * mm});
            skLineSegment(sketch, "E208.16.20.1", {"start": v(13.05, -36.56) * mm, "end": v(13.05, -38.56) * mm});
            skLineSegment(sketch, "E208.16.20.2", {"start": v(13.05, -38.56) * mm, "end": v(15.05, -38.56) * mm});
            skLineSegment(sketch, "E208.16.20.3", {"start": v(15.05, -36.56) * mm, "end": v(15.05, -38.56) * mm});
            skLineSegment(sketch, "E208.16.21.0", {"start": v(13.05, -40.56) * mm, "end": v(15.05, -40.56) * mm});
            skLineSegment(sketch, "E208.16.21.1", {"start": v(13.05, -40.56) * mm, "end": v(13.05, -42.56) * mm});
            skLineSegment(sketch, "E208.16.21.2", {"start": v(13.05, -42.56) * mm, "end": v(15.05, -42.56) * mm});
            skLineSegment(sketch, "E208.16.21.3", {"start": v(15.05, -40.56) * mm, "end": v(15.05, -42.56) * mm});
            skLineSegment(sketch, "E208.17.0.0", {"start": v(17.05, 43.44) * mm, "end": v(19.05, 43.44) * mm});
            skLineSegment(sketch, "E208.17.0.1", {"start": v(17.05, 43.44) * mm, "end": v(17.05, 41.44) * mm});
            skLineSegment(sketch, "E208.17.0.2", {"start": v(17.05, 41.44) * mm, "end": v(19.05, 41.44) * mm});
            skLineSegment(sketch, "E208.17.0.3", {"start": v(19.05, 43.44) * mm, "end": v(19.05, 41.44) * mm});
            skLineSegment(sketch, "E208.17.1.0", {"start": v(17.05, 39.44) * mm, "end": v(19.05, 39.44) * mm});
            skLineSegment(sketch, "E208.17.1.1", {"start": v(17.05, 39.44) * mm, "end": v(17.05, 37.44) * mm});
            skLineSegment(sketch, "E208.17.1.2", {"start": v(17.05, 37.44) * mm, "end": v(19.05, 37.44) * mm});
            skLineSegment(sketch, "E208.17.1.3", {"start": v(19.05, 39.44) * mm, "end": v(19.05, 37.44) * mm});
            skLineSegment(sketch, "E208.17.2.0", {"start": v(17.05, 35.44) * mm, "end": v(19.05, 35.44) * mm});
            skLineSegment(sketch, "E208.17.2.1", {"start": v(17.05, 35.44) * mm, "end": v(17.05, 33.44) * mm});
            skLineSegment(sketch, "E208.17.2.2", {"start": v(17.05, 33.44) * mm, "end": v(19.05, 33.44) * mm});
            skLineSegment(sketch, "E208.17.2.3", {"start": v(19.05, 35.44) * mm, "end": v(19.05, 33.44) * mm});
            skLineSegment(sketch, "E208.17.3.0", {"start": v(17.05, 31.44) * mm, "end": v(19.05, 31.44) * mm});
            skLineSegment(sketch, "E208.17.3.1", {"start": v(17.05, 31.44) * mm, "end": v(17.05, 29.44) * mm});
            skLineSegment(sketch, "E208.17.3.2", {"start": v(17.05, 29.44) * mm, "end": v(19.05, 29.44) * mm});
            skLineSegment(sketch, "E208.17.3.3", {"start": v(19.05, 31.44) * mm, "end": v(19.05, 29.44) * mm});
            skLineSegment(sketch, "E208.17.4.0", {"start": v(17.05, 27.44) * mm, "end": v(19.05, 27.44) * mm});
            skLineSegment(sketch, "E208.17.4.1", {"start": v(17.05, 27.44) * mm, "end": v(17.05, 25.44) * mm});
            skLineSegment(sketch, "E208.17.4.2", {"start": v(17.05, 25.44) * mm, "end": v(19.05, 25.44) * mm});
            skLineSegment(sketch, "E208.17.4.3", {"start": v(19.05, 27.44) * mm, "end": v(19.05, 25.44) * mm});
            skLineSegment(sketch, "E208.17.5.0", {"start": v(17.05, 23.44) * mm, "end": v(19.05, 23.44) * mm});
            skLineSegment(sketch, "E208.17.5.1", {"start": v(17.05, 23.44) * mm, "end": v(17.05, 21.44) * mm});
            skLineSegment(sketch, "E208.17.5.2", {"start": v(17.05, 21.44) * mm, "end": v(19.05, 21.44) * mm});
            skLineSegment(sketch, "E208.17.5.3", {"start": v(19.05, 23.44) * mm, "end": v(19.05, 21.44) * mm});
            skLineSegment(sketch, "E208.17.6.0", {"start": v(17.05, 19.44) * mm, "end": v(19.05, 19.44) * mm});
            skLineSegment(sketch, "E208.17.6.1", {"start": v(17.05, 19.44) * mm, "end": v(17.05, 17.44) * mm});
            skLineSegment(sketch, "E208.17.6.2", {"start": v(17.05, 17.44) * mm, "end": v(19.05, 17.44) * mm});
            skLineSegment(sketch, "E208.17.6.3", {"start": v(19.05, 19.44) * mm, "end": v(19.05, 17.44) * mm});
            skLineSegment(sketch, "E208.17.7.0", {"start": v(17.05, 15.44) * mm, "end": v(19.05, 15.44) * mm});
            skLineSegment(sketch, "E208.17.7.1", {"start": v(17.05, 15.44) * mm, "end": v(17.05, 13.44) * mm});
            skLineSegment(sketch, "E208.17.7.2", {"start": v(17.05, 13.44) * mm, "end": v(19.05, 13.44) * mm});
            skLineSegment(sketch, "E208.17.7.3", {"start": v(19.05, 15.44) * mm, "end": v(19.05, 13.44) * mm});
            skLineSegment(sketch, "E208.17.8.0", {"start": v(17.05, 11.44) * mm, "end": v(19.05, 11.44) * mm});
            skLineSegment(sketch, "E208.17.8.1", {"start": v(17.05, 11.44) * mm, "end": v(17.05, 9.44) * mm});
            skLineSegment(sketch, "E208.17.8.2", {"start": v(17.05, 9.44) * mm, "end": v(19.05, 9.44) * mm});
            skLineSegment(sketch, "E208.17.8.3", {"start": v(19.05, 11.44) * mm, "end": v(19.05, 9.44) * mm});
            skLineSegment(sketch, "E208.17.9.0", {"start": v(17.05, 7.44) * mm, "end": v(19.05, 7.44) * mm});
            skLineSegment(sketch, "E208.17.9.1", {"start": v(17.05, 7.44) * mm, "end": v(17.05, 5.44) * mm});
            skLineSegment(sketch, "E208.17.9.2", {"start": v(17.05, 5.44) * mm, "end": v(19.05, 5.44) * mm});
            skLineSegment(sketch, "E208.17.9.3", {"start": v(19.05, 7.44) * mm, "end": v(19.05, 5.44) * mm});
            skLineSegment(sketch, "E208.17.10.0", {"start": v(17.05, 3.44) * mm, "end": v(19.05, 3.44) * mm});
            skLineSegment(sketch, "E208.17.10.1", {"start": v(17.05, 3.44) * mm, "end": v(17.05, 1.44) * mm});
            skLineSegment(sketch, "E208.17.10.2", {"start": v(17.05, 1.44) * mm, "end": v(19.05, 1.44) * mm});
            skLineSegment(sketch, "E208.17.10.3", {"start": v(19.05, 3.44) * mm, "end": v(19.05, 1.44) * mm});
            skLineSegment(sketch, "E208.17.11.0", {"start": v(17.05, -0.56) * mm, "end": v(19.05, -0.56) * mm});
            skLineSegment(sketch, "E208.17.11.1", {"start": v(17.05, -0.56) * mm, "end": v(17.05, -2.56) * mm});
            skLineSegment(sketch, "E208.17.11.2", {"start": v(17.05, -2.56) * mm, "end": v(19.05, -2.56) * mm});
            skLineSegment(sketch, "E208.17.11.3", {"start": v(19.05, -0.56) * mm, "end": v(19.05, -2.56) * mm});
            skLineSegment(sketch, "E208.17.12.0", {"start": v(17.05, -4.56) * mm, "end": v(19.05, -4.56) * mm});
            skLineSegment(sketch, "E208.17.12.1", {"start": v(17.05, -4.56) * mm, "end": v(17.05, -6.56) * mm});
            skLineSegment(sketch, "E208.17.12.2", {"start": v(17.05, -6.56) * mm, "end": v(19.05, -6.56) * mm});
            skLineSegment(sketch, "E208.17.12.3", {"start": v(19.05, -4.56) * mm, "end": v(19.05, -6.56) * mm});
            skLineSegment(sketch, "E208.17.13.0", {"start": v(17.05, -8.56) * mm, "end": v(19.05, -8.56) * mm});
            skLineSegment(sketch, "E208.17.13.1", {"start": v(17.05, -8.56) * mm, "end": v(17.05, -10.56) * mm});
            skLineSegment(sketch, "E208.17.13.2", {"start": v(17.05, -10.56) * mm, "end": v(19.05, -10.56) * mm});
            skLineSegment(sketch, "E208.17.13.3", {"start": v(19.05, -8.56) * mm, "end": v(19.05, -10.56) * mm});
            skLineSegment(sketch, "E208.17.14.0", {"start": v(17.05, -12.56) * mm, "end": v(19.05, -12.56) * mm});
            skLineSegment(sketch, "E208.17.14.1", {"start": v(17.05, -12.56) * mm, "end": v(17.05, -14.56) * mm});
            skLineSegment(sketch, "E208.17.14.2", {"start": v(17.05, -14.56) * mm, "end": v(19.05, -14.56) * mm});
            skLineSegment(sketch, "E208.17.14.3", {"start": v(19.05, -12.56) * mm, "end": v(19.05, -14.56) * mm});
            skLineSegment(sketch, "E208.17.15.0", {"start": v(17.05, -16.56) * mm, "end": v(19.05, -16.56) * mm});
            skLineSegment(sketch, "E208.17.15.1", {"start": v(17.05, -16.56) * mm, "end": v(17.05, -18.56) * mm});
            skLineSegment(sketch, "E208.17.15.2", {"start": v(17.05, -18.56) * mm, "end": v(19.05, -18.56) * mm});
            skLineSegment(sketch, "E208.17.15.3", {"start": v(19.05, -16.56) * mm, "end": v(19.05, -18.56) * mm});
            skLineSegment(sketch, "E208.17.16.0", {"start": v(17.05, -20.56) * mm, "end": v(19.05, -20.56) * mm});
            skLineSegment(sketch, "E208.17.16.1", {"start": v(17.05, -20.56) * mm, "end": v(17.05, -22.56) * mm});
            skLineSegment(sketch, "E208.17.16.2", {"start": v(17.05, -22.56) * mm, "end": v(19.05, -22.56) * mm});
            skLineSegment(sketch, "E208.17.16.3", {"start": v(19.05, -20.56) * mm, "end": v(19.05, -22.56) * mm});
            skLineSegment(sketch, "E208.17.17.0", {"start": v(17.05, -24.56) * mm, "end": v(19.05, -24.56) * mm});
            skLineSegment(sketch, "E208.17.17.1", {"start": v(17.05, -24.56) * mm, "end": v(17.05, -26.56) * mm});
            skLineSegment(sketch, "E208.17.17.2", {"start": v(17.05, -26.56) * mm, "end": v(19.05, -26.56) * mm});
            skLineSegment(sketch, "E208.17.17.3", {"start": v(19.05, -24.56) * mm, "end": v(19.05, -26.56) * mm});
            skLineSegment(sketch, "E208.17.18.0", {"start": v(17.05, -28.56) * mm, "end": v(19.05, -28.56) * mm});
            skLineSegment(sketch, "E208.17.18.1", {"start": v(17.05, -28.56) * mm, "end": v(17.05, -30.56) * mm});
            skLineSegment(sketch, "E208.17.18.2", {"start": v(17.05, -30.56) * mm, "end": v(19.05, -30.56) * mm});
            skLineSegment(sketch, "E208.17.18.3", {"start": v(19.05, -28.56) * mm, "end": v(19.05, -30.56) * mm});
            skLineSegment(sketch, "E208.17.19.0", {"start": v(17.05, -32.56) * mm, "end": v(19.05, -32.56) * mm});
            skLineSegment(sketch, "E208.17.19.1", {"start": v(17.05, -32.56) * mm, "end": v(17.05, -34.56) * mm});
            skLineSegment(sketch, "E208.17.19.2", {"start": v(17.05, -34.56) * mm, "end": v(19.05, -34.56) * mm});
            skLineSegment(sketch, "E208.17.19.3", {"start": v(19.05, -32.56) * mm, "end": v(19.05, -34.56) * mm});
            skLineSegment(sketch, "E208.17.20.0", {"start": v(17.05, -36.56) * mm, "end": v(19.05, -36.56) * mm});
            skLineSegment(sketch, "E208.17.20.1", {"start": v(17.05, -36.56) * mm, "end": v(17.05, -38.56) * mm});
            skLineSegment(sketch, "E208.17.20.2", {"start": v(17.05, -38.56) * mm, "end": v(19.05, -38.56) * mm});
            skLineSegment(sketch, "E208.17.20.3", {"start": v(19.05, -36.56) * mm, "end": v(19.05, -38.56) * mm});
            skLineSegment(sketch, "E208.17.21.0", {"start": v(17.05, -40.56) * mm, "end": v(19.05, -40.56) * mm});
            skLineSegment(sketch, "E208.17.21.1", {"start": v(17.05, -40.56) * mm, "end": v(17.05, -42.56) * mm});
            skLineSegment(sketch, "E208.17.21.2", {"start": v(17.05, -42.56) * mm, "end": v(19.05, -42.56) * mm});
            skLineSegment(sketch, "E208.17.21.3", {"start": v(19.05, -40.56) * mm, "end": v(19.05, -42.56) * mm});
            skLineSegment(sketch, "E208.18.0.0", {"start": v(21.05, 43.44) * mm, "end": v(23.05, 43.44) * mm});
            skLineSegment(sketch, "E208.18.0.1", {"start": v(21.05, 43.44) * mm, "end": v(21.05, 41.44) * mm});
            skLineSegment(sketch, "E208.18.0.2", {"start": v(21.05, 41.44) * mm, "end": v(23.05, 41.44) * mm});
            skLineSegment(sketch, "E208.18.0.3", {"start": v(23.05, 43.44) * mm, "end": v(23.05, 41.44) * mm});
            skLineSegment(sketch, "E208.18.1.0", {"start": v(21.05, 39.44) * mm, "end": v(23.05, 39.44) * mm});
            skLineSegment(sketch, "E208.18.1.1", {"start": v(21.05, 39.44) * mm, "end": v(21.05, 37.44) * mm});
            skLineSegment(sketch, "E208.18.1.2", {"start": v(21.05, 37.44) * mm, "end": v(23.05, 37.44) * mm});
            skLineSegment(sketch, "E208.18.1.3", {"start": v(23.05, 39.44) * mm, "end": v(23.05, 37.44) * mm});
            skLineSegment(sketch, "E208.18.2.0", {"start": v(21.05, 35.44) * mm, "end": v(23.05, 35.44) * mm});
            skLineSegment(sketch, "E208.18.2.1", {"start": v(21.05, 35.44) * mm, "end": v(21.05, 33.44) * mm});
            skLineSegment(sketch, "E208.18.2.2", {"start": v(21.05, 33.44) * mm, "end": v(23.05, 33.44) * mm});
            skLineSegment(sketch, "E208.18.2.3", {"start": v(23.05, 35.44) * mm, "end": v(23.05, 33.44) * mm});
            skLineSegment(sketch, "E208.18.3.0", {"start": v(21.05, 31.44) * mm, "end": v(23.05, 31.44) * mm});
            skLineSegment(sketch, "E208.18.3.1", {"start": v(21.05, 31.44) * mm, "end": v(21.05, 29.44) * mm});
            skLineSegment(sketch, "E208.18.3.2", {"start": v(21.05, 29.44) * mm, "end": v(23.05, 29.44) * mm});
            skLineSegment(sketch, "E208.18.3.3", {"start": v(23.05, 31.44) * mm, "end": v(23.05, 29.44) * mm});
            skLineSegment(sketch, "E208.18.4.0", {"start": v(21.05, 27.44) * mm, "end": v(23.05, 27.44) * mm});
            skLineSegment(sketch, "E208.18.4.1", {"start": v(21.05, 27.44) * mm, "end": v(21.05, 25.44) * mm});
            skLineSegment(sketch, "E208.18.4.2", {"start": v(21.05, 25.44) * mm, "end": v(23.05, 25.44) * mm});
            skLineSegment(sketch, "E208.18.4.3", {"start": v(23.05, 27.44) * mm, "end": v(23.05, 25.44) * mm});
            skLineSegment(sketch, "E208.18.5.0", {"start": v(21.05, 23.44) * mm, "end": v(23.05, 23.44) * mm});
            skLineSegment(sketch, "E208.18.5.1", {"start": v(21.05, 23.44) * mm, "end": v(21.05, 21.44) * mm});
            skLineSegment(sketch, "E208.18.5.2", {"start": v(21.05, 21.44) * mm, "end": v(23.05, 21.44) * mm});
            skLineSegment(sketch, "E208.18.5.3", {"start": v(23.05, 23.44) * mm, "end": v(23.05, 21.44) * mm});
            skLineSegment(sketch, "E208.18.6.0", {"start": v(21.05, 19.44) * mm, "end": v(23.05, 19.44) * mm});
            skLineSegment(sketch, "E208.18.6.1", {"start": v(21.05, 19.44) * mm, "end": v(21.05, 17.44) * mm});
            skLineSegment(sketch, "E208.18.6.2", {"start": v(21.05, 17.44) * mm, "end": v(23.05, 17.44) * mm});
            skLineSegment(sketch, "E208.18.6.3", {"start": v(23.05, 19.44) * mm, "end": v(23.05, 17.44) * mm});
            skLineSegment(sketch, "E208.18.7.0", {"start": v(21.05, 15.44) * mm, "end": v(23.05, 15.44) * mm});
            skLineSegment(sketch, "E208.18.7.1", {"start": v(21.05, 15.44) * mm, "end": v(21.05, 13.44) * mm});
            skLineSegment(sketch, "E208.18.7.2", {"start": v(21.05, 13.44) * mm, "end": v(23.05, 13.44) * mm});
            skLineSegment(sketch, "E208.18.7.3", {"start": v(23.05, 15.44) * mm, "end": v(23.05, 13.44) * mm});
            skLineSegment(sketch, "E208.18.8.0", {"start": v(21.05, 11.44) * mm, "end": v(23.05, 11.44) * mm});
            skLineSegment(sketch, "E208.18.8.1", {"start": v(21.05, 11.44) * mm, "end": v(21.05, 9.44) * mm});
            skLineSegment(sketch, "E208.18.8.2", {"start": v(21.05, 9.44) * mm, "end": v(23.05, 9.44) * mm});
            skLineSegment(sketch, "E208.18.8.3", {"start": v(23.05, 11.44) * mm, "end": v(23.05, 9.44) * mm});
            skLineSegment(sketch, "E208.18.9.0", {"start": v(21.05, 7.44) * mm, "end": v(23.05, 7.44) * mm});
            skLineSegment(sketch, "E208.18.9.1", {"start": v(21.05, 7.44) * mm, "end": v(21.05, 5.44) * mm});
            skLineSegment(sketch, "E208.18.9.2", {"start": v(21.05, 5.44) * mm, "end": v(23.05, 5.44) * mm});
            skLineSegment(sketch, "E208.18.9.3", {"start": v(23.05, 7.44) * mm, "end": v(23.05, 5.44) * mm});
            skLineSegment(sketch, "E208.18.10.0", {"start": v(21.05, 3.44) * mm, "end": v(23.05, 3.44) * mm});
            skLineSegment(sketch, "E208.18.10.1", {"start": v(21.05, 3.44) * mm, "end": v(21.05, 1.44) * mm});
            skLineSegment(sketch, "E208.18.10.2", {"start": v(21.05, 1.44) * mm, "end": v(23.05, 1.44) * mm});
            skLineSegment(sketch, "E208.18.10.3", {"start": v(23.05, 3.44) * mm, "end": v(23.05, 1.44) * mm});
            skLineSegment(sketch, "E208.18.11.0", {"start": v(21.05, -0.56) * mm, "end": v(23.05, -0.56) * mm});
            skLineSegment(sketch, "E208.18.11.1", {"start": v(21.05, -0.56) * mm, "end": v(21.05, -2.56) * mm});
            skLineSegment(sketch, "E208.18.11.2", {"start": v(21.05, -2.56) * mm, "end": v(23.05, -2.56) * mm});
            skLineSegment(sketch, "E208.18.11.3", {"start": v(23.05, -0.56) * mm, "end": v(23.05, -2.56) * mm});
            skLineSegment(sketch, "E208.18.12.0", {"start": v(21.05, -4.56) * mm, "end": v(23.05, -4.56) * mm});
            skLineSegment(sketch, "E208.18.12.1", {"start": v(21.05, -4.56) * mm, "end": v(21.05, -6.56) * mm});
            skLineSegment(sketch, "E208.18.12.2", {"start": v(21.05, -6.56) * mm, "end": v(23.05, -6.56) * mm});
            skLineSegment(sketch, "E208.18.12.3", {"start": v(23.05, -4.56) * mm, "end": v(23.05, -6.56) * mm});
            skLineSegment(sketch, "E208.18.13.0", {"start": v(21.05, -8.56) * mm, "end": v(23.05, -8.56) * mm});
            skLineSegment(sketch, "E208.18.13.1", {"start": v(21.05, -8.56) * mm, "end": v(21.05, -10.56) * mm});
            skLineSegment(sketch, "E208.18.13.2", {"start": v(21.05, -10.56) * mm, "end": v(23.05, -10.56) * mm});
            skLineSegment(sketch, "E208.18.13.3", {"start": v(23.05, -8.56) * mm, "end": v(23.05, -10.56) * mm});
            skLineSegment(sketch, "E208.18.14.0", {"start": v(21.05, -12.56) * mm, "end": v(23.05, -12.56) * mm});
            skLineSegment(sketch, "E208.18.14.1", {"start": v(21.05, -12.56) * mm, "end": v(21.05, -14.56) * mm});
            skLineSegment(sketch, "E208.18.14.2", {"start": v(21.05, -14.56) * mm, "end": v(23.05, -14.56) * mm});
            skLineSegment(sketch, "E208.18.14.3", {"start": v(23.05, -12.56) * mm, "end": v(23.05, -14.56) * mm});
            skLineSegment(sketch, "E208.18.15.0", {"start": v(21.05, -16.56) * mm, "end": v(23.05, -16.56) * mm});
            skLineSegment(sketch, "E208.18.15.1", {"start": v(21.05, -16.56) * mm, "end": v(21.05, -18.56) * mm});
            skLineSegment(sketch, "E208.18.15.2", {"start": v(21.05, -18.56) * mm, "end": v(23.05, -18.56) * mm});
            skLineSegment(sketch, "E208.18.15.3", {"start": v(23.05, -16.56) * mm, "end": v(23.05, -18.56) * mm});
            skLineSegment(sketch, "E208.18.16.0", {"start": v(21.05, -20.56) * mm, "end": v(23.05, -20.56) * mm});
            skLineSegment(sketch, "E208.18.16.1", {"start": v(21.05, -20.56) * mm, "end": v(21.05, -22.56) * mm});
            skLineSegment(sketch, "E208.18.16.2", {"start": v(21.05, -22.56) * mm, "end": v(23.05, -22.56) * mm});
            skLineSegment(sketch, "E208.18.16.3", {"start": v(23.05, -20.56) * mm, "end": v(23.05, -22.56) * mm});
            skLineSegment(sketch, "E208.18.17.0", {"start": v(21.05, -24.56) * mm, "end": v(23.05, -24.56) * mm});
            skLineSegment(sketch, "E208.18.17.1", {"start": v(21.05, -24.56) * mm, "end": v(21.05, -26.56) * mm});
            skLineSegment(sketch, "E208.18.17.2", {"start": v(21.05, -26.56) * mm, "end": v(23.05, -26.56) * mm});
            skLineSegment(sketch, "E208.18.17.3", {"start": v(23.05, -24.56) * mm, "end": v(23.05, -26.56) * mm});
            skLineSegment(sketch, "E208.18.18.0", {"start": v(21.05, -28.56) * mm, "end": v(23.05, -28.56) * mm});
            skLineSegment(sketch, "E208.18.18.1", {"start": v(21.05, -28.56) * mm, "end": v(21.05, -30.56) * mm});
            skLineSegment(sketch, "E208.18.18.2", {"start": v(21.05, -30.56) * mm, "end": v(23.05, -30.56) * mm});
            skLineSegment(sketch, "E208.18.18.3", {"start": v(23.05, -28.56) * mm, "end": v(23.05, -30.56) * mm});
            skLineSegment(sketch, "E208.18.19.0", {"start": v(21.05, -32.56) * mm, "end": v(23.05, -32.56) * mm});
            skLineSegment(sketch, "E208.18.19.1", {"start": v(21.05, -32.56) * mm, "end": v(21.05, -34.56) * mm});
            skLineSegment(sketch, "E208.18.19.2", {"start": v(21.05, -34.56) * mm, "end": v(23.05, -34.56) * mm});
            skLineSegment(sketch, "E208.18.19.3", {"start": v(23.05, -32.56) * mm, "end": v(23.05, -34.56) * mm});
            skLineSegment(sketch, "E208.18.20.0", {"start": v(21.05, -36.56) * mm, "end": v(23.05, -36.56) * mm});
            skLineSegment(sketch, "E208.18.20.1", {"start": v(21.05, -36.56) * mm, "end": v(21.05, -38.56) * mm});
            skLineSegment(sketch, "E208.18.20.2", {"start": v(21.05, -38.56) * mm, "end": v(23.05, -38.56) * mm});
            skLineSegment(sketch, "E208.18.20.3", {"start": v(23.05, -36.56) * mm, "end": v(23.05, -38.56) * mm});
            skLineSegment(sketch, "E208.18.21.0", {"start": v(21.05, -40.56) * mm, "end": v(23.05, -40.56) * mm});
            skLineSegment(sketch, "E208.18.21.1", {"start": v(21.05, -40.56) * mm, "end": v(21.05, -42.56) * mm});
            skLineSegment(sketch, "E208.18.21.2", {"start": v(21.05, -42.56) * mm, "end": v(23.05, -42.56) * mm});
            skLineSegment(sketch, "E208.18.21.3", {"start": v(23.05, -40.56) * mm, "end": v(23.05, -42.56) * mm});
            skLineSegment(sketch, "E208.19.0.0", {"start": v(25.05, 43.44) * mm, "end": v(27.05, 43.44) * mm});
            skLineSegment(sketch, "E208.19.0.1", {"start": v(25.05, 43.44) * mm, "end": v(25.05, 41.44) * mm});
            skLineSegment(sketch, "E208.19.0.2", {"start": v(25.05, 41.44) * mm, "end": v(27.05, 41.44) * mm});
            skLineSegment(sketch, "E208.19.0.3", {"start": v(27.05, 43.44) * mm, "end": v(27.05, 41.44) * mm});
            skLineSegment(sketch, "E208.19.1.0", {"start": v(25.05, 39.44) * mm, "end": v(27.05, 39.44) * mm});
            skLineSegment(sketch, "E208.19.1.1", {"start": v(25.05, 39.44) * mm, "end": v(25.05, 37.44) * mm});
            skLineSegment(sketch, "E208.19.1.2", {"start": v(25.05, 37.44) * mm, "end": v(27.05, 37.44) * mm});
            skLineSegment(sketch, "E208.19.1.3", {"start": v(27.05, 39.44) * mm, "end": v(27.05, 37.44) * mm});
            skLineSegment(sketch, "E208.19.2.0", {"start": v(25.05, 35.44) * mm, "end": v(27.05, 35.44) * mm});
            skLineSegment(sketch, "E208.19.2.1", {"start": v(25.05, 35.44) * mm, "end": v(25.05, 33.44) * mm});
            skLineSegment(sketch, "E208.19.2.2", {"start": v(25.05, 33.44) * mm, "end": v(27.05, 33.44) * mm});
            skLineSegment(sketch, "E208.19.2.3", {"start": v(27.05, 35.44) * mm, "end": v(27.05, 33.44) * mm});
            skLineSegment(sketch, "E208.19.3.0", {"start": v(25.05, 31.44) * mm, "end": v(27.05, 31.44) * mm});
            skLineSegment(sketch, "E208.19.3.1", {"start": v(25.05, 31.44) * mm, "end": v(25.05, 29.44) * mm});
            skLineSegment(sketch, "E208.19.3.2", {"start": v(25.05, 29.44) * mm, "end": v(27.05, 29.44) * mm});
            skLineSegment(sketch, "E208.19.3.3", {"start": v(27.05, 31.44) * mm, "end": v(27.05, 29.44) * mm});
            skLineSegment(sketch, "E208.19.4.0", {"start": v(25.05, 27.44) * mm, "end": v(27.05, 27.44) * mm});
            skLineSegment(sketch, "E208.19.4.1", {"start": v(25.05, 27.44) * mm, "end": v(25.05, 25.44) * mm});
            skLineSegment(sketch, "E208.19.4.2", {"start": v(25.05, 25.44) * mm, "end": v(27.05, 25.44) * mm});
            skLineSegment(sketch, "E208.19.4.3", {"start": v(27.05, 27.44) * mm, "end": v(27.05, 25.44) * mm});
            skLineSegment(sketch, "E208.19.5.0", {"start": v(25.05, 23.44) * mm, "end": v(27.05, 23.44) * mm});
            skLineSegment(sketch, "E208.19.5.1", {"start": v(25.05, 23.44) * mm, "end": v(25.05, 21.44) * mm});
            skLineSegment(sketch, "E208.19.5.2", {"start": v(25.05, 21.44) * mm, "end": v(27.05, 21.44) * mm});
            skLineSegment(sketch, "E208.19.5.3", {"start": v(27.05, 23.44) * mm, "end": v(27.05, 21.44) * mm});
            skLineSegment(sketch, "E208.19.6.0", {"start": v(25.05, 19.44) * mm, "end": v(27.05, 19.44) * mm});
            skLineSegment(sketch, "E208.19.6.1", {"start": v(25.05, 19.44) * mm, "end": v(25.05, 17.44) * mm});
            skLineSegment(sketch, "E208.19.6.2", {"start": v(25.05, 17.44) * mm, "end": v(27.05, 17.44) * mm});
            skLineSegment(sketch, "E208.19.6.3", {"start": v(27.05, 19.44) * mm, "end": v(27.05, 17.44) * mm});
            skLineSegment(sketch, "E208.19.7.0", {"start": v(25.05, 15.44) * mm, "end": v(27.05, 15.44) * mm});
            skLineSegment(sketch, "E208.19.7.1", {"start": v(25.05, 15.44) * mm, "end": v(25.05, 13.44) * mm});
            skLineSegment(sketch, "E208.19.7.2", {"start": v(25.05, 13.44) * mm, "end": v(27.05, 13.44) * mm});
            skLineSegment(sketch, "E208.19.7.3", {"start": v(27.05, 15.44) * mm, "end": v(27.05, 13.44) * mm});
            skLineSegment(sketch, "E208.19.8.0", {"start": v(25.05, 11.44) * mm, "end": v(27.05, 11.44) * mm});
            skLineSegment(sketch, "E208.19.8.1", {"start": v(25.05, 11.44) * mm, "end": v(25.05, 9.44) * mm});
            skLineSegment(sketch, "E208.19.8.2", {"start": v(25.05, 9.44) * mm, "end": v(27.05, 9.44) * mm});
            skLineSegment(sketch, "E208.19.8.3", {"start": v(27.05, 11.44) * mm, "end": v(27.05, 9.44) * mm});
            skLineSegment(sketch, "E208.19.9.0", {"start": v(25.05, 7.44) * mm, "end": v(27.05, 7.44) * mm});
            skLineSegment(sketch, "E208.19.9.1", {"start": v(25.05, 7.44) * mm, "end": v(25.05, 5.44) * mm});
            skLineSegment(sketch, "E208.19.9.2", {"start": v(25.05, 5.44) * mm, "end": v(27.05, 5.44) * mm});
            skLineSegment(sketch, "E208.19.9.3", {"start": v(27.05, 7.44) * mm, "end": v(27.05, 5.44) * mm});
            skLineSegment(sketch, "E208.19.10.0", {"start": v(25.05, 3.44) * mm, "end": v(27.05, 3.44) * mm});
            skLineSegment(sketch, "E208.19.10.1", {"start": v(25.05, 3.44) * mm, "end": v(25.05, 1.44) * mm});
            skLineSegment(sketch, "E208.19.10.2", {"start": v(25.05, 1.44) * mm, "end": v(27.05, 1.44) * mm});
            skLineSegment(sketch, "E208.19.10.3", {"start": v(27.05, 3.44) * mm, "end": v(27.05, 1.44) * mm});
            skLineSegment(sketch, "E208.19.11.0", {"start": v(25.05, -0.56) * mm, "end": v(27.05, -0.56) * mm});
            skLineSegment(sketch, "E208.19.11.1", {"start": v(25.05, -0.56) * mm, "end": v(25.05, -2.56) * mm});
            skLineSegment(sketch, "E208.19.11.2", {"start": v(25.05, -2.56) * mm, "end": v(27.05, -2.56) * mm});
            skLineSegment(sketch, "E208.19.11.3", {"start": v(27.05, -0.56) * mm, "end": v(27.05, -2.56) * mm});
            skLineSegment(sketch, "E208.19.12.0", {"start": v(25.05, -4.56) * mm, "end": v(27.05, -4.56) * mm});
            skLineSegment(sketch, "E208.19.12.1", {"start": v(25.05, -4.56) * mm, "end": v(25.05, -6.56) * mm});
            skLineSegment(sketch, "E208.19.12.2", {"start": v(25.05, -6.56) * mm, "end": v(27.05, -6.56) * mm});
            skLineSegment(sketch, "E208.19.12.3", {"start": v(27.05, -4.56) * mm, "end": v(27.05, -6.56) * mm});
            skLineSegment(sketch, "E208.19.13.0", {"start": v(25.05, -8.56) * mm, "end": v(27.05, -8.56) * mm});
            skLineSegment(sketch, "E208.19.13.1", {"start": v(25.05, -8.56) * mm, "end": v(25.05, -10.56) * mm});
            skLineSegment(sketch, "E208.19.13.2", {"start": v(25.05, -10.56) * mm, "end": v(27.05, -10.56) * mm});
            skLineSegment(sketch, "E208.19.13.3", {"start": v(27.05, -8.56) * mm, "end": v(27.05, -10.56) * mm});
            skLineSegment(sketch, "E208.19.14.0", {"start": v(25.05, -12.56) * mm, "end": v(27.05, -12.56) * mm});
            skLineSegment(sketch, "E208.19.14.1", {"start": v(25.05, -12.56) * mm, "end": v(25.05, -14.56) * mm});
            skLineSegment(sketch, "E208.19.14.2", {"start": v(25.05, -14.56) * mm, "end": v(27.05, -14.56) * mm});
            skLineSegment(sketch, "E208.19.14.3", {"start": v(27.05, -12.56) * mm, "end": v(27.05, -14.56) * mm});
            skLineSegment(sketch, "E208.19.15.0", {"start": v(25.05, -16.56) * mm, "end": v(27.05, -16.56) * mm});
            skLineSegment(sketch, "E208.19.15.1", {"start": v(25.05, -16.56) * mm, "end": v(25.05, -18.56) * mm});
            skLineSegment(sketch, "E208.19.15.2", {"start": v(25.05, -18.56) * mm, "end": v(27.05, -18.56) * mm});
            skLineSegment(sketch, "E208.19.15.3", {"start": v(27.05, -16.56) * mm, "end": v(27.05, -18.56) * mm});
            skLineSegment(sketch, "E208.19.16.0", {"start": v(25.05, -20.56) * mm, "end": v(27.05, -20.56) * mm});
            skLineSegment(sketch, "E208.19.16.1", {"start": v(25.05, -20.56) * mm, "end": v(25.05, -22.56) * mm});
            skLineSegment(sketch, "E208.19.16.2", {"start": v(25.05, -22.56) * mm, "end": v(27.05, -22.56) * mm});
            skLineSegment(sketch, "E208.19.16.3", {"start": v(27.05, -20.56) * mm, "end": v(27.05, -22.56) * mm});
            skLineSegment(sketch, "E208.19.17.0", {"start": v(25.05, -24.56) * mm, "end": v(27.05, -24.56) * mm});
            skLineSegment(sketch, "E208.19.17.1", {"start": v(25.05, -24.56) * mm, "end": v(25.05, -26.56) * mm});
            skLineSegment(sketch, "E208.19.17.2", {"start": v(25.05, -26.56) * mm, "end": v(27.05, -26.56) * mm});
            skLineSegment(sketch, "E208.19.17.3", {"start": v(27.05, -24.56) * mm, "end": v(27.05, -26.56) * mm});
            skLineSegment(sketch, "E208.19.18.0", {"start": v(25.05, -28.56) * mm, "end": v(27.05, -28.56) * mm});
            skLineSegment(sketch, "E208.19.18.1", {"start": v(25.05, -28.56) * mm, "end": v(25.05, -30.56) * mm});
            skLineSegment(sketch, "E208.19.18.2", {"start": v(25.05, -30.56) * mm, "end": v(27.05, -30.56) * mm});
            skLineSegment(sketch, "E208.19.18.3", {"start": v(27.05, -28.56) * mm, "end": v(27.05, -30.56) * mm});
            skLineSegment(sketch, "E208.19.19.0", {"start": v(25.05, -32.56) * mm, "end": v(27.05, -32.56) * mm});
            skLineSegment(sketch, "E208.19.19.1", {"start": v(25.05, -32.56) * mm, "end": v(25.05, -34.56) * mm});
            skLineSegment(sketch, "E208.19.19.2", {"start": v(25.05, -34.56) * mm, "end": v(27.05, -34.56) * mm});
            skLineSegment(sketch, "E208.19.19.3", {"start": v(27.05, -32.56) * mm, "end": v(27.05, -34.56) * mm});
            skLineSegment(sketch, "E208.19.20.0", {"start": v(25.05, -36.56) * mm, "end": v(27.05, -36.56) * mm});
            skLineSegment(sketch, "E208.19.20.1", {"start": v(25.05, -36.56) * mm, "end": v(25.05, -38.56) * mm});
            skLineSegment(sketch, "E208.19.20.2", {"start": v(25.05, -38.56) * mm, "end": v(27.05, -38.56) * mm});
            skLineSegment(sketch, "E208.19.20.3", {"start": v(27.05, -36.56) * mm, "end": v(27.05, -38.56) * mm});
            skLineSegment(sketch, "E208.19.21.0", {"start": v(25.05, -40.56) * mm, "end": v(27.05, -40.56) * mm});
            skLineSegment(sketch, "E208.19.21.1", {"start": v(25.05, -40.56) * mm, "end": v(25.05, -42.56) * mm});
            skLineSegment(sketch, "E208.19.21.2", {"start": v(25.05, -42.56) * mm, "end": v(27.05, -42.56) * mm});
            skLineSegment(sketch, "E208.19.21.3", {"start": v(27.05, -40.56) * mm, "end": v(27.05, -42.56) * mm});
            skLineSegment(sketch, "E208.20.0.0", {"start": v(29.05, 43.44) * mm, "end": v(31.05, 43.44) * mm});
            skLineSegment(sketch, "E208.20.0.1", {"start": v(29.05, 43.44) * mm, "end": v(29.05, 41.44) * mm});
            skLineSegment(sketch, "E208.20.0.2", {"start": v(29.05, 41.44) * mm, "end": v(31.05, 41.44) * mm});
            skLineSegment(sketch, "E208.20.0.3", {"start": v(31.05, 43.44) * mm, "end": v(31.05, 41.44) * mm});
            skLineSegment(sketch, "E208.20.1.0", {"start": v(29.05, 39.44) * mm, "end": v(31.05, 39.44) * mm});
            skLineSegment(sketch, "E208.20.1.1", {"start": v(29.05, 39.44) * mm, "end": v(29.05, 37.44) * mm});
            skLineSegment(sketch, "E208.20.1.2", {"start": v(29.05, 37.44) * mm, "end": v(31.05, 37.44) * mm});
            skLineSegment(sketch, "E208.20.1.3", {"start": v(31.05, 39.44) * mm, "end": v(31.05, 37.44) * mm});
            skLineSegment(sketch, "E208.20.2.0", {"start": v(29.05, 35.44) * mm, "end": v(31.05, 35.44) * mm});
            skLineSegment(sketch, "E208.20.2.1", {"start": v(29.05, 35.44) * mm, "end": v(29.05, 33.44) * mm});
            skLineSegment(sketch, "E208.20.2.2", {"start": v(29.05, 33.44) * mm, "end": v(31.05, 33.44) * mm});
            skLineSegment(sketch, "E208.20.2.3", {"start": v(31.05, 35.44) * mm, "end": v(31.05, 33.44) * mm});
            skLineSegment(sketch, "E208.20.3.0", {"start": v(29.05, 31.44) * mm, "end": v(31.05, 31.44) * mm});
            skLineSegment(sketch, "E208.20.3.1", {"start": v(29.05, 31.44) * mm, "end": v(29.05, 29.44) * mm});
            skLineSegment(sketch, "E208.20.3.2", {"start": v(29.05, 29.44) * mm, "end": v(31.05, 29.44) * mm});
            skLineSegment(sketch, "E208.20.3.3", {"start": v(31.05, 31.44) * mm, "end": v(31.05, 29.44) * mm});
            skLineSegment(sketch, "E208.20.4.0", {"start": v(29.05, 27.44) * mm, "end": v(31.05, 27.44) * mm});
            skLineSegment(sketch, "E208.20.4.1", {"start": v(29.05, 27.44) * mm, "end": v(29.05, 25.44) * mm});
            skLineSegment(sketch, "E208.20.4.2", {"start": v(29.05, 25.44) * mm, "end": v(31.05, 25.44) * mm});
            skLineSegment(sketch, "E208.20.4.3", {"start": v(31.05, 27.44) * mm, "end": v(31.05, 25.44) * mm});
            skLineSegment(sketch, "E208.20.5.0", {"start": v(29.05, 23.44) * mm, "end": v(31.05, 23.44) * mm});
            skLineSegment(sketch, "E208.20.5.1", {"start": v(29.05, 23.44) * mm, "end": v(29.05, 21.44) * mm});
            skLineSegment(sketch, "E208.20.5.2", {"start": v(29.05, 21.44) * mm, "end": v(31.05, 21.44) * mm});
            skLineSegment(sketch, "E208.20.5.3", {"start": v(31.05, 23.44) * mm, "end": v(31.05, 21.44) * mm});
            skLineSegment(sketch, "E208.20.6.0", {"start": v(29.05, 19.44) * mm, "end": v(31.05, 19.44) * mm});
            skLineSegment(sketch, "E208.20.6.1", {"start": v(29.05, 19.44) * mm, "end": v(29.05, 17.44) * mm});
            skLineSegment(sketch, "E208.20.6.2", {"start": v(29.05, 17.44) * mm, "end": v(31.05, 17.44) * mm});
            skLineSegment(sketch, "E208.20.6.3", {"start": v(31.05, 19.44) * mm, "end": v(31.05, 17.44) * mm});
            skLineSegment(sketch, "E208.20.7.0", {"start": v(29.05, 15.44) * mm, "end": v(31.05, 15.44) * mm});
            skLineSegment(sketch, "E208.20.7.1", {"start": v(29.05, 15.44) * mm, "end": v(29.05, 13.44) * mm});
            skLineSegment(sketch, "E208.20.7.2", {"start": v(29.05, 13.44) * mm, "end": v(31.05, 13.44) * mm});
            skLineSegment(sketch, "E208.20.7.3", {"start": v(31.05, 15.44) * mm, "end": v(31.05, 13.44) * mm});
            skLineSegment(sketch, "E208.20.8.0", {"start": v(29.05, 11.44) * mm, "end": v(31.05, 11.44) * mm});
            skLineSegment(sketch, "E208.20.8.1", {"start": v(29.05, 11.44) * mm, "end": v(29.05, 9.44) * mm});
            skLineSegment(sketch, "E208.20.8.2", {"start": v(29.05, 9.44) * mm, "end": v(31.05, 9.44) * mm});
            skLineSegment(sketch, "E208.20.8.3", {"start": v(31.05, 11.44) * mm, "end": v(31.05, 9.44) * mm});
            skLineSegment(sketch, "E208.20.9.0", {"start": v(29.05, 7.44) * mm, "end": v(31.05, 7.44) * mm});
            skLineSegment(sketch, "E208.20.9.1", {"start": v(29.05, 7.44) * mm, "end": v(29.05, 5.44) * mm});
            skLineSegment(sketch, "E208.20.9.2", {"start": v(29.05, 5.44) * mm, "end": v(31.05, 5.44) * mm});
            skLineSegment(sketch, "E208.20.9.3", {"start": v(31.05, 7.44) * mm, "end": v(31.05, 5.44) * mm});
            skLineSegment(sketch, "E208.20.10.0", {"start": v(29.05, 3.44) * mm, "end": v(31.05, 3.44) * mm});
            skLineSegment(sketch, "E208.20.10.1", {"start": v(29.05, 3.44) * mm, "end": v(29.05, 1.44) * mm});
            skLineSegment(sketch, "E208.20.10.2", {"start": v(29.05, 1.44) * mm, "end": v(31.05, 1.44) * mm});
            skLineSegment(sketch, "E208.20.10.3", {"start": v(31.05, 3.44) * mm, "end": v(31.05, 1.44) * mm});
            skLineSegment(sketch, "E208.20.11.0", {"start": v(29.05, -0.56) * mm, "end": v(31.05, -0.56) * mm});
            skLineSegment(sketch, "E208.20.11.1", {"start": v(29.05, -0.56) * mm, "end": v(29.05, -2.56) * mm});
            skLineSegment(sketch, "E208.20.11.2", {"start": v(29.05, -2.56) * mm, "end": v(31.05, -2.56) * mm});
            skLineSegment(sketch, "E208.20.11.3", {"start": v(31.05, -0.56) * mm, "end": v(31.05, -2.56) * mm});
            skLineSegment(sketch, "E208.20.12.0", {"start": v(29.05, -4.56) * mm, "end": v(31.05, -4.56) * mm});
            skLineSegment(sketch, "E208.20.12.1", {"start": v(29.05, -4.56) * mm, "end": v(29.05, -6.56) * mm});
            skLineSegment(sketch, "E208.20.12.2", {"start": v(29.05, -6.56) * mm, "end": v(31.05, -6.56) * mm});
            skLineSegment(sketch, "E208.20.12.3", {"start": v(31.05, -4.56) * mm, "end": v(31.05, -6.56) * mm});
            skLineSegment(sketch, "E208.20.13.0", {"start": v(29.05, -8.56) * mm, "end": v(31.05, -8.56) * mm});
            skLineSegment(sketch, "E208.20.13.1", {"start": v(29.05, -8.56) * mm, "end": v(29.05, -10.56) * mm});
            skLineSegment(sketch, "E208.20.13.2", {"start": v(29.05, -10.56) * mm, "end": v(31.05, -10.56) * mm});
            skLineSegment(sketch, "E208.20.13.3", {"start": v(31.05, -8.56) * mm, "end": v(31.05, -10.56) * mm});
            skLineSegment(sketch, "E208.20.14.0", {"start": v(29.05, -12.56) * mm, "end": v(31.05, -12.56) * mm});
            skLineSegment(sketch, "E208.20.14.1", {"start": v(29.05, -12.56) * mm, "end": v(29.05, -14.56) * mm});
            skLineSegment(sketch, "E208.20.14.2", {"start": v(29.05, -14.56) * mm, "end": v(31.05, -14.56) * mm});
            skLineSegment(sketch, "E208.20.14.3", {"start": v(31.05, -12.56) * mm, "end": v(31.05, -14.56) * mm});
            skLineSegment(sketch, "E208.20.15.0", {"start": v(29.05, -16.56) * mm, "end": v(31.05, -16.56) * mm});
            skLineSegment(sketch, "E208.20.15.1", {"start": v(29.05, -16.56) * mm, "end": v(29.05, -18.56) * mm});
            skLineSegment(sketch, "E208.20.15.2", {"start": v(29.05, -18.56) * mm, "end": v(31.05, -18.56) * mm});
            skLineSegment(sketch, "E208.20.15.3", {"start": v(31.05, -16.56) * mm, "end": v(31.05, -18.56) * mm});
            skLineSegment(sketch, "E208.20.16.0", {"start": v(29.05, -20.56) * mm, "end": v(31.05, -20.56) * mm});
            skLineSegment(sketch, "E208.20.16.1", {"start": v(29.05, -20.56) * mm, "end": v(29.05, -22.56) * mm});
            skLineSegment(sketch, "E208.20.16.2", {"start": v(29.05, -22.56) * mm, "end": v(31.05, -22.56) * mm});
            skLineSegment(sketch, "E208.20.16.3", {"start": v(31.05, -20.56) * mm, "end": v(31.05, -22.56) * mm});
            skLineSegment(sketch, "E208.20.17.0", {"start": v(29.05, -24.56) * mm, "end": v(31.05, -24.56) * mm});
            skLineSegment(sketch, "E208.20.17.1", {"start": v(29.05, -24.56) * mm, "end": v(29.05, -26.56) * mm});
            skLineSegment(sketch, "E208.20.17.2", {"start": v(29.05, -26.56) * mm, "end": v(31.05, -26.56) * mm});
            skLineSegment(sketch, "E208.20.17.3", {"start": v(31.05, -24.56) * mm, "end": v(31.05, -26.56) * mm});
            skLineSegment(sketch, "E208.20.18.0", {"start": v(29.05, -28.56) * mm, "end": v(31.05, -28.56) * mm});
            skLineSegment(sketch, "E208.20.18.1", {"start": v(29.05, -28.56) * mm, "end": v(29.05, -30.56) * mm});
            skLineSegment(sketch, "E208.20.18.2", {"start": v(29.05, -30.56) * mm, "end": v(31.05, -30.56) * mm});
            skLineSegment(sketch, "E208.20.18.3", {"start": v(31.05, -28.56) * mm, "end": v(31.05, -30.56) * mm});
            skLineSegment(sketch, "E208.20.19.0", {"start": v(29.05, -32.56) * mm, "end": v(31.05, -32.56) * mm});
            skLineSegment(sketch, "E208.20.19.1", {"start": v(29.05, -32.56) * mm, "end": v(29.05, -34.56) * mm});
            skLineSegment(sketch, "E208.20.19.2", {"start": v(29.05, -34.56) * mm, "end": v(31.05, -34.56) * mm});
            skLineSegment(sketch, "E208.20.19.3", {"start": v(31.05, -32.56) * mm, "end": v(31.05, -34.56) * mm});
            skLineSegment(sketch, "E208.20.20.0", {"start": v(29.05, -36.56) * mm, "end": v(31.05, -36.56) * mm});
            skLineSegment(sketch, "E208.20.20.1", {"start": v(29.05, -36.56) * mm, "end": v(29.05, -38.56) * mm});
            skLineSegment(sketch, "E208.20.20.2", {"start": v(29.05, -38.56) * mm, "end": v(31.05, -38.56) * mm});
            skLineSegment(sketch, "E208.20.20.3", {"start": v(31.05, -36.56) * mm, "end": v(31.05, -38.56) * mm});
            skLineSegment(sketch, "E208.20.21.0", {"start": v(29.05, -40.56) * mm, "end": v(31.05, -40.56) * mm});
            skLineSegment(sketch, "E208.20.21.1", {"start": v(29.05, -40.56) * mm, "end": v(29.05, -42.56) * mm});
            skLineSegment(sketch, "E208.20.21.2", {"start": v(29.05, -42.56) * mm, "end": v(31.05, -42.56) * mm});
            skLineSegment(sketch, "E208.20.21.3", {"start": v(31.05, -40.56) * mm, "end": v(31.05, -42.56) * mm});
            skLineSegment(sketch, "E208.21.0.0", {"start": v(33.05, 43.44) * mm, "end": v(35.05, 43.44) * mm});
            skLineSegment(sketch, "E208.21.0.1", {"start": v(33.05, 43.44) * mm, "end": v(33.05, 41.44) * mm});
            skLineSegment(sketch, "E208.21.0.2", {"start": v(33.05, 41.44) * mm, "end": v(35.05, 41.44) * mm});
            skLineSegment(sketch, "E208.21.0.3", {"start": v(35.05, 43.44) * mm, "end": v(35.05, 41.44) * mm});
            skLineSegment(sketch, "E208.21.1.0", {"start": v(33.05, 39.44) * mm, "end": v(35.05, 39.44) * mm});
            skLineSegment(sketch, "E208.21.1.1", {"start": v(33.05, 39.44) * mm, "end": v(33.05, 37.44) * mm});
            skLineSegment(sketch, "E208.21.1.2", {"start": v(33.05, 37.44) * mm, "end": v(35.05, 37.44) * mm});
            skLineSegment(sketch, "E208.21.1.3", {"start": v(35.05, 39.44) * mm, "end": v(35.05, 37.44) * mm});
            skLineSegment(sketch, "E208.21.2.0", {"start": v(33.05, 35.44) * mm, "end": v(35.05, 35.44) * mm});
            skLineSegment(sketch, "E208.21.2.1", {"start": v(33.05, 35.44) * mm, "end": v(33.05, 33.44) * mm});
            skLineSegment(sketch, "E208.21.2.2", {"start": v(33.05, 33.44) * mm, "end": v(35.05, 33.44) * mm});
            skLineSegment(sketch, "E208.21.2.3", {"start": v(35.05, 35.44) * mm, "end": v(35.05, 33.44) * mm});
            skLineSegment(sketch, "E208.21.3.0", {"start": v(33.05, 31.44) * mm, "end": v(35.05, 31.44) * mm});
            skLineSegment(sketch, "E208.21.3.1", {"start": v(33.05, 31.44) * mm, "end": v(33.05, 29.44) * mm});
            skLineSegment(sketch, "E208.21.3.2", {"start": v(33.05, 29.44) * mm, "end": v(35.05, 29.44) * mm});
            skLineSegment(sketch, "E208.21.3.3", {"start": v(35.05, 31.44) * mm, "end": v(35.05, 29.44) * mm});
            skLineSegment(sketch, "E208.21.4.0", {"start": v(33.05, 27.44) * mm, "end": v(35.05, 27.44) * mm});
            skLineSegment(sketch, "E208.21.4.1", {"start": v(33.05, 27.44) * mm, "end": v(33.05, 25.44) * mm});
            skLineSegment(sketch, "E208.21.4.2", {"start": v(33.05, 25.44) * mm, "end": v(35.05, 25.44) * mm});
            skLineSegment(sketch, "E208.21.4.3", {"start": v(35.05, 27.44) * mm, "end": v(35.05, 25.44) * mm});
            skLineSegment(sketch, "E208.21.5.0", {"start": v(33.05, 23.44) * mm, "end": v(35.05, 23.44) * mm});
            skLineSegment(sketch, "E208.21.5.1", {"start": v(33.05, 23.44) * mm, "end": v(33.05, 21.44) * mm});
            skLineSegment(sketch, "E208.21.5.2", {"start": v(33.05, 21.44) * mm, "end": v(35.05, 21.44) * mm});
            skLineSegment(sketch, "E208.21.5.3", {"start": v(35.05, 23.44) * mm, "end": v(35.05, 21.44) * mm});
            skLineSegment(sketch, "E208.21.6.0", {"start": v(33.05, 19.44) * mm, "end": v(35.05, 19.44) * mm});
            skLineSegment(sketch, "E208.21.6.1", {"start": v(33.05, 19.44) * mm, "end": v(33.05, 17.44) * mm});
            skLineSegment(sketch, "E208.21.6.2", {"start": v(33.05, 17.44) * mm, "end": v(35.05, 17.44) * mm});
            skLineSegment(sketch, "E208.21.6.3", {"start": v(35.05, 19.44) * mm, "end": v(35.05, 17.44) * mm});
            skLineSegment(sketch, "E208.21.7.0", {"start": v(33.05, 15.44) * mm, "end": v(35.05, 15.44) * mm});
            skLineSegment(sketch, "E208.21.7.1", {"start": v(33.05, 15.44) * mm, "end": v(33.05, 13.44) * mm});
            skLineSegment(sketch, "E208.21.7.2", {"start": v(33.05, 13.44) * mm, "end": v(35.05, 13.44) * mm});
            skLineSegment(sketch, "E208.21.7.3", {"start": v(35.05, 15.44) * mm, "end": v(35.05, 13.44) * mm});
            skLineSegment(sketch, "E208.21.8.0", {"start": v(33.05, 11.44) * mm, "end": v(35.05, 11.44) * mm});
            skLineSegment(sketch, "E208.21.8.1", {"start": v(33.05, 11.44) * mm, "end": v(33.05, 9.44) * mm});
            skLineSegment(sketch, "E208.21.8.2", {"start": v(33.05, 9.44) * mm, "end": v(35.05, 9.44) * mm});
            skLineSegment(sketch, "E208.21.8.3", {"start": v(35.05, 11.44) * mm, "end": v(35.05, 9.44) * mm});
            skLineSegment(sketch, "E208.21.9.0", {"start": v(33.05, 7.44) * mm, "end": v(35.05, 7.44) * mm});
            skLineSegment(sketch, "E208.21.9.1", {"start": v(33.05, 7.44) * mm, "end": v(33.05, 5.44) * mm});
            skLineSegment(sketch, "E208.21.9.2", {"start": v(33.05, 5.44) * mm, "end": v(35.05, 5.44) * mm});
            skLineSegment(sketch, "E208.21.9.3", {"start": v(35.05, 7.44) * mm, "end": v(35.05, 5.44) * mm});
            skLineSegment(sketch, "E208.21.10.0", {"start": v(33.05, 3.44) * mm, "end": v(35.05, 3.44) * mm});
            skLineSegment(sketch, "E208.21.10.1", {"start": v(33.05, 3.44) * mm, "end": v(33.05, 1.44) * mm});
            skLineSegment(sketch, "E208.21.10.2", {"start": v(33.05, 1.44) * mm, "end": v(35.05, 1.44) * mm});
            skLineSegment(sketch, "E208.21.10.3", {"start": v(35.05, 3.44) * mm, "end": v(35.05, 1.44) * mm});
            skLineSegment(sketch, "E208.21.11.0", {"start": v(33.05, -0.56) * mm, "end": v(35.05, -0.56) * mm});
            skLineSegment(sketch, "E208.21.11.1", {"start": v(33.05, -0.56) * mm, "end": v(33.05, -2.56) * mm});
            skLineSegment(sketch, "E208.21.11.2", {"start": v(33.05, -2.56) * mm, "end": v(35.05, -2.56) * mm});
            skLineSegment(sketch, "E208.21.11.3", {"start": v(35.05, -0.56) * mm, "end": v(35.05, -2.56) * mm});
            skLineSegment(sketch, "E208.21.12.0", {"start": v(33.05, -4.56) * mm, "end": v(35.05, -4.56) * mm});
            skLineSegment(sketch, "E208.21.12.1", {"start": v(33.05, -4.56) * mm, "end": v(33.05, -6.56) * mm});
            skLineSegment(sketch, "E208.21.12.2", {"start": v(33.05, -6.56) * mm, "end": v(35.05, -6.56) * mm});
            skLineSegment(sketch, "E208.21.12.3", {"start": v(35.05, -4.56) * mm, "end": v(35.05, -6.56) * mm});
            skLineSegment(sketch, "E208.21.13.0", {"start": v(33.05, -8.56) * mm, "end": v(35.05, -8.56) * mm});
            skLineSegment(sketch, "E208.21.13.1", {"start": v(33.05, -8.56) * mm, "end": v(33.05, -10.56) * mm});
            skLineSegment(sketch, "E208.21.13.2", {"start": v(33.05, -10.56) * mm, "end": v(35.05, -10.56) * mm});
            skLineSegment(sketch, "E208.21.13.3", {"start": v(35.05, -8.56) * mm, "end": v(35.05, -10.56) * mm});
            skLineSegment(sketch, "E208.21.14.0", {"start": v(33.05, -12.56) * mm, "end": v(35.05, -12.56) * mm});
            skLineSegment(sketch, "E208.21.14.1", {"start": v(33.05, -12.56) * mm, "end": v(33.05, -14.56) * mm});
            skLineSegment(sketch, "E208.21.14.2", {"start": v(33.05, -14.56) * mm, "end": v(35.05, -14.56) * mm});
            skLineSegment(sketch, "E208.21.14.3", {"start": v(35.05, -12.56) * mm, "end": v(35.05, -14.56) * mm});
            skLineSegment(sketch, "E208.21.15.0", {"start": v(33.05, -16.56) * mm, "end": v(35.05, -16.56) * mm});
            skLineSegment(sketch, "E208.21.15.1", {"start": v(33.05, -16.56) * mm, "end": v(33.05, -18.56) * mm});
            skLineSegment(sketch, "E208.21.15.2", {"start": v(33.05, -18.56) * mm, "end": v(35.05, -18.56) * mm});
            skLineSegment(sketch, "E208.21.15.3", {"start": v(35.05, -16.56) * mm, "end": v(35.05, -18.56) * mm});
            skLineSegment(sketch, "E208.21.16.0", {"start": v(33.05, -20.56) * mm, "end": v(35.05, -20.56) * mm});
            skLineSegment(sketch, "E208.21.16.1", {"start": v(33.05, -20.56) * mm, "end": v(33.05, -22.56) * mm});
            skLineSegment(sketch, "E208.21.16.2", {"start": v(33.05, -22.56) * mm, "end": v(35.05, -22.56) * mm});
            skLineSegment(sketch, "E208.21.16.3", {"start": v(35.05, -20.56) * mm, "end": v(35.05, -22.56) * mm});
            skLineSegment(sketch, "E208.21.17.0", {"start": v(33.05, -24.56) * mm, "end": v(35.05, -24.56) * mm});
            skLineSegment(sketch, "E208.21.17.1", {"start": v(33.05, -24.56) * mm, "end": v(33.05, -26.56) * mm});
            skLineSegment(sketch, "E208.21.17.2", {"start": v(33.05, -26.56) * mm, "end": v(35.05, -26.56) * mm});
            skLineSegment(sketch, "E208.21.17.3", {"start": v(35.05, -24.56) * mm, "end": v(35.05, -26.56) * mm});
            skLineSegment(sketch, "E208.21.18.0", {"start": v(33.05, -28.56) * mm, "end": v(35.05, -28.56) * mm});
            skLineSegment(sketch, "E208.21.18.1", {"start": v(33.05, -28.56) * mm, "end": v(33.05, -30.56) * mm});
            skLineSegment(sketch, "E208.21.18.2", {"start": v(33.05, -30.56) * mm, "end": v(35.05, -30.56) * mm});
            skLineSegment(sketch, "E208.21.18.3", {"start": v(35.05, -28.56) * mm, "end": v(35.05, -30.56) * mm});
            skLineSegment(sketch, "E208.21.19.0", {"start": v(33.05, -32.56) * mm, "end": v(35.05, -32.56) * mm});
            skLineSegment(sketch, "E208.21.19.1", {"start": v(33.05, -32.56) * mm, "end": v(33.05, -34.56) * mm});
            skLineSegment(sketch, "E208.21.19.2", {"start": v(33.05, -34.56) * mm, "end": v(35.05, -34.56) * mm});
            skLineSegment(sketch, "E208.21.19.3", {"start": v(35.05, -32.56) * mm, "end": v(35.05, -34.56) * mm});
            skLineSegment(sketch, "E208.21.20.0", {"start": v(33.05, -36.56) * mm, "end": v(35.05, -36.56) * mm});
            skLineSegment(sketch, "E208.21.20.1", {"start": v(33.05, -36.56) * mm, "end": v(33.05, -38.56) * mm});
            skLineSegment(sketch, "E208.21.20.2", {"start": v(33.05, -38.56) * mm, "end": v(35.05, -38.56) * mm});
            skLineSegment(sketch, "E208.21.20.3", {"start": v(35.05, -36.56) * mm, "end": v(35.05, -38.56) * mm});
            skLineSegment(sketch, "E208.21.21.0", {"start": v(33.05, -40.56) * mm, "end": v(35.05, -40.56) * mm});
            skLineSegment(sketch, "E208.21.21.1", {"start": v(33.05, -40.56) * mm, "end": v(33.05, -42.56) * mm});
            skLineSegment(sketch, "E208.21.21.2", {"start": v(33.05, -42.56) * mm, "end": v(35.05, -42.56) * mm});
            skLineSegment(sketch, "E208.21.21.3", {"start": v(35.05, -40.56) * mm, "end": v(35.05, -42.56) * mm});
            skLineSegment(sketch, "E208.direction1", {"start": v(-50.95, 43.44) * mm, "end": v(-46.95, 43.44) * mm, "construction": true});
            skLineSegment(sketch, "E208.direction2", {"start": v(-50.95, 43.44) * mm, "end": v(-50.95, 39.44) * mm, "construction": true});
            skSolve(sketch);
        }
        {
            var Q0;
            {var subQ278=sQuery(id+"F23.wireOp",EDGE,"E171.0");Q0=makeQuery(id+"F23.imprint","IMPRINT",FACE,{"disambiguationData":[TD([[makeQuery(id+"F23.imprint","IMPRINT",EDGE,{"derivedFrom":subQ278}),-1.0]])]});}
            extrude(context, id + "F24", {"entities" : qUnion([Q0]), "operationType" : NewBodyOperationType.REMOVE, "oppositeDirection" : true, "depth" : 0.5 * mm});
        }
        {
            var Q0;
            Q0=makeQuery(id+"F6.opRevolve","SWEPT_FACE",FACE,{"disambiguationData":[OSD([sQuery(id+"F0.wireOp",EDGE,"E31")])]});
            var sketch = newSketch(context, id + "F25", { "sketchPlane" : qUnion([Q0])});
            skPoint(sketch, "E209", {"position": v(-7.53, 0) * mm});
            skCircle(sketch, "E210", {"center": v(-7.53, 0) * mm, "radius": 23 * mm});
            skLineSegment(sketch, "E211", {"start": v(-7.53, 0) * mm, "end": v(-35.11, 0) * mm, "construction": true});
            skLineSegment(sketch, "E212", {"start": v(-7.53, 0) * mm, "end": v(-7.53, 27.58) * mm, "construction": true});
            skCircle(sketch, "E213", {"center": v(-7.53, 27.58) * mm, "radius": 1.15 * mm});
            skCircle(sketch, "E214", {"center": v(-35.11, 0) * mm, "radius": 1.15 * mm});
            skCircle(sketch, "E215.MirrorC", {"center": v(-7.53, -27.58) * mm, "radius": 1.15 * mm});
            skCircle(sketch, "E216.MirrorC", {"center": v(20.04, 0) * mm, "radius": 1.15 * mm});
            skSolve(sketch);
        }
        {
            var Q0;
            Q0=qSketchRegion(id+"F25",true);
            extrude(context, id + "F26", {"entities" : qUnion([Q0]), "operationType" : NewBodyOperationType.REMOVE, "endBound" : BoundingType.UP_TO_NEXT, "oppositeDirection" : true, "depth" : 25 * mm});
        }
    });
